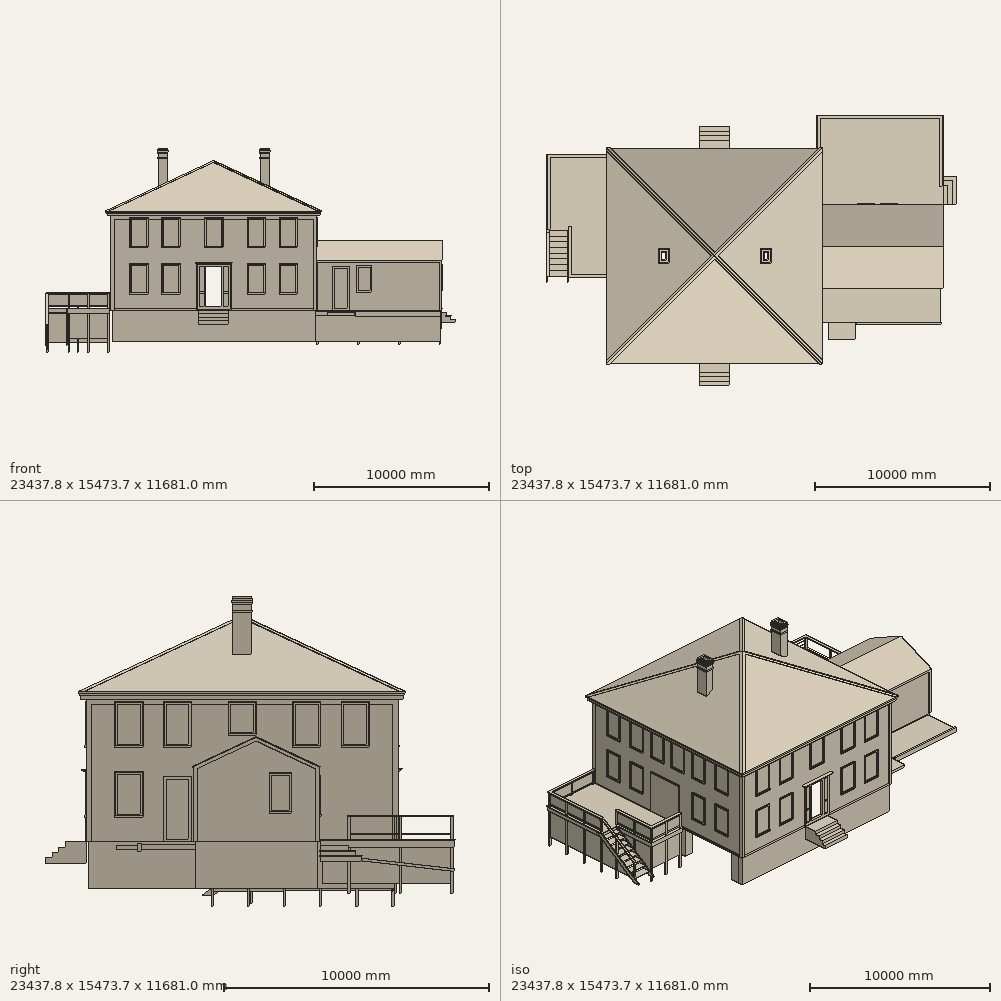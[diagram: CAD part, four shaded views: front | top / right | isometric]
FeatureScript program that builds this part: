
annotation { "Feature Type Name" : "Feature", "Feature Type Description" : "" }
export const myFeature = defineFeature(function(context is Context, id is Id, definition is map)
    precondition{}
    {
        {
            var Q0;
            Q0=qCreatedBy(makeId("Top.planeOp"),FACE);
            var sketch = newSketch(context, id + "F0", { "sketchPlane" : qUnion([Q0])});
            skLineSegment(sketch, "E0.bottom", {"start": v(0, 0) * mm, "end": v(11785.6, 0) * mm});
            skLineSegment(sketch, "E0.top", {"start": v(0, 11785.6) * mm, "end": v(11785.6, 11785.6) * mm});
            skLineSegment(sketch, "E0.left", {"start": v(0, 0) * mm, "end": v(0, 11785.6) * mm});
            skLineSegment(sketch, "E0.right", {"start": v(11785.6, 0) * mm, "end": v(11785.6, 11785.6) * mm});
            skSolve(sketch);
        }
        {
            var Q0;
            Q0=makeQuery(id+"F0.imprint","IMPRINT",FACE,{"disambiguationData":[TD([[makeQuery(id+"F0.imprint","IMPRINT",EDGE,{"derivedFrom":sQuery(id+"F0.wireOp",EDGE,"E0.bottom")}),1.0]])]});
            extrude(context, id + "F1", {"entities" : qUnion([Q0]), "depth" : 5384.8 * mm});
        }
        {
            var Q0;
            Q0=makeQuery(id+"F1.opExtrude","CAP_FACE",FACE,{"disambiguationData":[OSD([sQuery(id+"F0.wireOp",EDGE,"E0.bottom"),sQuery(id+"F0.wireOp",EDGE,"E0.top"),sQuery(id+"F0.wireOp",EDGE,"E0.left"),sQuery(id+"F0.wireOp",EDGE,"E0.right")])],"isStart":false});
            var sketch = newSketch(context, id + "F2", { "sketchPlane" : qUnion([Q0])});
            skLineSegment(sketch, "E1.0", {"start": v(11988.8, 11988.8) * mm, "end": v(-203.2, 11988.8) * mm});
            skLineSegment(sketch, "E1.1", {"start": v(11988.8, -203.2) * mm, "end": v(11988.8, 11988.8) * mm});
            skLineSegment(sketch, "E1.2", {"start": v(-203.2, -203.2) * mm, "end": v(11988.8, -203.2) * mm});
            skLineSegment(sketch, "E1.3", {"start": v(-203.2, 11988.8) * mm, "end": v(-203.2, -203.2) * mm});
            skSolve(sketch);
        }
        {
            var Q0;
            Q0 = qSketchRegion(id + "F2", true);
            extrude(context, id + "F3", {"entities" : qUnion([Q0]), "operationType" : NewBodyOperationType.ADD, "depth" : 152.4 * mm});
        }
        {
            var Q0;
            Q0=makeQuery(id+"F3.opExtrude","CAP_FACE",FACE,{"disambiguationData":[OSD([sQuery(id+"F2.wireOp",EDGE,"E1.0"),sQuery(id+"F2.wireOp",EDGE,"E1.1"),sQuery(id+"F2.wireOp",EDGE,"E1.2"),sQuery(id+"F2.wireOp",EDGE,"E1.3")])],"isStart":false});
            var sketch = newSketch(context, id + "F4", { "sketchPlane" : qUnion([Q0])});
            skLineSegment(sketch, "E2.0", {"start": v(12014.2, 12014.2) * mm, "end": v(-228.6, 12014.2) * mm});
            skLineSegment(sketch, "E2.1", {"start": v(12014.2, -228.6) * mm, "end": v(12014.2, 12014.2) * mm});
            skLineSegment(sketch, "E2.2", {"start": v(-228.6, -228.6) * mm, "end": v(12014.2, -228.6) * mm});
            skLineSegment(sketch, "E2.3", {"start": v(-228.6, 12014.2) * mm, "end": v(-228.6, -228.6) * mm});
            skSolve(sketch);
        }
        {
            var Q0;
            Q0 = qSketchRegion(id + "F4", true);
            extrude(context, id + "F5", {"entities" : qUnion([Q0]), "operationType" : NewBodyOperationType.ADD, "depth" : 38.1 * mm});
        }
        {
            var Q0;
            Q0=makeQuery(id+"F5.opExtrude","CAP_FACE",FACE,{"disambiguationData":[OSD([sQuery(id+"F4.wireOp",EDGE,"E2.0"),sQuery(id+"F4.wireOp",EDGE,"E2.1"),sQuery(id+"F4.wireOp",EDGE,"E2.2"),sQuery(id+"F4.wireOp",EDGE,"E2.3")])],"isStart":false});
            var sketch = newSketch(context, id + "F6", { "sketchPlane" : qUnion([Q0])});
            skLineSegment(sketch, "E3.0", {"start": v(12065, 12065) * mm, "end": v(-279.4, 12065) * mm});
            skLineSegment(sketch, "E3.1", {"start": v(12065, -279.4) * mm, "end": v(12065, 12065) * mm});
            skLineSegment(sketch, "E3.2", {"start": v(-279.4, -279.4) * mm, "end": v(12065, -279.4) * mm});
            skLineSegment(sketch, "E3.3", {"start": v(-279.4, 12065) * mm, "end": v(-279.4, -279.4) * mm});
            skSolve(sketch);
        }
        {
            var Q0;
            Q0 = qSketchRegion(id + "F6", true);
            extrude(context, id + "F7", {"entities" : qUnion([Q0]), "operationType" : NewBodyOperationType.ADD, "depth" : 76.2 * mm});
        }
        {
            var Q0;
            Q0=makeQuery(id+"F7.opExtrude","CAP_FACE",FACE,{"disambiguationData":[OSD([sQuery(id+"F6.wireOp",EDGE,"E3.0"),sQuery(id+"F6.wireOp",EDGE,"E3.1"),sQuery(id+"F6.wireOp",EDGE,"E3.2"),sQuery(id+"F6.wireOp",EDGE,"E3.3")])],"isStart":false});
            extrude(context, id + "F8", {"entities" : qUnion([Q0]), "operationType" : NewBodyOperationType.ADD, "depth" : 2921 * mm, "hasDraft" : true, "draftAngle" : 65 * degree, "draftPullDirection" : true});
        }
        {
            var Q0;
            Q0=makeQuery(id+"F1.opExtrude","SWEPT_FACE",FACE,{"disambiguationData":[OSD([sQuery(id+"F0.wireOp",EDGE,"E0.right")])]});
            var sketch = newSketch(context, id + "F9", { "sketchPlane" : qUnion([Q0])});
            skLineSegment(sketch, "E4", {"start": v(203.2, 0) * mm, "end": v(203.2, 5181.6) * mm});
            skLineSegment(sketch, "E5", {"start": v(203.2, 5181.6) * mm, "end": v(11582.4, 5181.6) * mm});
            skLineSegment(sketch, "E6", {"start": v(11582.4, 5181.6) * mm, "end": v(11582.4, 0) * mm});
            skSolve(sketch);
        }
        {
            var Q0;
            {var subQ0=sQuery(id+"F9.wireOp",EDGE,"E4");Q0=makeQuery(id+"F9.imprint","IMPRINT",FACE,{"disambiguationData":[TD([[makeQuery(id+"F9.imprint","IMPRINT",EDGE,{"derivedFrom":subQ0}),-1.0]])]});}
            extrude(context, id + "F10", {"entities" : qUnion([Q0]), "operationType" : NewBodyOperationType.REMOVE, "oppositeDirection" : true, "depth" : 25.4 * mm});
        }
        {
            var Q0;
            Q0=makeQuery(id+"F1.opExtrude","SWEPT_FACE",FACE,{"disambiguationData":[OSD([sQuery(id+"F0.wireOp",EDGE,"E0.left")])]});
            var sketch = newSketch(context, id + "F11", { "sketchPlane" : qUnion([Q0])});
            skLineSegment(sketch, "E7.0.0", {"start": v(-11582.4, 0) * mm, "end": v(-11582.4, 5181.6) * mm});
            skLineSegment(sketch, "E7.0.1", {"start": v(-11582.4, 5181.6) * mm, "end": v(-203.2, 5181.6) * mm});
            skLineSegment(sketch, "E7.0.2", {"start": v(-203.2, 5181.6) * mm, "end": v(-203.2, 0) * mm});
            skLineSegment(sketch, "E7.0.3", {"start": v(-203.2, 0) * mm, "end": v(-11582.4, 0) * mm});
            skSolve(sketch);
        }
        {
            var Q0;
            Q0 = qSketchRegion(id + "F11", true);
            extrude(context, id + "F12", {"entities" : qUnion([Q0]), "operationType" : NewBodyOperationType.REMOVE, "oppositeDirection" : true, "depth" : 25.4 * mm});
        }
        {
            var Q0;
            Q0=makeQuery(id+"F1.opExtrude","SWEPT_FACE",FACE,{"disambiguationData":[OSD([sQuery(id+"F0.wireOp",EDGE,"E0.top")])]});
            var sketch = newSketch(context, id + "F13", { "sketchPlane" : qUnion([Q0])});
            skLineSegment(sketch, "E8", {"start": v(-11582.4, 0) * mm, "end": v(-11582.4, 5181.6) * mm});
            skLineSegment(sketch, "E9", {"start": v(-11582.4, 5181.6) * mm, "end": v(-203.2, 5181.6) * mm});
            skLineSegment(sketch, "E10", {"start": v(-203.2, 5181.6) * mm, "end": v(-203.2, 0) * mm});
            skSolve(sketch);
        }
        {
            var Q0;
            {var subQ0=sQuery(id+"F13.wireOp",EDGE,"E8");Q0=makeQuery(id+"F13.imprint","IMPRINT",FACE,{"disambiguationData":[TD([[makeQuery(id+"F13.imprint","IMPRINT",EDGE,{"derivedFrom":subQ0}),-1.0]])]});}
            extrude(context, id + "F14", {"entities" : qUnion([Q0]), "operationType" : NewBodyOperationType.REMOVE, "oppositeDirection" : true, "depth" : 25.4 * mm});
        }
        {
            var Q0;
            Q0=makeQuery(id+"F1.opExtrude","SWEPT_FACE",FACE,{"disambiguationData":[OSD([sQuery(id+"F0.wireOp",EDGE,"E0.bottom")])]});
            var sketch = newSketch(context, id + "F15", { "sketchPlane" : qUnion([Q0])});
            skLineSegment(sketch, "E11.0.0", {"start": v(203.2, 0) * mm, "end": v(203.2, 5181.6) * mm});
            skLineSegment(sketch, "E11.0.1", {"start": v(203.2, 5181.6) * mm, "end": v(11582.4, 5181.6) * mm});
            skLineSegment(sketch, "E11.0.2", {"start": v(11582.4, 5181.6) * mm, "end": v(11582.4, 0) * mm});
            skLineSegment(sketch, "E11.0.3", {"start": v(11582.4, 0) * mm, "end": v(203.2, 0) * mm});
            skSolve(sketch);
        }
        {
            var Q0;
            Q0=makeQuery(id+"F15.imprint","IMPRINT",FACE,{"disambiguationData":[TD([[makeQuery(id+"F15.imprint","IMPRINT",EDGE,{"derivedFrom":sQuery(id+"F15.wireOp",EDGE,"E11.0.0")}),-1.0]])]});
            extrude(context, id + "F16", {"entities" : qUnion([Q0]), "operationType" : NewBodyOperationType.REMOVE, "oppositeDirection" : true, "depth" : 25.4 * mm});
        }
        {
            var Q0;
            Q0=makeQuery(id+"F16.boolean.opBoolean","COPY",FACE,{"derivedFrom":makeQuery(id+"F16.opExtrude","CAP_FACE",FACE,{"disambiguationData":[OSD([sQuery(id+"F15.wireOp",EDGE,"E11.0.0"),sQuery(id+"F15.wireOp",EDGE,"E11.0.1"),sQuery(id+"F15.wireOp",EDGE,"E11.0.2"),sQuery(id+"F15.wireOp",EDGE,"E11.0.3")])],"isStart":false})});
            var sketch = newSketch(context, id + "F17", { "sketchPlane" : qUnion([Q0])});
            skLineSegment(sketch, "E12", {"start": v(5892.8, 5181.6) * mm, "end": v(5892.8, 3556) * mm, "construction": true});
            skPoint(sketch, "E12.endSnap0", {"position": v(5892.8, 5181.6) * mm});
            skLineSegment(sketch, "E13.bottom", {"start": v(9626.6, 5283.2) * mm, "end": v(10693.4, 5283.2) * mm});
            skLineSegment(sketch, "E13.top", {"start": v(9626.6, 3556) * mm, "end": v(10693.4, 3556) * mm});
            skLineSegment(sketch, "E13.left", {"start": v(9626.6, 5283.2) * mm, "end": v(9626.6, 3556) * mm});
            skLineSegment(sketch, "E13.right", {"start": v(10693.4, 5283.2) * mm, "end": v(10693.4, 3556) * mm});
            skLineSegment(sketch, "E14.bottom", {"start": v(7797.8, 5283.2) * mm, "end": v(8864.6, 5283.2) * mm});
            skLineSegment(sketch, "E14.top", {"start": v(7797.8, 3556) * mm, "end": v(8864.6, 3556) * mm});
            skLineSegment(sketch, "E14.left", {"start": v(7797.8, 5283.2) * mm, "end": v(7797.8, 3556) * mm});
            skLineSegment(sketch, "E14.right", {"start": v(8864.6, 5283.2) * mm, "end": v(8864.6, 3556) * mm});
            skLineSegment(sketch, "E15.bottom", {"start": v(5359.4, 5283.2) * mm, "end": v(6426.2, 5283.2) * mm});
            skLineSegment(sketch, "E15.top", {"start": v(5359.4, 3556) * mm, "end": v(6426.2, 3556) * mm});
            skLineSegment(sketch, "E15.left", {"start": v(5359.4, 5283.2) * mm, "end": v(5359.4, 3556) * mm});
            skLineSegment(sketch, "E15.right", {"start": v(6426.2, 5283.2) * mm, "end": v(6426.2, 3556) * mm});
            skLineSegment(sketch, "E16.bottom", {"start": v(2921, 5283.2) * mm, "end": v(3987.8, 5283.2) * mm});
            skLineSegment(sketch, "E16.top", {"start": v(2921, 3556) * mm, "end": v(3987.8, 3556) * mm});
            skLineSegment(sketch, "E16.left", {"start": v(2921, 5283.2) * mm, "end": v(2921, 3556) * mm});
            skLineSegment(sketch, "E16.right", {"start": v(3987.8, 5283.2) * mm, "end": v(3987.8, 3556) * mm});
            skLineSegment(sketch, "E17.bottom", {"start": v(1092.2, 5283.2) * mm, "end": v(2159, 5283.2) * mm});
            skLineSegment(sketch, "E17.top", {"start": v(1092.2, 3556) * mm, "end": v(2159, 3556) * mm});
            skLineSegment(sketch, "E17.left", {"start": v(1092.2, 5283.2) * mm, "end": v(1092.2, 3556) * mm});
            skLineSegment(sketch, "E17.right", {"start": v(2159, 5283.2) * mm, "end": v(2159, 3556) * mm});
            skLineSegment(sketch, "E18.bottom", {"start": v(1092.2, 2641.6) * mm, "end": v(2159, 2641.6) * mm});
            skLineSegment(sketch, "E18.top", {"start": v(1092.2, 914.4) * mm, "end": v(2159, 914.4) * mm});
            skLineSegment(sketch, "E18.left", {"start": v(1092.2, 2641.6) * mm, "end": v(1092.2, 914.4) * mm});
            skLineSegment(sketch, "E18.right", {"start": v(2159, 2641.6) * mm, "end": v(2159, 914.4) * mm});
            skLineSegment(sketch, "E19.bottom", {"start": v(2921, 2641.6) * mm, "end": v(3987.8, 2641.6) * mm});
            skLineSegment(sketch, "E19.top", {"start": v(2921, 914.4) * mm, "end": v(3987.8, 914.4) * mm});
            skLineSegment(sketch, "E19.left", {"start": v(2921, 2641.6) * mm, "end": v(2921, 914.4) * mm});
            skLineSegment(sketch, "E19.right", {"start": v(3987.8, 2641.6) * mm, "end": v(3987.8, 914.4) * mm});
            skLineSegment(sketch, "E20.bottom", {"start": v(7797.8, 2641.6) * mm, "end": v(8864.6, 2641.6) * mm});
            skLineSegment(sketch, "E20.top", {"start": v(7797.8, 914.4) * mm, "end": v(8864.6, 914.4) * mm});
            skLineSegment(sketch, "E20.left", {"start": v(7797.8, 2641.6) * mm, "end": v(7797.8, 914.4) * mm});
            skLineSegment(sketch, "E20.right", {"start": v(8864.6, 2641.6) * mm, "end": v(8864.6, 914.4) * mm});
            skLineSegment(sketch, "E21.bottom", {"start": v(9626.6, 2641.6) * mm, "end": v(10693.4, 2641.6) * mm});
            skLineSegment(sketch, "E21.top", {"start": v(9626.6, 914.4) * mm, "end": v(10693.4, 914.4) * mm});
            skLineSegment(sketch, "E21.left", {"start": v(9626.6, 2641.6) * mm, "end": v(9626.6, 914.4) * mm});
            skLineSegment(sketch, "E21.right", {"start": v(10693.4, 2641.6) * mm, "end": v(10693.4, 914.4) * mm});
            skLineSegment(sketch, "E22.bottom", {"start": v(4902.2, 2641.6) * mm, "end": v(6883.4, 2641.6) * mm});
            skLineSegment(sketch, "E22.top", {"start": v(4902.2, 0) * mm, "end": v(6883.4, 0) * mm});
            skLineSegment(sketch, "E22.left", {"start": v(4902.2, 2641.6) * mm, "end": v(4902.2, 0) * mm});
            skLineSegment(sketch, "E22.right", {"start": v(6883.4, 2641.6) * mm, "end": v(6883.4, 0) * mm});
            skSolve(sketch);
        }
        {
            var Q0;
            Q0 = qSketchRegion(id + "F17", true);
            extrude(context, id + "F18", {"entities" : qUnion([Q0]), "operationType" : NewBodyOperationType.ADD, "depth" : 30.48 * mm});
        }
        {
            var Q0;
            Q0=makeQuery(id+"F10.boolean.opBoolean","COPY",FACE,{"derivedFrom":makeQuery(id+"F10.opExtrude","CAP_FACE",FACE,{"disambiguationData":[OSD([sQuery(id+"F0.wireOp",EDGE,"E0.right"),sQuery(id+"F9.wireOp",EDGE,"E4"),sQuery(id+"F9.wireOp",EDGE,"E5"),sQuery(id+"F9.wireOp",EDGE,"E6")])],"isStart":false})});
            var sketch = newSketch(context, id + "F19", { "sketchPlane" : qUnion([Q0])});
            skLineSegment(sketch, "E23.bottom", {"start": v(1092.2, 5283.2) * mm, "end": v(2159, 5283.2) * mm});
            skLineSegment(sketch, "E23.top", {"start": v(1092.2, 3556) * mm, "end": v(2159, 3556) * mm});
            skLineSegment(sketch, "E23.left", {"start": v(1092.2, 5283.2) * mm, "end": v(1092.2, 3556) * mm});
            skLineSegment(sketch, "E23.right", {"start": v(2159, 5283.2) * mm, "end": v(2159, 3556) * mm});
            skLineSegment(sketch, "E24.bottom", {"start": v(2921, 5283.2) * mm, "end": v(3987.8, 5283.2) * mm});
            skLineSegment(sketch, "E24.top", {"start": v(2921, 3556) * mm, "end": v(3987.8, 3556) * mm});
            skLineSegment(sketch, "E24.left", {"start": v(2921, 5283.2) * mm, "end": v(2921, 3556) * mm});
            skLineSegment(sketch, "E24.right", {"start": v(3987.8, 5283.2) * mm, "end": v(3987.8, 3556) * mm});
            skLineSegment(sketch, "E25.bottom", {"start": v(5359.4, 5283.2) * mm, "end": v(6426.2, 5283.2) * mm});
            skLineSegment(sketch, "E25.left", {"start": v(5359.4, 5283.2) * mm, "end": v(5359.4, 4013.2) * mm});
            skLineSegment(sketch, "E25.right", {"start": v(6426.2, 5283.2) * mm, "end": v(6426.2, 4013.2) * mm});
            skLineSegment(sketch, "E26.bottom", {"start": v(7797.8, 5283.2) * mm, "end": v(8864.6, 5283.2) * mm});
            skLineSegment(sketch, "E26.top", {"start": v(7797.8, 3556) * mm, "end": v(8864.6, 3556) * mm});
            skLineSegment(sketch, "E26.left", {"start": v(7797.8, 5283.2) * mm, "end": v(7797.8, 3556) * mm});
            skLineSegment(sketch, "E26.right", {"start": v(8864.6, 5283.2) * mm, "end": v(8864.6, 3556) * mm});
            skLineSegment(sketch, "E27.bottom", {"start": v(9626.6, 5283.2) * mm, "end": v(10693.4, 5283.2) * mm});
            skLineSegment(sketch, "E27.top", {"start": v(9626.6, 3556) * mm, "end": v(10693.4, 3556) * mm});
            skLineSegment(sketch, "E27.left", {"start": v(9626.6, 5283.2) * mm, "end": v(9626.6, 3556) * mm});
            skLineSegment(sketch, "E27.right", {"start": v(10693.4, 5283.2) * mm, "end": v(10693.4, 3556) * mm});
            skLineSegment(sketch, "E28", {"start": v(5892.8, 5181.6) * mm, "end": v(5892.8, 4013.2) * mm, "construction": true});
            skPoint(sketch, "E28.endSnap0", {"position": v(5892.8, 5181.6) * mm});
            skLineSegment(sketch, "E29.bottom", {"start": v(1092.2, 2641.6) * mm, "end": v(2159, 2641.6) * mm});
            skLineSegment(sketch, "E29.top", {"start": v(1092.2, 914.4) * mm, "end": v(2159, 914.4) * mm});
            skLineSegment(sketch, "E29.left", {"start": v(1092.2, 2641.6) * mm, "end": v(1092.2, 914.4) * mm});
            skLineSegment(sketch, "E29.right", {"start": v(2159, 2641.6) * mm, "end": v(2159, 914.4) * mm});
            skLineSegment(sketch, "E30.bottom", {"start": v(2921, 2463.8) * mm, "end": v(3987.8, 2463.8) * mm});
            skLineSegment(sketch, "E30.top", {"start": v(2921, 0) * mm, "end": v(3987.8, 0) * mm});
            skLineSegment(sketch, "E30.left", {"start": v(2921, 2463.8) * mm, "end": v(2921, 0) * mm});
            skLineSegment(sketch, "E30.right", {"start": v(3987.8, 2463.8) * mm, "end": v(3987.8, 0) * mm});
            skLineSegment(sketch, "E31", {"start": v(5359.4, 4013.2) * mm, "end": v(6426.2, 4013.2) * mm});
            skPoint(sketch, "E32.orphan", {"position": v(6426.2, 3556) * mm});
            skSolve(sketch);
        }
        {
            var Q0;
            Q0 = qSketchRegion(id + "F19", true);
            extrude(context, id + "F20", {"entities" : qUnion([Q0]), "operationType" : NewBodyOperationType.ADD, "depth" : 30.48 * mm});
        }
        {
            var Q0;
            Q0=makeQuery(id+"F10.boolean.opBoolean","COPY",FACE,{"derivedFrom":makeQuery(id+"F10.opExtrude","CAP_FACE",FACE,{"disambiguationData":[OSD([sQuery(id+"F0.wireOp",EDGE,"E0.right"),sQuery(id+"F9.wireOp",EDGE,"E4"),sQuery(id+"F9.wireOp",EDGE,"E5"),sQuery(id+"F9.wireOp",EDGE,"E6")])],"isStart":false})});
            var sketch = newSketch(context, id + "F21", { "sketchPlane" : qUnion([Q0])});
            skLineSegment(sketch, "E33", {"start": v(6426.2, 3962.4) * mm, "end": v(8813.8, 2844.8) * mm});
            skLineSegment(sketch, "E34", {"start": v(6426.2, 3962.4) * mm, "end": v(4038.6, 2844.8) * mm});
            skLineSegment(sketch, "E35", {"start": v(4038.6, 2844.8) * mm, "end": v(4038.6, 0) * mm});
            skLineSegment(sketch, "E36", {"start": v(8813.8, 2844.8) * mm, "end": v(8813.8, 0) * mm});
            skLineSegment(sketch, "E37", {"start": v(4038.6, 0) * mm, "end": v(8813.8, 0) * mm});
            skLineSegment(sketch, "E38", {"start": v(6426.2, 3962.4) * mm, "end": v(6426.2, 2033.92) * mm, "construction": true});
            skSolve(sketch);
        }
        {
            var Q0;
            Q0=makeQuery(id+"F21.imprint","IMPRINT",FACE,{"disambiguationData":[TD([[makeQuery(id+"F21.imprint","IMPRINT",EDGE,{"derivedFrom":sQuery(id+"F21.wireOp",EDGE,"E33")}),-1.0]])]});
            extrude(context, id + "F22", {"entities" : qUnion([Q0]), "operationType" : NewBodyOperationType.ADD, "depth" : 7162.8 * mm});
        }
        {
            var Q0;
            Q0=makeQuery(id+"F14.boolean.opBoolean","COPY",FACE,{"derivedFrom":makeQuery(id+"F14.opExtrude","CAP_FACE",FACE,{"disambiguationData":[OSD([sQuery(id+"F0.wireOp",EDGE,"E0.top"),sQuery(id+"F13.wireOp",EDGE,"E8"),sQuery(id+"F13.wireOp",EDGE,"E9"),sQuery(id+"F13.wireOp",EDGE,"E10")])],"isStart":false})});
            var sketch = newSketch(context, id + "F23", { "sketchPlane" : qUnion([Q0])});
            skLineSegment(sketch, "E39.0.0", {"start": v(-2159, 3556) * mm, "end": v(-2159, 5283.2) * mm});
            skLineSegment(sketch, "E39.0.1", {"start": v(-2159, 5283.2) * mm, "end": v(-1092.2, 5283.2) * mm});
            skLineSegment(sketch, "E39.0.2", {"start": v(-1092.2, 5283.2) * mm, "end": v(-1092.2, 3556) * mm});
            skLineSegment(sketch, "E39.0.3", {"start": v(-1092.2, 3556) * mm, "end": v(-2159, 3556) * mm});
            skLineSegment(sketch, "E39.1.0", {"start": v(-3987.8, 3556) * mm, "end": v(-3987.8, 5283.2) * mm});
            skLineSegment(sketch, "E39.1.1", {"start": v(-3987.8, 5283.2) * mm, "end": v(-2921, 5283.2) * mm});
            skLineSegment(sketch, "E39.1.2", {"start": v(-2921, 5283.2) * mm, "end": v(-2921, 3556) * mm});
            skLineSegment(sketch, "E39.1.3", {"start": v(-2921, 3556) * mm, "end": v(-3987.8, 3556) * mm});
            skLineSegment(sketch, "E39.2.0", {"start": v(-6426.2, 3556) * mm, "end": v(-6426.2, 5283.2) * mm});
            skLineSegment(sketch, "E39.2.1", {"start": v(-6426.2, 5283.2) * mm, "end": v(-5359.4, 5283.2) * mm});
            skLineSegment(sketch, "E39.2.2", {"start": v(-5359.4, 5283.2) * mm, "end": v(-5359.4, 3556) * mm});
            skLineSegment(sketch, "E39.2.3", {"start": v(-5359.4, 3556) * mm, "end": v(-6426.2, 3556) * mm});
            skLineSegment(sketch, "E39.3.0", {"start": v(-8864.6, 3556) * mm, "end": v(-8864.6, 5283.2) * mm});
            skLineSegment(sketch, "E39.3.1", {"start": v(-8864.6, 5283.2) * mm, "end": v(-7797.8, 5283.2) * mm});
            skLineSegment(sketch, "E39.3.2", {"start": v(-7797.8, 5283.2) * mm, "end": v(-7797.8, 3556) * mm});
            skLineSegment(sketch, "E39.3.3", {"start": v(-7797.8, 3556) * mm, "end": v(-8864.6, 3556) * mm});
            skLineSegment(sketch, "E39.4.0", {"start": v(-10693.4, 3556) * mm, "end": v(-10693.4, 5283.2) * mm});
            skLineSegment(sketch, "E39.4.1", {"start": v(-10693.4, 5283.2) * mm, "end": v(-9626.6, 5283.2) * mm});
            skLineSegment(sketch, "E39.4.2", {"start": v(-9626.6, 5283.2) * mm, "end": v(-9626.6, 3556) * mm});
            skLineSegment(sketch, "E39.4.3", {"start": v(-9626.6, 3556) * mm, "end": v(-10693.4, 3556) * mm});
            skLineSegment(sketch, "E39.5.0", {"start": v(-9626.6, 2641.6) * mm, "end": v(-9626.6, 914.4) * mm});
            skLineSegment(sketch, "E39.5.1", {"start": v(-9626.6, 914.4) * mm, "end": v(-10693.4, 914.4) * mm});
            skLineSegment(sketch, "E39.5.2", {"start": v(-10693.4, 914.4) * mm, "end": v(-10693.4, 2641.6) * mm});
            skLineSegment(sketch, "E39.5.3", {"start": v(-10693.4, 2641.6) * mm, "end": v(-9626.6, 2641.6) * mm});
            skLineSegment(sketch, "E39.6.0", {"start": v(-7797.8, 2641.6) * mm, "end": v(-7797.8, 914.4) * mm});
            skLineSegment(sketch, "E39.6.1", {"start": v(-7797.8, 914.4) * mm, "end": v(-8864.6, 914.4) * mm});
            skLineSegment(sketch, "E39.6.2", {"start": v(-8864.6, 914.4) * mm, "end": v(-8864.6, 2641.6) * mm});
            skLineSegment(sketch, "E39.6.3", {"start": v(-8864.6, 2641.6) * mm, "end": v(-7797.8, 2641.6) * mm});
            skLineSegment(sketch, "E39.7.0", {"start": v(-6883.4, 0) * mm, "end": v(-6883.4, 2641.6) * mm});
            skLineSegment(sketch, "E39.7.1", {"start": v(-6883.4, 2641.6) * mm, "end": v(-4902.2, 2641.6) * mm});
            skLineSegment(sketch, "E39.7.2", {"start": v(-4902.2, 2641.6) * mm, "end": v(-4902.2, 0) * mm});
            skLineSegment(sketch, "E39.7.3", {"start": v(-4902.2, 0) * mm, "end": v(-6883.4, 0) * mm});
            skLineSegment(sketch, "E39.8.0", {"start": v(-2921, 2641.6) * mm, "end": v(-2921, 914.4) * mm});
            skLineSegment(sketch, "E39.8.1", {"start": v(-2921, 914.4) * mm, "end": v(-3987.8, 914.4) * mm});
            skLineSegment(sketch, "E39.8.2", {"start": v(-3987.8, 914.4) * mm, "end": v(-3987.8, 2641.6) * mm});
            skLineSegment(sketch, "E39.8.3", {"start": v(-3987.8, 2641.6) * mm, "end": v(-2921, 2641.6) * mm});
            skLineSegment(sketch, "E39.9.0", {"start": v(-1092.2, 2641.6) * mm, "end": v(-1092.2, 914.4) * mm});
            skLineSegment(sketch, "E39.9.1", {"start": v(-1092.2, 914.4) * mm, "end": v(-2159, 914.4) * mm});
            skLineSegment(sketch, "E39.9.2", {"start": v(-2159, 914.4) * mm, "end": v(-2159, 2641.6) * mm});
            skLineSegment(sketch, "E39.9.3", {"start": v(-2159, 2641.6) * mm, "end": v(-1092.2, 2641.6) * mm});
            skSolve(sketch);
        }
        {
            var Q0;
            Q0 = qSketchRegion(id + "F23", true);
            extrude(context, id + "F24", {"entities" : qUnion([Q0]), "operationType" : NewBodyOperationType.ADD, "depth" : 30.48 * mm});
        }
        {
            var Q0;
            Q0=makeQuery(id+"F12.boolean.opBoolean","COPY",FACE,{"derivedFrom":makeQuery(id+"F12.opExtrude","CAP_FACE",FACE,{"disambiguationData":[OSD([sQuery(id+"F11.wireOp",EDGE,"E7.0.0"),sQuery(id+"F11.wireOp",EDGE,"E7.0.1"),sQuery(id+"F11.wireOp",EDGE,"E7.0.2"),sQuery(id+"F11.wireOp",EDGE,"E7.0.3")])],"isStart":false})});
            var sketch = newSketch(context, id + "F25", { "sketchPlane" : qUnion([Q0])});
            skLineSegment(sketch, "E40.0.0", {"start": v(-2159, 3556) * mm, "end": v(-2159, 5283.2) * mm});
            skLineSegment(sketch, "E40.0.1", {"start": v(-2159, 5283.2) * mm, "end": v(-1092.2, 5283.2) * mm});
            skLineSegment(sketch, "E40.0.2", {"start": v(-1092.2, 5283.2) * mm, "end": v(-1092.2, 3556) * mm});
            skLineSegment(sketch, "E40.0.3", {"start": v(-1092.2, 3556) * mm, "end": v(-2159, 3556) * mm});
            skLineSegment(sketch, "E40.1.0", {"start": v(-3987.8, 3556) * mm, "end": v(-3987.8, 5283.2) * mm});
            skLineSegment(sketch, "E40.1.1", {"start": v(-3987.8, 5283.2) * mm, "end": v(-2921, 5283.2) * mm});
            skLineSegment(sketch, "E40.1.2", {"start": v(-2921, 5283.2) * mm, "end": v(-2921, 3556) * mm});
            skLineSegment(sketch, "E40.1.3", {"start": v(-2921, 3556) * mm, "end": v(-3987.8, 3556) * mm});
            skLineSegment(sketch, "E40.2.0", {"start": v(-8864.6, 3556) * mm, "end": v(-8864.6, 5283.2) * mm});
            skLineSegment(sketch, "E40.2.1", {"start": v(-8864.6, 5283.2) * mm, "end": v(-7797.8, 5283.2) * mm});
            skLineSegment(sketch, "E40.2.2", {"start": v(-7797.8, 5283.2) * mm, "end": v(-7797.8, 3556) * mm});
            skLineSegment(sketch, "E40.2.3", {"start": v(-7797.8, 3556) * mm, "end": v(-8864.6, 3556) * mm});
            skLineSegment(sketch, "E40.3.0", {"start": v(-10693.4, 3556) * mm, "end": v(-10693.4, 5283.2) * mm});
            skLineSegment(sketch, "E40.3.1", {"start": v(-10693.4, 5283.2) * mm, "end": v(-9626.6, 5283.2) * mm});
            skLineSegment(sketch, "E40.3.2", {"start": v(-9626.6, 5283.2) * mm, "end": v(-9626.6, 3556) * mm});
            skLineSegment(sketch, "E40.3.3", {"start": v(-9626.6, 3556) * mm, "end": v(-10693.4, 3556) * mm});
            skLineSegment(sketch, "E40.4.0", {"start": v(-1092.2, 2641.6) * mm, "end": v(-1092.2, 914.4) * mm});
            skLineSegment(sketch, "E40.4.1", {"start": v(-1092.2, 914.4) * mm, "end": v(-2159, 914.4) * mm});
            skLineSegment(sketch, "E40.4.2", {"start": v(-2159, 914.4) * mm, "end": v(-2159, 2641.6) * mm});
            skLineSegment(sketch, "E40.4.3", {"start": v(-2159, 2641.6) * mm, "end": v(-1092.2, 2641.6) * mm});
            skLineSegment(sketch, "E41.bottom", {"start": v(-10693.4, 2641.6) * mm, "end": v(-9626.6, 2641.6) * mm});
            skLineSegment(sketch, "E41.top", {"start": v(-10693.4, 914.4) * mm, "end": v(-9626.6, 914.4) * mm});
            skLineSegment(sketch, "E41.left", {"start": v(-10693.4, 2641.6) * mm, "end": v(-10693.4, 914.4) * mm});
            skLineSegment(sketch, "E41.right", {"start": v(-9626.6, 2641.6) * mm, "end": v(-9626.6, 914.4) * mm});
            skLineSegment(sketch, "E42.bottom", {"start": v(-8864.6, 2641.6) * mm, "end": v(-7797.8, 2641.6) * mm});
            skLineSegment(sketch, "E42.top", {"start": v(-8864.6, 914.4) * mm, "end": v(-7797.8, 914.4) * mm});
            skLineSegment(sketch, "E42.left", {"start": v(-8864.6, 2641.6) * mm, "end": v(-8864.6, 914.4) * mm});
            skLineSegment(sketch, "E42.right", {"start": v(-7797.8, 2641.6) * mm, "end": v(-7797.8, 914.4) * mm});
            skLineSegment(sketch, "E43.bottom", {"start": v(-3987.8, 2641.6) * mm, "end": v(-2921, 2641.6) * mm});
            skLineSegment(sketch, "E43.top", {"start": v(-3987.8, 914.4) * mm, "end": v(-2921, 914.4) * mm});
            skLineSegment(sketch, "E43.left", {"start": v(-3987.8, 2641.6) * mm, "end": v(-3987.8, 914.4) * mm});
            skLineSegment(sketch, "E43.right", {"start": v(-2921, 2641.6) * mm, "end": v(-2921, 914.4) * mm});
            skLineSegment(sketch, "E44.bottom", {"start": v(-7239, 5283.2) * mm, "end": v(-6172.2, 5283.2) * mm});
            skLineSegment(sketch, "E44.top", {"start": v(-7239, 3556) * mm, "end": v(-6172.2, 3556) * mm});
            skLineSegment(sketch, "E44.left", {"start": v(-7239, 5283.2) * mm, "end": v(-7239, 3556) * mm});
            skLineSegment(sketch, "E44.right", {"start": v(-6172.2, 5283.2) * mm, "end": v(-6172.2, 3556) * mm});
            skLineSegment(sketch, "E45.bottom", {"start": v(-5613.4, 5283.2) * mm, "end": v(-4546.6, 5283.2) * mm});
            skLineSegment(sketch, "E45.top", {"start": v(-5613.4, 3556) * mm, "end": v(-4546.6, 3556) * mm});
            skLineSegment(sketch, "E45.left", {"start": v(-5613.4, 5283.2) * mm, "end": v(-5613.4, 3556) * mm});
            skLineSegment(sketch, "E45.right", {"start": v(-4546.6, 5283.2) * mm, "end": v(-4546.6, 3556) * mm});
            skLineSegment(sketch, "E46.bottom", {"start": v(-7239, 2641.6) * mm, "end": v(-5003.8, 2641.6) * mm});
            skLineSegment(sketch, "E46.top", {"start": v(-7239, 0) * mm, "end": v(-5003.8, 0) * mm});
            skLineSegment(sketch, "E46.left", {"start": v(-7239, 2641.6) * mm, "end": v(-7239, 0) * mm});
            skLineSegment(sketch, "E46.right", {"start": v(-5003.8, 2641.6) * mm, "end": v(-5003.8, 0) * mm});
            skSolve(sketch);
        }
        {
            var Q0;
            Q0 = qSketchRegion(id + "F25", true);
            extrude(context, id + "F26", {"entities" : qUnion([Q0]), "operationType" : NewBodyOperationType.ADD, "depth" : 30.48 * mm});
        }
        {
            var Q0;
            Q0=makeQuery(id+"F22.opExtrude","SWEPT_FACE",FACE,{"disambiguationData":[OSD([sQuery(id+"F21.wireOp",EDGE,"E35")])]});
            var sketch = newSketch(context, id + "F27", { "sketchPlane" : qUnion([Q0])});
            skLineSegment(sketch, "E47", {"start": v(11811, 0) * mm, "end": v(11811, 2692.4) * mm});
            skLineSegment(sketch, "E48", {"start": v(11811, 2692.4) * mm, "end": v(18770.6, 2692.4) * mm});
            skLineSegment(sketch, "E49", {"start": v(18770.6, 2692.4) * mm, "end": v(18770.6, 0) * mm});
            skSolve(sketch);
        }
        {
            var Q0;
            {var subQ0=sQuery(id+"F27.wireOp",EDGE,"E47");Q0=makeQuery(id+"F27.imprint","IMPRINT",FACE,{"disambiguationData":[TD([[makeQuery(id+"F27.imprint","IMPRINT",EDGE,{"derivedFrom":subQ0}),-1.0]])]});}
            extrude(context, id + "F28", {"entities" : qUnion([Q0]), "operationType" : NewBodyOperationType.REMOVE, "oppositeDirection" : true, "depth" : 25.4 * mm});
        }
        {
            var Q0;
            Q0=makeQuery(id+"F28.boolean.opBoolean","COPY",FACE,{"derivedFrom":makeQuery(id+"F28.opExtrude","CAP_FACE",FACE,{"disambiguationData":[OSD([sQuery(id+"F0.wireOp",EDGE,"E0.right"),sQuery(id+"F21.wireOp",EDGE,"E35"),sQuery(id+"F21.wireOp",EDGE,"E37"),sQuery(id+"F27.wireOp",EDGE,"E47"),sQuery(id+"F27.wireOp",EDGE,"E48"),sQuery(id+"F27.wireOp",EDGE,"E49")])],"isStart":false})});
            var sketch = newSketch(context, id + "F29", { "sketchPlane" : qUnion([Q0])});
            skLineSegment(sketch, "E50.bottom", {"start": v(12700, 2489.2) * mm, "end": v(13665.2, 2489.2) * mm});
            skLineSegment(sketch, "E50.top", {"start": v(12700, 0) * mm, "end": v(13665.2, 0) * mm});
            skLineSegment(sketch, "E50.left", {"start": v(12700, 2489.2) * mm, "end": v(12700, 0) * mm});
            skLineSegment(sketch, "E50.right", {"start": v(13665.2, 2489.2) * mm, "end": v(13665.2, 0) * mm});
            skLineSegment(sketch, "E51.bottom", {"start": v(14046.2, 2540) * mm, "end": v(14935.2, 2540) * mm});
            skLineSegment(sketch, "E51.top", {"start": v(14046.2, 1016) * mm, "end": v(14935.2, 1016) * mm});
            skLineSegment(sketch, "E51.left", {"start": v(14046.2, 2540) * mm, "end": v(14046.2, 1016) * mm});
            skLineSegment(sketch, "E51.right", {"start": v(14935.2, 2540) * mm, "end": v(14935.2, 1016) * mm});
            skSolve(sketch);
        }
        {
            var Q0;
            Q0 = qSketchRegion(id + "F29", true);
            extrude(context, id + "F30", {"entities" : qUnion([Q0]), "operationType" : NewBodyOperationType.ADD, "depth" : 25.4 * mm});
        }
        {
            var Q0;
            Q0=makeQuery(id+"F22.opExtrude","CAP_FACE",FACE,{"disambiguationData":[OSD([sQuery(id+"F21.wireOp",EDGE,"E33"),sQuery(id+"F21.wireOp",EDGE,"E34"),sQuery(id+"F21.wireOp",EDGE,"E35"),sQuery(id+"F21.wireOp",EDGE,"E36"),sQuery(id+"F21.wireOp",EDGE,"E37")])],"isStart":false});
            var sketch = newSketch(context, id + "F31", { "sketchPlane" : qUnion([Q0])});
            skLineSegment(sketch, "E52.0", {"start": v(4191, 2747.87) * mm, "end": v(4191, 0) * mm});
            skLineSegment(sketch, "E52.1", {"start": v(6426.2, 3794.13) * mm, "end": v(4191, 2747.87) * mm});
            skLineSegment(sketch, "E52.2", {"start": v(6426.2, 3794.13) * mm, "end": v(8661.4, 2747.87) * mm});
            skLineSegment(sketch, "E52.3", {"start": v(8661.4, 2747.87) * mm, "end": v(8661.4, 0) * mm});
            skSolve(sketch);
        }
        {
            var Q0;
            {var subQ1=sQuery(id+"F31.wireOp",EDGE,"E52.0");Q0=makeQuery(id+"F31.imprint","IMPRINT",FACE,{"disambiguationData":[TD([[makeQuery(id+"F31.imprint","IMPRINT",EDGE,{"derivedFrom":subQ1}),1.0]])]});}
            extrude(context, id + "F32", {"entities" : qUnion([Q0]), "operationType" : NewBodyOperationType.REMOVE, "oppositeDirection" : true, "depth" : 25.4 * mm});
        }
        {
            var Q0;
            Q0=makeQuery(id+"F32.boolean.opBoolean","COPY",FACE,{"derivedFrom":makeQuery(id+"F32.opExtrude","CAP_FACE",FACE,{"disambiguationData":[OSD([sQuery(id+"F21.wireOp",EDGE,"E37"),sQuery(id+"F31.wireOp",EDGE,"E52.0"),sQuery(id+"F31.wireOp",EDGE,"E52.1"),sQuery(id+"F31.wireOp",EDGE,"E52.2"),sQuery(id+"F31.wireOp",EDGE,"E52.3")])],"isStart":false})});
            var sketch = newSketch(context, id + "F33", { "sketchPlane" : qUnion([Q0])});
            skLineSegment(sketch, "E53.bottom", {"start": v(6908.8, 2595.47) * mm, "end": v(7772.4, 2595.47) * mm});
            skLineSegment(sketch, "E53.top", {"start": v(6908.8, 1071.47) * mm, "end": v(7772.4, 1071.47) * mm});
            skLineSegment(sketch, "E53.left", {"start": v(6908.8, 2595.47) * mm, "end": v(6908.8, 1071.47) * mm});
            skLineSegment(sketch, "E53.right", {"start": v(7772.4, 2595.47) * mm, "end": v(7772.4, 1071.47) * mm});
            skSolve(sketch);
        }
        {
            var Q0;
            Q0 = qSketchRegion(id + "F33", true);
            extrude(context, id + "F34", {"entities" : qUnion([Q0]), "operationType" : NewBodyOperationType.ADD, "depth" : 25.4 * mm});
        }
        {
            var Q0;
            Q0=makeQuery(id+"F22.opExtrude","SWEPT_FACE",FACE,{"disambiguationData":[OSD([sQuery(id+"F21.wireOp",EDGE,"E36")])]});
            var sketch = newSketch(context, id + "F35", { "sketchPlane" : qUnion([Q0])});
            skLineSegment(sketch, "E54.0.0", {"start": v(-12700, 2489.2) * mm, "end": v(-13665.2, 2489.2) * mm});
            skLineSegment(sketch, "E54.0.1", {"start": v(-13665.2, 2489.2) * mm, "end": v(-13665.2, 0) * mm});
            skLineSegment(sketch, "E54.0.2", {"start": v(-13665.2, 0) * mm, "end": v(-18770.6, 0) * mm});
            skLineSegment(sketch, "E54.0.3", {"start": v(-18770.6, 0) * mm, "end": v(-18770.6, 2692.4) * mm});
            skLineSegment(sketch, "E54.0.4", {"start": v(-18770.6, 2692.4) * mm, "end": v(-11811, 2692.4) * mm});
            skLineSegment(sketch, "E54.0.5", {"start": v(-11811, 2692.4) * mm, "end": v(-11811, 0) * mm});
            skLineSegment(sketch, "E54.0.6", {"start": v(-11811, 0) * mm, "end": v(-12700, 0) * mm});
            skLineSegment(sketch, "E54.0.7", {"start": v(-12700, 0) * mm, "end": v(-12700, 2489.2) * mm});
            skLineSegment(sketch, "E55.bottom", {"start": v(-15011.4, 2489.2) * mm, "end": v(-14046.2, 2489.2) * mm});
            skLineSegment(sketch, "E55.top", {"start": v(-15011.4, 965.2) * mm, "end": v(-14046.2, 965.2) * mm});
            skLineSegment(sketch, "E55.left", {"start": v(-15011.4, 2489.2) * mm, "end": v(-15011.4, 965.2) * mm});
            skLineSegment(sketch, "E55.right", {"start": v(-14046.2, 2489.2) * mm, "end": v(-14046.2, 965.2) * mm});
            skLineSegment(sketch, "E56.bottom", {"start": v(-16357.6, 2489.2) * mm, "end": v(-15392.4, 2489.2) * mm});
            skLineSegment(sketch, "E56.top", {"start": v(-16357.6, 965.2) * mm, "end": v(-15392.4, 965.2) * mm});
            skLineSegment(sketch, "E56.left", {"start": v(-16357.6, 2489.2) * mm, "end": v(-16357.6, 965.2) * mm});
            skLineSegment(sketch, "E56.right", {"start": v(-15392.4, 2489.2) * mm, "end": v(-15392.4, 965.2) * mm});
            skSolve(sketch);
        }
        {
            var Q0;
            Q0=makeQuery(id+"F30.boolean.opBoolean","MERGE",FACE,{"derivedFrom":[makeQuery(id+"F26.boolean.opBoolean","MERGE",FACE,{"derivedFrom":[makeQuery(id+"F24.boolean.opBoolean","MERGE",FACE,{"derivedFrom":[makeQuery(id+"F22.boolean.opBoolean","MERGE",FACE,{"derivedFrom":[makeQuery(id+"F20.boolean.opBoolean","MERGE",FACE,{"derivedFrom":[makeQuery(id+"F18.boolean.opBoolean","MERGE",FACE,{"derivedFrom":[makeQuery(id+"F1.opExtrude","CAP_FACE",FACE,{"disambiguationData":[OSD([sQuery(id+"F0.wireOp",EDGE,"E0.bottom"),sQuery(id+"F0.wireOp",EDGE,"E0.top"),sQuery(id+"F0.wireOp",EDGE,"E0.left"),sQuery(id+"F0.wireOp",EDGE,"E0.right")])],"isStart":true}),makeQuery(id+"F18.opExtrude","SWEPT_FACE",FACE,{"disambiguationData":[OSD([sQuery(id+"F17.wireOp",EDGE,"E22.top")])]})]}),makeQuery(id+"F20.opExtrude","SWEPT_FACE",FACE,{"disambiguationData":[OSD([sQuery(id+"F19.wireOp",EDGE,"E30.top")])]})]}),makeQuery(id+"F22.opExtrude","SWEPT_FACE",FACE,{"disambiguationData":[OSD([sQuery(id+"F21.wireOp",EDGE,"E37")])]})]}),makeQuery(id+"F24.opExtrude","SWEPT_FACE",FACE,{"disambiguationData":[OSD([sQuery(id+"F23.wireOp",EDGE,"E39.7.3")])]})]}),makeQuery(id+"F26.opExtrude","SWEPT_FACE",FACE,{"disambiguationData":[OSD([sQuery(id+"F25.wireOp",EDGE,"E46.top")])]})]}),makeQuery(id+"F30.opExtrude","SWEPT_FACE",FACE,{"disambiguationData":[OSD([sQuery(id+"F29.wireOp",EDGE,"E50.top")])]})]});
            var sketch = newSketch(context, id + "F36", { "sketchPlane" : qUnion([Q0])});
            skLineSegment(sketch, "E57", {"start": v(5892.8, -5892.8) * mm, "end": v(9067.8, -5892.8) * mm, "construction": true});
            skLineSegment(sketch, "E58.bottom", {"start": v(8559.8, -6248.4) * mm, "end": v(9067.8, -6248.4) * mm});
            skLineSegment(sketch, "E58.top", {"start": v(8559.8, -5537.2) * mm, "end": v(9067.8, -5537.2) * mm});
            skLineSegment(sketch, "E58.left", {"start": v(8559.8, -6248.4) * mm, "end": v(8559.8, -5537.2) * mm});
            skLineSegment(sketch, "E58.right", {"start": v(9067.8, -6248.4) * mm, "end": v(9067.8, -5537.2) * mm});
            skLineSegment(sketch, "E59", {"start": v(5892.8, -5892.8) * mm, "end": v(5892.8, -8379.62) * mm, "construction": true});
            skLineSegment(sketch, "E60.MirrorCS", {"start": v(3225.8, -6248.4) * mm, "end": v(3225.8, -5537.2) * mm});
            skLineSegment(sketch, "E61.MirrorCS", {"start": v(2717.8, -6248.4) * mm, "end": v(2717.8, -5537.2) * mm});
            skLineSegment(sketch, "E62.MirrorCS", {"start": v(3225.8, -6248.4) * mm, "end": v(2717.8, -6248.4) * mm});
            skLineSegment(sketch, "E63.MirrorCS", {"start": v(3225.8, -5537.2) * mm, "end": v(2717.8, -5537.2) * mm});
            skSolve(sketch);
        }
        {
            var Q0;
            Q0 = qSketchRegion(id + "F36", true);
            extrude(context, id + "F37", {"entities" : qUnion([Q0]), "operationType" : NewBodyOperationType.ADD, "oppositeDirection" : true, "depth" : 8636 * mm});
        }
        {
            var Q0;
            Q0=makeQuery(id+"F35.imprint","IMPRINT",FACE,{"disambiguationData":[TD([[makeQuery(id+"F35.imprint","IMPRINT",EDGE,{"derivedFrom":sQuery(id+"F35.wireOp",EDGE,"E54.0.0")}),-1.0]])]});
            extrude(context, id + "F38", {"entities" : qUnion([Q0]), "operationType" : NewBodyOperationType.REMOVE, "oppositeDirection" : true, "depth" : 25.4 * mm});
        }
        {
            var Q0;
            Q0=makeQuery(id+"F30.boolean.opBoolean","MERGE",FACE,{"derivedFrom":[makeQuery(id+"F26.boolean.opBoolean","MERGE",FACE,{"derivedFrom":[makeQuery(id+"F24.boolean.opBoolean","MERGE",FACE,{"derivedFrom":[makeQuery(id+"F22.boolean.opBoolean","MERGE",FACE,{"derivedFrom":[makeQuery(id+"F20.boolean.opBoolean","MERGE",FACE,{"derivedFrom":[makeQuery(id+"F18.boolean.opBoolean","MERGE",FACE,{"derivedFrom":[makeQuery(id+"F1.opExtrude","CAP_FACE",FACE,{"disambiguationData":[OSD([sQuery(id+"F0.wireOp",EDGE,"E0.bottom"),sQuery(id+"F0.wireOp",EDGE,"E0.top"),sQuery(id+"F0.wireOp",EDGE,"E0.left"),sQuery(id+"F0.wireOp",EDGE,"E0.right")])],"isStart":true}),makeQuery(id+"F18.opExtrude","SWEPT_FACE",FACE,{"disambiguationData":[OSD([sQuery(id+"F17.wireOp",EDGE,"E22.top")])]})]}),makeQuery(id+"F20.opExtrude","SWEPT_FACE",FACE,{"disambiguationData":[OSD([sQuery(id+"F19.wireOp",EDGE,"E30.top")])]})]}),makeQuery(id+"F22.opExtrude","SWEPT_FACE",FACE,{"disambiguationData":[OSD([sQuery(id+"F21.wireOp",EDGE,"E37")])]})]}),makeQuery(id+"F24.opExtrude","SWEPT_FACE",FACE,{"disambiguationData":[OSD([sQuery(id+"F23.wireOp",EDGE,"E39.7.3")])]})]}),makeQuery(id+"F26.opExtrude","SWEPT_FACE",FACE,{"disambiguationData":[OSD([sQuery(id+"F25.wireOp",EDGE,"E46.top")])]})]}),makeQuery(id+"F30.opExtrude","SWEPT_FACE",FACE,{"disambiguationData":[OSD([sQuery(id+"F29.wireOp",EDGE,"E50.top")])]})]});
            shell(context, id + "F39", {"entities" : qUnion([Q0]), "thickness" : 152.4 * mm});
        }
        {
            var Q0;
            Q0=makeQuery(id+"F37.opExtrude","CAP_FACE",FACE,{"disambiguationData":[OSD([sQuery(id+"F36.wireOp",EDGE,"E58.bottom"),sQuery(id+"F36.wireOp",EDGE,"E58.top"),sQuery(id+"F36.wireOp",EDGE,"E58.left"),sQuery(id+"F36.wireOp",EDGE,"E58.right")])],"isStart":false});
            var sketch = newSketch(context, id + "F40", { "sketchPlane" : qUnion([Q0])});
            skLineSegment(sketch, "E64.0", {"start": v(8534.4, 5511.8) * mm, "end": v(9093.2, 5511.8) * mm});
            skLineSegment(sketch, "E64.1", {"start": v(8534.4, 6273.8) * mm, "end": v(8534.4, 5511.8) * mm});
            skLineSegment(sketch, "E64.2", {"start": v(9093.2, 6273.8) * mm, "end": v(8534.4, 6273.8) * mm});
            skLineSegment(sketch, "E64.3", {"start": v(9093.2, 5511.8) * mm, "end": v(9093.2, 6273.8) * mm});
            skLineSegment(sketch, "E65.0", {"start": v(2692.4, 6273.8) * mm, "end": v(2692.4, 5511.8) * mm});
            skLineSegment(sketch, "E65.1", {"start": v(3251.2, 6273.8) * mm, "end": v(2692.4, 6273.8) * mm});
            skLineSegment(sketch, "E65.2", {"start": v(3251.2, 5511.8) * mm, "end": v(3251.2, 6273.8) * mm});
            skLineSegment(sketch, "E65.3", {"start": v(2692.4, 5511.8) * mm, "end": v(3251.2, 5511.8) * mm});
            skSolve(sketch);
        }
        {
            var Q0;
            Q0 = qSketchRegion(id + "F40", true);
            extrude(context, id + "F41", {"entities" : qUnion([Q0]), "operationType" : NewBodyOperationType.ADD, "depth" : 76.2 * mm});
        }
        {
            var Q0;
            Q0=makeQuery(id+"F41.opExtrude","CAP_FACE",FACE,{"disambiguationData":[OSD([sQuery(id+"F40.wireOp",EDGE,"E65.0"),sQuery(id+"F40.wireOp",EDGE,"E65.1"),sQuery(id+"F40.wireOp",EDGE,"E65.2"),sQuery(id+"F40.wireOp",EDGE,"E65.3")])],"isStart":false});
            var sketch = newSketch(context, id + "F42", { "sketchPlane" : qUnion([Q0])});
            skLineSegment(sketch, "E66.0", {"start": v(2717.8, 6248.4) * mm, "end": v(2717.8, 5537.2) * mm});
            skLineSegment(sketch, "E66.1", {"start": v(3225.8, 6248.4) * mm, "end": v(2717.8, 6248.4) * mm});
            skLineSegment(sketch, "E66.2", {"start": v(3225.8, 5537.2) * mm, "end": v(3225.8, 6248.4) * mm});
            skLineSegment(sketch, "E66.3", {"start": v(2717.8, 5537.2) * mm, "end": v(3225.8, 5537.2) * mm});
            skLineSegment(sketch, "E67.0", {"start": v(8559.8, 5537.2) * mm, "end": v(9067.8, 5537.2) * mm});
            skLineSegment(sketch, "E67.1", {"start": v(8559.8, 6248.4) * mm, "end": v(8559.8, 5537.2) * mm});
            skLineSegment(sketch, "E67.2", {"start": v(9067.8, 6248.4) * mm, "end": v(8559.8, 6248.4) * mm});
            skLineSegment(sketch, "E67.3", {"start": v(9067.8, 5537.2) * mm, "end": v(9067.8, 6248.4) * mm});
            skSolve(sketch);
        }
        {
            var Q0;
            Q0 = qSketchRegion(id + "F42", true);
            extrude(context, id + "F43", {"entities" : qUnion([Q0]), "operationType" : NewBodyOperationType.ADD, "depth" : 228.6 * mm});
        }
        {
            var Q0;
            Q0=makeQuery(id+"F43.opExtrude","CAP_FACE",FACE,{"disambiguationData":[OSD([sQuery(id+"F42.wireOp",EDGE,"E66.0"),sQuery(id+"F42.wireOp",EDGE,"E66.1"),sQuery(id+"F42.wireOp",EDGE,"E66.2"),sQuery(id+"F42.wireOp",EDGE,"E66.3")])],"isStart":false});
            var sketch = newSketch(context, id + "F44", { "sketchPlane" : qUnion([Q0])});
            skLineSegment(sketch, "E68.0", {"start": v(2692.4, 6273.8) * mm, "end": v(2692.4, 5511.8) * mm});
            skLineSegment(sketch, "E68.1", {"start": v(3251.2, 6273.8) * mm, "end": v(2692.4, 6273.8) * mm});
            skLineSegment(sketch, "E68.2", {"start": v(3251.2, 5511.8) * mm, "end": v(3251.2, 6273.8) * mm});
            skLineSegment(sketch, "E68.3", {"start": v(2692.4, 5511.8) * mm, "end": v(3251.2, 5511.8) * mm});
            skLineSegment(sketch, "E69.0", {"start": v(8534.4, 5511.8) * mm, "end": v(9093.2, 5511.8) * mm});
            skLineSegment(sketch, "E69.1", {"start": v(8534.4, 6273.8) * mm, "end": v(8534.4, 5511.8) * mm});
            skLineSegment(sketch, "E69.2", {"start": v(9093.2, 6273.8) * mm, "end": v(8534.4, 6273.8) * mm});
            skLineSegment(sketch, "E69.3", {"start": v(9093.2, 5511.8) * mm, "end": v(9093.2, 6273.8) * mm});
            skSolve(sketch);
        }
        {
            var Q0;
            Q0 = qSketchRegion(id + "F44", true);
            extrude(context, id + "F45", {"entities" : qUnion([Q0]), "operationType" : NewBodyOperationType.ADD, "depth" : 76.2 * mm});
        }
        {
            var Q0;
            Q0=makeQuery(id+"F45.opExtrude","CAP_FACE",FACE,{"disambiguationData":[OSD([sQuery(id+"F44.wireOp",EDGE,"E68.0"),sQuery(id+"F44.wireOp",EDGE,"E68.1"),sQuery(id+"F44.wireOp",EDGE,"E68.2"),sQuery(id+"F44.wireOp",EDGE,"E68.3")])],"isStart":false});
            var sketch = newSketch(context, id + "F46", { "sketchPlane" : qUnion([Q0])});
            skLineSegment(sketch, "E70.0", {"start": v(2667, 6299.2) * mm, "end": v(2667, 5486.4) * mm});
            skLineSegment(sketch, "E70.1", {"start": v(3276.6, 6299.2) * mm, "end": v(2667, 6299.2) * mm});
            skLineSegment(sketch, "E70.2", {"start": v(3276.6, 5486.4) * mm, "end": v(3276.6, 6299.2) * mm});
            skLineSegment(sketch, "E70.3", {"start": v(2667, 5486.4) * mm, "end": v(3276.6, 5486.4) * mm});
            skLineSegment(sketch, "E71.0", {"start": v(8509, 5486.4) * mm, "end": v(9118.6, 5486.4) * mm});
            skLineSegment(sketch, "E71.1", {"start": v(8509, 6299.2) * mm, "end": v(8509, 5486.4) * mm});
            skLineSegment(sketch, "E71.2", {"start": v(9118.6, 6299.2) * mm, "end": v(8509, 6299.2) * mm});
            skLineSegment(sketch, "E71.3", {"start": v(9118.6, 5486.4) * mm, "end": v(9118.6, 6299.2) * mm});
            skSolve(sketch);
        }
        {
            var Q0;
            Q0 = qSketchRegion(id + "F46", true);
            extrude(context, id + "F47", {"entities" : qUnion([Q0]), "operationType" : NewBodyOperationType.ADD, "depth" : 76.2 * mm});
        }
        {
            var Q0;
            Q0=makeQuery(id+"F47.opExtrude","CAP_FACE",FACE,{"disambiguationData":[OSD([sQuery(id+"F46.wireOp",EDGE,"E70.0"),sQuery(id+"F46.wireOp",EDGE,"E70.1"),sQuery(id+"F46.wireOp",EDGE,"E70.2"),sQuery(id+"F46.wireOp",EDGE,"E70.3")])],"isStart":false});
            var sketch = newSketch(context, id + "F48", { "sketchPlane" : qUnion([Q0])});
            skLineSegment(sketch, "E72.0", {"start": v(2692.4, 6273.8) * mm, "end": v(2692.4, 5511.8) * mm});
            skLineSegment(sketch, "E72.1", {"start": v(3251.2, 6273.8) * mm, "end": v(2692.4, 6273.8) * mm});
            skLineSegment(sketch, "E72.2", {"start": v(3251.2, 5511.8) * mm, "end": v(3251.2, 6273.8) * mm});
            skLineSegment(sketch, "E72.3", {"start": v(2692.4, 5511.8) * mm, "end": v(3251.2, 5511.8) * mm});
            skLineSegment(sketch, "E73.0", {"start": v(8534.4, 5511.8) * mm, "end": v(9093.2, 5511.8) * mm});
            skLineSegment(sketch, "E73.1", {"start": v(8534.4, 6273.8) * mm, "end": v(8534.4, 5511.8) * mm});
            skLineSegment(sketch, "E73.2", {"start": v(9093.2, 6273.8) * mm, "end": v(8534.4, 6273.8) * mm});
            skLineSegment(sketch, "E73.3", {"start": v(9093.2, 5511.8) * mm, "end": v(9093.2, 6273.8) * mm});
            skSolve(sketch);
        }
        {
            var Q0;
            Q0 = qSketchRegion(id + "F48", true);
            extrude(context, id + "F49", {"entities" : qUnion([Q0]), "operationType" : NewBodyOperationType.ADD, "depth" : 76.2 * mm});
        }
        {
            var Q0;
            Q0=makeQuery(id+"F49.opExtrude","CAP_FACE",FACE,{"disambiguationData":[OSD([sQuery(id+"F48.wireOp",EDGE,"E72.0"),sQuery(id+"F48.wireOp",EDGE,"E72.1"),sQuery(id+"F48.wireOp",EDGE,"E72.2"),sQuery(id+"F48.wireOp",EDGE,"E72.3")])],"isStart":false});
            var sketch = newSketch(context, id + "F50", { "sketchPlane" : qUnion([Q0])});
            skLineSegment(sketch, "E74.0", {"start": v(2717.8, 6248.4) * mm, "end": v(2717.8, 5537.2) * mm});
            skLineSegment(sketch, "E74.1", {"start": v(3225.8, 6248.4) * mm, "end": v(2717.8, 6248.4) * mm});
            skLineSegment(sketch, "E74.2", {"start": v(3225.8, 5537.2) * mm, "end": v(3225.8, 6248.4) * mm});
            skLineSegment(sketch, "E74.3", {"start": v(2717.8, 5537.2) * mm, "end": v(3225.8, 5537.2) * mm});
            skLineSegment(sketch, "E75.0", {"start": v(8559.8, 5537.2) * mm, "end": v(9067.8, 5537.2) * mm});
            skLineSegment(sketch, "E75.1", {"start": v(8559.8, 6248.4) * mm, "end": v(8559.8, 5537.2) * mm});
            skLineSegment(sketch, "E75.2", {"start": v(9067.8, 6248.4) * mm, "end": v(8559.8, 6248.4) * mm});
            skLineSegment(sketch, "E75.3", {"start": v(9067.8, 5537.2) * mm, "end": v(9067.8, 6248.4) * mm});
            skSolve(sketch);
        }
        {
            var Q0;
            Q0 = qSketchRegion(id + "F50", true);
            extrude(context, id + "F51", {"entities" : qUnion([Q0]), "operationType" : NewBodyOperationType.ADD, "depth" : 76.2 * mm});
        }
        {
            var Q0;
            Q0=makeQuery(id+"F51.opExtrude","CAP_FACE",FACE,{"disambiguationData":[OSD([sQuery(id+"F50.wireOp",EDGE,"E74.0"),sQuery(id+"F50.wireOp",EDGE,"E74.1"),sQuery(id+"F50.wireOp",EDGE,"E74.2"),sQuery(id+"F50.wireOp",EDGE,"E74.3")])],"isStart":false});
            var sketch = newSketch(context, id + "F52", { "sketchPlane" : qUnion([Q0])});
            skLineSegment(sketch, "E76.0", {"start": v(2819.4, 6146.8) * mm, "end": v(2819.4, 5638.8) * mm});
            skLineSegment(sketch, "E76.1", {"start": v(3124.2, 6146.8) * mm, "end": v(2819.4, 6146.8) * mm});
            skLineSegment(sketch, "E76.2", {"start": v(3124.2, 5638.8) * mm, "end": v(3124.2, 6146.8) * mm});
            skLineSegment(sketch, "E76.3", {"start": v(2819.4, 5638.8) * mm, "end": v(3124.2, 5638.8) * mm});
            skLineSegment(sketch, "E77.0", {"start": v(8661.4, 5638.8) * mm, "end": v(8966.2, 5638.8) * mm});
            skLineSegment(sketch, "E77.1", {"start": v(8661.4, 6146.8) * mm, "end": v(8661.4, 5638.8) * mm});
            skLineSegment(sketch, "E77.2", {"start": v(8966.2, 6146.8) * mm, "end": v(8661.4, 6146.8) * mm});
            skLineSegment(sketch, "E77.3", {"start": v(8966.2, 5638.8) * mm, "end": v(8966.2, 6146.8) * mm});
            skSolve(sketch);
        }
        {
            var Q0;
            Q0 = qSketchRegion(id + "F52", true);
            extrude(context, id + "F53", {"entities" : qUnion([Q0]), "operationType" : NewBodyOperationType.REMOVE, "oppositeDirection" : true, "depth" : 1016 * mm});
        }
        {
            var Q0;
            Q0=makeQuery(id+"F22.opExtrude","CAP_FACE",FACE,{"disambiguationData":[OSD([sQuery(id+"F21.wireOp",EDGE,"E33"),sQuery(id+"F21.wireOp",EDGE,"E34"),sQuery(id+"F21.wireOp",EDGE,"E35"),sQuery(id+"F21.wireOp",EDGE,"E36"),sQuery(id+"F21.wireOp",EDGE,"E37")])],"isStart":false});
            var sketch = newSketch(context, id + "F54", { "sketchPlane" : qUnion([Q0])});
            skLineSegment(sketch, "E78", {"start": v(6426.2, 3962.4) * mm, "end": v(4013.2, 2832.91) * mm});
            skLineSegment(sketch, "E79", {"start": v(4013.2, 2832.91) * mm, "end": v(4023.97, 2809.9) * mm});
            skLineSegment(sketch, "E80", {"start": v(4023.97, 2809.9) * mm, "end": v(6426.2, 3934.36) * mm});
            skLineSegment(sketch, "E81", {"start": v(6426.2, 3962.4) * mm, "end": v(6426.2, 2844.8) * mm, "construction": true});
            skLineSegment(sketch, "E82.MirrorCS", {"start": v(8828.43, 2809.9) * mm, "end": v(6426.2, 3934.36) * mm});
            skLineSegment(sketch, "E83.MirrorCS", {"start": v(6426.2, 3962.4) * mm, "end": v(8839.2, 2832.91) * mm});
            skLineSegment(sketch, "E84.MirrorCS", {"start": v(8839.2, 2832.91) * mm, "end": v(8828.43, 2809.9) * mm});
            skSolve(sketch);
        }
        {
            var Q0;
            Q0 = qSketchRegion(id + "F54", true);
            var Q1;
            Q1=makeQuery(id+"F10.boolean.opBoolean","COPY",FACE,{"derivedFrom":makeQuery(id+"F10.opExtrude","CAP_FACE",FACE,{"disambiguationData":[OSD([sQuery(id+"F0.wireOp",EDGE,"E0.right"),sQuery(id+"F9.wireOp",EDGE,"E4"),sQuery(id+"F9.wireOp",EDGE,"E5"),sQuery(id+"F9.wireOp",EDGE,"E6")])],"isStart":false})});
            extrude(context, id + "F55", {"entities" : qUnion([Q0]), "operationType" : NewBodyOperationType.ADD, "depth" : 25.4 * mm, "hasSecondDirection" : true, "secondDirectionBound" : SecondDirectionBoundingType.UP_TO_SURFACE, "secondDirectionOppositeDirection" : true, "secondDirectionBoundEntityFace" : qUnion([Q1]), "secondDirectionDepth" : 25.4 * mm});
        }
        {
            var Q0;
            Q0=makeQuery(id+"F34.opExtrude","CAP_FACE",FACE,{"disambiguationData":[OSD([sQuery(id+"F33.wireOp",EDGE,"E53.bottom"),sQuery(id+"F33.wireOp",EDGE,"E53.top"),sQuery(id+"F33.wireOp",EDGE,"E53.left"),sQuery(id+"F33.wireOp",EDGE,"E53.right")])],"isStart":false});
            var sketch = newSketch(context, id + "F56", { "sketchPlane" : qUnion([Q0])});
            skLineSegment(sketch, "E85.0", {"start": v(7010.4, 2493.87) * mm, "end": v(7010.4, 1173.07) * mm});
            skLineSegment(sketch, "E85.1", {"start": v(7670.8, 2493.87) * mm, "end": v(7010.4, 2493.87) * mm});
            skLineSegment(sketch, "E85.2", {"start": v(7670.8, 1173.07) * mm, "end": v(7670.8, 2493.87) * mm});
            skLineSegment(sketch, "E85.3", {"start": v(7010.4, 1173.07) * mm, "end": v(7670.8, 1173.07) * mm});
            skSolve(sketch);
        }
        {
            var Q0;
            Q0 = qSketchRegion(id + "F56", true);
            extrude(context, id + "F57", {"entities" : qUnion([Q0]), "operationType" : NewBodyOperationType.REMOVE, "oppositeDirection" : true, "depth" : 25.4 * mm});
        }
        {
            var Q0;
            Q0=makeQuery(id+"F24.opExtrude","CAP_FACE",FACE,{"disambiguationData":[OSD([sQuery(id+"F23.wireOp",EDGE,"E39.4.0"),sQuery(id+"F23.wireOp",EDGE,"E39.4.1"),sQuery(id+"F23.wireOp",EDGE,"E39.4.2"),sQuery(id+"F23.wireOp",EDGE,"E39.4.3")])],"isStart":false});
            var sketch = newSketch(context, id + "F58", { "sketchPlane" : qUnion([Q0])});
            skLineSegment(sketch, "E86.0", {"start": v(-9728.2, 3657.6) * mm, "end": v(-9728.2, 5181.6) * mm});
            skLineSegment(sketch, "E86.1", {"start": v(-10591.8, 3657.6) * mm, "end": v(-9728.2, 3657.6) * mm});
            skLineSegment(sketch, "E86.2", {"start": v(-10591.8, 5181.6) * mm, "end": v(-10591.8, 3657.6) * mm});
            skLineSegment(sketch, "E86.3", {"start": v(-9728.2, 5181.6) * mm, "end": v(-10591.8, 5181.6) * mm});
            skLineSegment(sketch, "E87.0", {"start": v(-7899.4, 3657.6) * mm, "end": v(-7899.4, 5181.6) * mm});
            skLineSegment(sketch, "E87.1", {"start": v(-8763, 3657.6) * mm, "end": v(-7899.4, 3657.6) * mm});
            skLineSegment(sketch, "E87.2", {"start": v(-8763, 5181.6) * mm, "end": v(-8763, 3657.6) * mm});
            skLineSegment(sketch, "E87.3", {"start": v(-7899.4, 5181.6) * mm, "end": v(-8763, 5181.6) * mm});
            skLineSegment(sketch, "E88.0", {"start": v(-5461, 3657.6) * mm, "end": v(-5461, 5181.6) * mm});
            skLineSegment(sketch, "E88.1", {"start": v(-6324.6, 3657.6) * mm, "end": v(-5461, 3657.6) * mm});
            skLineSegment(sketch, "E88.2", {"start": v(-6324.6, 5181.6) * mm, "end": v(-6324.6, 3657.6) * mm});
            skLineSegment(sketch, "E88.3", {"start": v(-5461, 5181.6) * mm, "end": v(-6324.6, 5181.6) * mm});
            skLineSegment(sketch, "E89.0", {"start": v(-3022.6, 3657.6) * mm, "end": v(-3022.6, 5181.6) * mm});
            skLineSegment(sketch, "E89.1", {"start": v(-3886.2, 3657.6) * mm, "end": v(-3022.6, 3657.6) * mm});
            skLineSegment(sketch, "E89.2", {"start": v(-3886.2, 5181.6) * mm, "end": v(-3886.2, 3657.6) * mm});
            skLineSegment(sketch, "E89.3", {"start": v(-3022.6, 5181.6) * mm, "end": v(-3886.2, 5181.6) * mm});
            skLineSegment(sketch, "E90.0", {"start": v(-1193.8, 3657.6) * mm, "end": v(-1193.8, 5181.6) * mm});
            skLineSegment(sketch, "E90.1", {"start": v(-2057.4, 3657.6) * mm, "end": v(-1193.8, 3657.6) * mm});
            skLineSegment(sketch, "E90.2", {"start": v(-2057.4, 5181.6) * mm, "end": v(-2057.4, 3657.6) * mm});
            skLineSegment(sketch, "E90.3", {"start": v(-1193.8, 5181.6) * mm, "end": v(-2057.4, 5181.6) * mm});
            skLineSegment(sketch, "E91.0", {"start": v(-9728.2, 2540) * mm, "end": v(-10591.8, 2540) * mm});
            skLineSegment(sketch, "E91.1", {"start": v(-9728.2, 1016) * mm, "end": v(-9728.2, 2540) * mm});
            skLineSegment(sketch, "E91.2", {"start": v(-10591.8, 1016) * mm, "end": v(-9728.2, 1016) * mm});
            skLineSegment(sketch, "E91.3", {"start": v(-10591.8, 2540) * mm, "end": v(-10591.8, 1016) * mm});
            skLineSegment(sketch, "E92.0", {"start": v(-7899.4, 2540) * mm, "end": v(-8763, 2540) * mm});
            skLineSegment(sketch, "E92.1", {"start": v(-7899.4, 1016) * mm, "end": v(-7899.4, 2540) * mm});
            skLineSegment(sketch, "E92.2", {"start": v(-8763, 1016) * mm, "end": v(-7899.4, 1016) * mm});
            skLineSegment(sketch, "E92.3", {"start": v(-8763, 2540) * mm, "end": v(-8763, 1016) * mm});
            skLineSegment(sketch, "E93.0", {"start": v(-3022.6, 2540) * mm, "end": v(-3886.2, 2540) * mm});
            skLineSegment(sketch, "E93.1", {"start": v(-3022.6, 1016) * mm, "end": v(-3022.6, 2540) * mm});
            skLineSegment(sketch, "E93.2", {"start": v(-3886.2, 1016) * mm, "end": v(-3022.6, 1016) * mm});
            skLineSegment(sketch, "E93.3", {"start": v(-3886.2, 2540) * mm, "end": v(-3886.2, 1016) * mm});
            skLineSegment(sketch, "E94.0", {"start": v(-1193.8, 2540) * mm, "end": v(-2057.4, 2540) * mm});
            skLineSegment(sketch, "E94.1", {"start": v(-1193.8, 1016) * mm, "end": v(-1193.8, 2540) * mm});
            skLineSegment(sketch, "E94.2", {"start": v(-2057.4, 1016) * mm, "end": v(-1193.8, 1016) * mm});
            skLineSegment(sketch, "E94.3", {"start": v(-2057.4, 2540) * mm, "end": v(-2057.4, 1016) * mm});
            skSolve(sketch);
        }
        {
            var Q0;
            Q0 = qSketchRegion(id + "F58", true);
            extrude(context, id + "F59", {"entities" : qUnion([Q0]), "operationType" : NewBodyOperationType.REMOVE, "oppositeDirection" : true, "depth" : 25.4 * mm});
        }
        {
            var Q0;
            Q0=makeQuery(id+"F26.opExtrude","CAP_FACE",FACE,{"disambiguationData":[OSD([sQuery(id+"F25.wireOp",EDGE,"E40.3.0"),sQuery(id+"F25.wireOp",EDGE,"E40.3.1"),sQuery(id+"F25.wireOp",EDGE,"E40.3.2"),sQuery(id+"F25.wireOp",EDGE,"E40.3.3")])],"isStart":false});
            var sketch = newSketch(context, id + "F60", { "sketchPlane" : qUnion([Q0])});
            skLineSegment(sketch, "E95.0", {"start": v(-9728.2, 3657.6) * mm, "end": v(-9728.2, 5181.6) * mm});
            skLineSegment(sketch, "E95.1", {"start": v(-10591.8, 3657.6) * mm, "end": v(-9728.2, 3657.6) * mm});
            skLineSegment(sketch, "E95.2", {"start": v(-10591.8, 5181.6) * mm, "end": v(-10591.8, 3657.6) * mm});
            skLineSegment(sketch, "E95.3", {"start": v(-9728.2, 5181.6) * mm, "end": v(-10591.8, 5181.6) * mm});
            skLineSegment(sketch, "E96.0", {"start": v(-7899.4, 3657.6) * mm, "end": v(-7899.4, 5181.6) * mm});
            skLineSegment(sketch, "E96.1", {"start": v(-8763, 3657.6) * mm, "end": v(-7899.4, 3657.6) * mm});
            skLineSegment(sketch, "E96.2", {"start": v(-8763, 5181.6) * mm, "end": v(-8763, 3657.6) * mm});
            skLineSegment(sketch, "E96.3", {"start": v(-7899.4, 5181.6) * mm, "end": v(-8763, 5181.6) * mm});
            skLineSegment(sketch, "E97.0", {"start": v(-6273.8, 3657.6) * mm, "end": v(-6273.8, 5181.6) * mm});
            skLineSegment(sketch, "E97.1", {"start": v(-7137.4, 3657.6) * mm, "end": v(-6273.8, 3657.6) * mm});
            skLineSegment(sketch, "E97.2", {"start": v(-7137.4, 5181.6) * mm, "end": v(-7137.4, 3657.6) * mm});
            skLineSegment(sketch, "E97.3", {"start": v(-6273.8, 5181.6) * mm, "end": v(-7137.4, 5181.6) * mm});
            skLineSegment(sketch, "E98.0", {"start": v(-4648.2, 3657.6) * mm, "end": v(-4648.2, 5181.6) * mm});
            skLineSegment(sketch, "E98.1", {"start": v(-5511.8, 3657.6) * mm, "end": v(-4648.2, 3657.6) * mm});
            skLineSegment(sketch, "E98.2", {"start": v(-5511.8, 5181.6) * mm, "end": v(-5511.8, 3657.6) * mm});
            skLineSegment(sketch, "E98.3", {"start": v(-4648.2, 5181.6) * mm, "end": v(-5511.8, 5181.6) * mm});
            skLineSegment(sketch, "E99.0", {"start": v(-3022.6, 3657.6) * mm, "end": v(-3022.6, 5181.6) * mm});
            skLineSegment(sketch, "E99.1", {"start": v(-3886.2, 3657.6) * mm, "end": v(-3022.6, 3657.6) * mm});
            skLineSegment(sketch, "E99.2", {"start": v(-3886.2, 5181.6) * mm, "end": v(-3886.2, 3657.6) * mm});
            skLineSegment(sketch, "E99.3", {"start": v(-3022.6, 5181.6) * mm, "end": v(-3886.2, 5181.6) * mm});
            skLineSegment(sketch, "E100.0", {"start": v(-1193.8, 3657.6) * mm, "end": v(-1193.8, 5181.6) * mm});
            skLineSegment(sketch, "E100.1", {"start": v(-2057.4, 3657.6) * mm, "end": v(-1193.8, 3657.6) * mm});
            skLineSegment(sketch, "E100.2", {"start": v(-2057.4, 5181.6) * mm, "end": v(-2057.4, 3657.6) * mm});
            skLineSegment(sketch, "E100.3", {"start": v(-1193.8, 5181.6) * mm, "end": v(-2057.4, 5181.6) * mm});
            skLineSegment(sketch, "E101.0", {"start": v(-1193.8, 2540) * mm, "end": v(-2057.4, 2540) * mm});
            skLineSegment(sketch, "E101.1", {"start": v(-1193.8, 1016) * mm, "end": v(-1193.8, 2540) * mm});
            skLineSegment(sketch, "E101.2", {"start": v(-2057.4, 1016) * mm, "end": v(-1193.8, 1016) * mm});
            skLineSegment(sketch, "E101.3", {"start": v(-2057.4, 2540) * mm, "end": v(-2057.4, 1016) * mm});
            skLineSegment(sketch, "E102.0", {"start": v(-3886.2, 2540) * mm, "end": v(-3886.2, 1016) * mm});
            skLineSegment(sketch, "E102.1", {"start": v(-3022.6, 2540) * mm, "end": v(-3886.2, 2540) * mm});
            skLineSegment(sketch, "E102.2", {"start": v(-3022.6, 1016) * mm, "end": v(-3022.6, 2540) * mm});
            skLineSegment(sketch, "E102.3", {"start": v(-3886.2, 1016) * mm, "end": v(-3022.6, 1016) * mm});
            skLineSegment(sketch, "E103.0", {"start": v(-8763, 2540) * mm, "end": v(-8763, 1016) * mm});
            skLineSegment(sketch, "E103.1", {"start": v(-7899.4, 2540) * mm, "end": v(-8763, 2540) * mm});
            skLineSegment(sketch, "E103.2", {"start": v(-7899.4, 1016) * mm, "end": v(-7899.4, 2540) * mm});
            skLineSegment(sketch, "E103.3", {"start": v(-8763, 1016) * mm, "end": v(-7899.4, 1016) * mm});
            skLineSegment(sketch, "E104.0", {"start": v(-10591.8, 2540) * mm, "end": v(-10591.8, 1016) * mm});
            skLineSegment(sketch, "E104.1", {"start": v(-9728.2, 2540) * mm, "end": v(-10591.8, 2540) * mm});
            skLineSegment(sketch, "E104.2", {"start": v(-9728.2, 1016) * mm, "end": v(-9728.2, 2540) * mm});
            skLineSegment(sketch, "E104.3", {"start": v(-10591.8, 1016) * mm, "end": v(-9728.2, 1016) * mm});
            skSolve(sketch);
        }
        {
            var Q0;
            Q0 = qSketchRegion(id + "F60", true);
            extrude(context, id + "F61", {"entities" : qUnion([Q0]), "operationType" : NewBodyOperationType.REMOVE, "oppositeDirection" : true, "depth" : 25.4 * mm});
        }
        {
            var Q0;
            Q0=makeQuery(id+"F18.opExtrude","CAP_FACE",FACE,{"disambiguationData":[OSD([sQuery(id+"F17.wireOp",EDGE,"E17.bottom"),sQuery(id+"F17.wireOp",EDGE,"E17.top"),sQuery(id+"F17.wireOp",EDGE,"E17.left"),sQuery(id+"F17.wireOp",EDGE,"E17.right")])],"isStart":false});
            var sketch = newSketch(context, id + "F62", { "sketchPlane" : qUnion([Q0])});
            skLineSegment(sketch, "E105.0", {"start": v(2057.4, 3657.6) * mm, "end": v(2057.4, 5181.6) * mm});
            skLineSegment(sketch, "E105.1", {"start": v(1193.8, 3657.6) * mm, "end": v(2057.4, 3657.6) * mm});
            skLineSegment(sketch, "E105.2", {"start": v(1193.8, 5181.6) * mm, "end": v(1193.8, 3657.6) * mm});
            skLineSegment(sketch, "E105.3", {"start": v(2057.4, 5181.6) * mm, "end": v(1193.8, 5181.6) * mm});
            skLineSegment(sketch, "E106.0", {"start": v(3886.2, 3657.6) * mm, "end": v(3886.2, 5181.6) * mm});
            skLineSegment(sketch, "E106.1", {"start": v(3022.6, 3657.6) * mm, "end": v(3886.2, 3657.6) * mm});
            skLineSegment(sketch, "E106.2", {"start": v(3022.6, 5181.6) * mm, "end": v(3022.6, 3657.6) * mm});
            skLineSegment(sketch, "E106.3", {"start": v(3886.2, 5181.6) * mm, "end": v(3022.6, 5181.6) * mm});
            skLineSegment(sketch, "E107.0", {"start": v(6324.6, 3657.6) * mm, "end": v(6324.6, 5181.6) * mm});
            skLineSegment(sketch, "E107.1", {"start": v(5461, 3657.6) * mm, "end": v(6324.6, 3657.6) * mm});
            skLineSegment(sketch, "E107.2", {"start": v(5461, 5181.6) * mm, "end": v(5461, 3657.6) * mm});
            skLineSegment(sketch, "E107.3", {"start": v(6324.6, 5181.6) * mm, "end": v(5461, 5181.6) * mm});
            skLineSegment(sketch, "E108.0", {"start": v(8763, 3657.6) * mm, "end": v(8763, 5181.6) * mm});
            skLineSegment(sketch, "E108.1", {"start": v(7899.4, 3657.6) * mm, "end": v(8763, 3657.6) * mm});
            skLineSegment(sketch, "E108.2", {"start": v(7899.4, 5181.6) * mm, "end": v(7899.4, 3657.6) * mm});
            skLineSegment(sketch, "E108.3", {"start": v(8763, 5181.6) * mm, "end": v(7899.4, 5181.6) * mm});
            skLineSegment(sketch, "E109.0", {"start": v(10591.8, 3657.6) * mm, "end": v(10591.8, 5181.6) * mm});
            skLineSegment(sketch, "E109.1", {"start": v(9728.2, 3657.6) * mm, "end": v(10591.8, 3657.6) * mm});
            skLineSegment(sketch, "E109.2", {"start": v(9728.2, 5181.6) * mm, "end": v(9728.2, 3657.6) * mm});
            skLineSegment(sketch, "E109.3", {"start": v(10591.8, 5181.6) * mm, "end": v(9728.2, 5181.6) * mm});
            skLineSegment(sketch, "E110.0", {"start": v(9728.2, 2540) * mm, "end": v(9728.2, 1016) * mm});
            skLineSegment(sketch, "E110.1", {"start": v(10591.8, 2540) * mm, "end": v(9728.2, 2540) * mm});
            skLineSegment(sketch, "E110.2", {"start": v(10591.8, 1016) * mm, "end": v(10591.8, 2540) * mm});
            skLineSegment(sketch, "E110.3", {"start": v(9728.2, 1016) * mm, "end": v(10591.8, 1016) * mm});
            skLineSegment(sketch, "E111.0", {"start": v(7899.4, 2540) * mm, "end": v(7899.4, 1016) * mm});
            skLineSegment(sketch, "E111.1", {"start": v(8763, 2540) * mm, "end": v(7899.4, 2540) * mm});
            skLineSegment(sketch, "E111.2", {"start": v(8763, 1016) * mm, "end": v(8763, 2540) * mm});
            skLineSegment(sketch, "E111.3", {"start": v(7899.4, 1016) * mm, "end": v(8763, 1016) * mm});
            skLineSegment(sketch, "E112.0", {"start": v(3022.6, 2540) * mm, "end": v(3022.6, 1016) * mm});
            skLineSegment(sketch, "E112.1", {"start": v(3886.2, 2540) * mm, "end": v(3022.6, 2540) * mm});
            skLineSegment(sketch, "E112.2", {"start": v(3886.2, 1016) * mm, "end": v(3886.2, 2540) * mm});
            skLineSegment(sketch, "E112.3", {"start": v(3022.6, 1016) * mm, "end": v(3886.2, 1016) * mm});
            skLineSegment(sketch, "E113.0", {"start": v(1193.8, 2540) * mm, "end": v(1193.8, 1016) * mm});
            skLineSegment(sketch, "E113.1", {"start": v(2057.4, 2540) * mm, "end": v(1193.8, 2540) * mm});
            skLineSegment(sketch, "E113.2", {"start": v(2057.4, 1016) * mm, "end": v(2057.4, 2540) * mm});
            skLineSegment(sketch, "E113.3", {"start": v(1193.8, 1016) * mm, "end": v(2057.4, 1016) * mm});
            skSolve(sketch);
        }
        {
            var Q0;
            Q0 = qSketchRegion(id + "F62", true);
            extrude(context, id + "F63", {"entities" : qUnion([Q0]), "operationType" : NewBodyOperationType.REMOVE, "oppositeDirection" : true, "depth" : 25.4 * mm});
        }
        {
            var Q0;
            Q0=makeQuery(id+"F18.opExtrude","CAP_FACE",FACE,{"disambiguationData":[OSD([sQuery(id+"F17.wireOp",EDGE,"E22.bottom"),sQuery(id+"F17.wireOp",EDGE,"E22.top"),sQuery(id+"F17.wireOp",EDGE,"E22.left"),sQuery(id+"F17.wireOp",EDGE,"E22.right")])],"isStart":false});
            var sketch = newSketch(context, id + "F64", { "sketchPlane" : qUnion([Q0])});
            skLineSegment(sketch, "E114.bottom", {"start": v(5054.6, 2489.2) * mm, "end": v(5334, 2489.2) * mm});
            skLineSegment(sketch, "E114.top", {"start": v(5054.6, 203.2) * mm, "end": v(5334, 203.2) * mm});
            skLineSegment(sketch, "E114.left", {"start": v(5054.6, 2489.2) * mm, "end": v(5054.6, 203.2) * mm});
            skLineSegment(sketch, "E114.right", {"start": v(5334, 2489.2) * mm, "end": v(5334, 203.2) * mm});
            skLineSegment(sketch, "E115.bottom", {"start": v(5435.6, 2489.2) * mm, "end": v(6350, 2489.2) * mm});
            skLineSegment(sketch, "E115.top", {"start": v(5435.6, 203.2) * mm, "end": v(6350, 203.2) * mm});
            skLineSegment(sketch, "E115.left", {"start": v(5435.6, 2489.2) * mm, "end": v(5435.6, 203.2) * mm});
            skLineSegment(sketch, "E115.right", {"start": v(6350, 2489.2) * mm, "end": v(6350, 203.2) * mm});
            skLineSegment(sketch, "E116.bottom", {"start": v(6451.6, 2489.2) * mm, "end": v(6731, 2489.2) * mm});
            skLineSegment(sketch, "E116.top", {"start": v(6451.6, 203.2) * mm, "end": v(6731, 203.2) * mm});
            skLineSegment(sketch, "E116.left", {"start": v(6451.6, 2489.2) * mm, "end": v(6451.6, 203.2) * mm});
            skLineSegment(sketch, "E116.right", {"start": v(6731, 2489.2) * mm, "end": v(6731, 203.2) * mm});
            skSolve(sketch);
        }
        {
            var Q0;
            Q0 = qSketchRegion(id + "F64", true);
            extrude(context, id + "F65", {"entities" : qUnion([Q0]), "operationType" : NewBodyOperationType.REMOVE, "oppositeDirection" : true, "depth" : 50.8 * mm});
        }
        {
            var Q0;
            Q0=makeQuery(id+"F24.opExtrude","CAP_FACE",FACE,{"disambiguationData":[OSD([sQuery(id+"F23.wireOp",EDGE,"E39.7.0"),sQuery(id+"F23.wireOp",EDGE,"E39.7.1"),sQuery(id+"F23.wireOp",EDGE,"E39.7.2"),sQuery(id+"F23.wireOp",EDGE,"E39.7.3")])],"isStart":false});
            var sketch = newSketch(context, id + "F66", { "sketchPlane" : qUnion([Q0])});
            skLineSegment(sketch, "E117.0.0", {"start": v(-5054.6, 2489.2) * mm, "end": v(-5054.6, 203.2) * mm});
            skLineSegment(sketch, "E117.0.1", {"start": v(-5054.6, 203.2) * mm, "end": v(-5334, 203.2) * mm});
            skLineSegment(sketch, "E117.0.2", {"start": v(-5334, 203.2) * mm, "end": v(-5334, 2489.2) * mm});
            skLineSegment(sketch, "E117.0.3", {"start": v(-5334, 2489.2) * mm, "end": v(-5054.6, 2489.2) * mm});
            skLineSegment(sketch, "E117.1.0", {"start": v(-5435.6, 2489.2) * mm, "end": v(-5435.6, 203.2) * mm});
            skLineSegment(sketch, "E117.1.1", {"start": v(-5435.6, 203.2) * mm, "end": v(-6350, 203.2) * mm});
            skLineSegment(sketch, "E117.1.2", {"start": v(-6350, 203.2) * mm, "end": v(-6350, 2489.2) * mm});
            skLineSegment(sketch, "E117.1.3", {"start": v(-6350, 2489.2) * mm, "end": v(-5435.6, 2489.2) * mm});
            skLineSegment(sketch, "E117.2.0", {"start": v(-6451.6, 2489.2) * mm, "end": v(-6451.6, 203.2) * mm});
            skLineSegment(sketch, "E117.2.1", {"start": v(-6451.6, 203.2) * mm, "end": v(-6731, 203.2) * mm});
            skLineSegment(sketch, "E117.2.2", {"start": v(-6731, 203.2) * mm, "end": v(-6731, 2489.2) * mm});
            skLineSegment(sketch, "E117.2.3", {"start": v(-6731, 2489.2) * mm, "end": v(-6451.6, 2489.2) * mm});
            skSolve(sketch);
        }
        {
            var Q0;
            Q0 = qSketchRegion(id + "F66", true);
            extrude(context, id + "F67", {"entities" : qUnion([Q0]), "operationType" : NewBodyOperationType.REMOVE, "oppositeDirection" : true, "depth" : 50.8 * mm});
        }
        {
            var Q0;
            Q0=makeQuery(id+"F20.opExtrude","CAP_FACE",FACE,{"disambiguationData":[OSD([sQuery(id+"F19.wireOp",EDGE,"E30.bottom"),sQuery(id+"F19.wireOp",EDGE,"E30.top"),sQuery(id+"F19.wireOp",EDGE,"E30.left"),sQuery(id+"F19.wireOp",EDGE,"E30.right")])],"isStart":false});
            var sketch = newSketch(context, id + "F68", { "sketchPlane" : qUnion([Q0])});
            skLineSegment(sketch, "E118.0", {"start": v(3886.2, 101.6) * mm, "end": v(3886.2, 2362.2) * mm});
            skLineSegment(sketch, "E118.1", {"start": v(3022.6, 101.6) * mm, "end": v(3886.2, 101.6) * mm});
            skLineSegment(sketch, "E118.2", {"start": v(3022.6, 2362.2) * mm, "end": v(3022.6, 101.6) * mm});
            skLineSegment(sketch, "E118.3", {"start": v(3886.2, 2362.2) * mm, "end": v(3022.6, 2362.2) * mm});
            skSolve(sketch);
        }
        {
            var Q0;
            Q0 = qSketchRegion(id + "F68", true);
            extrude(context, id + "F69", {"entities" : qUnion([Q0]), "operationType" : NewBodyOperationType.REMOVE, "oppositeDirection" : true, "depth" : 25.4 * mm});
        }
        {
            var Q0;
            Q0=makeQuery(id+"F30.opExtrude","CAP_FACE",FACE,{"disambiguationData":[OSD([sQuery(id+"F29.wireOp",EDGE,"E50.bottom"),sQuery(id+"F29.wireOp",EDGE,"E50.top"),sQuery(id+"F29.wireOp",EDGE,"E50.left"),sQuery(id+"F29.wireOp",EDGE,"E50.right")])],"isStart":false});
            var sketch = newSketch(context, id + "F70", { "sketchPlane" : qUnion([Q0])});
            skLineSegment(sketch, "E119.0", {"start": v(13563.6, 101.6) * mm, "end": v(13563.6, 2387.6) * mm});
            skLineSegment(sketch, "E119.1", {"start": v(12801.6, 101.6) * mm, "end": v(13563.6, 101.6) * mm});
            skLineSegment(sketch, "E119.2", {"start": v(12801.6, 2387.6) * mm, "end": v(12801.6, 101.6) * mm});
            skLineSegment(sketch, "E119.3", {"start": v(13563.6, 2387.6) * mm, "end": v(12801.6, 2387.6) * mm});
            skLineSegment(sketch, "E120.0", {"start": v(14147.8, 2438.4) * mm, "end": v(14147.8, 1117.6) * mm});
            skLineSegment(sketch, "E120.1", {"start": v(14833.6, 2438.4) * mm, "end": v(14147.8, 2438.4) * mm});
            skLineSegment(sketch, "E120.2", {"start": v(14833.6, 1117.6) * mm, "end": v(14833.6, 2438.4) * mm});
            skLineSegment(sketch, "E120.3", {"start": v(14147.8, 1117.6) * mm, "end": v(14833.6, 1117.6) * mm});
            skSolve(sketch);
        }
        {
            var Q0;
            Q0 = qSketchRegion(id + "F70", true);
            extrude(context, id + "F71", {"entities" : qUnion([Q0]), "operationType" : NewBodyOperationType.REMOVE, "oppositeDirection" : true, "depth" : 25.4 * mm});
        }
        {
            var Q0;
            Q0=makeQuery(id+"F20.opExtrude","CAP_FACE",FACE,{"disambiguationData":[OSD([sQuery(id+"F19.wireOp",EDGE,"E29.bottom"),sQuery(id+"F19.wireOp",EDGE,"E29.top"),sQuery(id+"F19.wireOp",EDGE,"E29.left"),sQuery(id+"F19.wireOp",EDGE,"E29.right")])],"isStart":false});
            var sketch = newSketch(context, id + "F72", { "sketchPlane" : qUnion([Q0])});
            skLineSegment(sketch, "E121.0", {"start": v(1193.8, 2540) * mm, "end": v(1193.8, 1016) * mm});
            skLineSegment(sketch, "E121.1", {"start": v(2057.4, 2540) * mm, "end": v(1193.8, 2540) * mm});
            skLineSegment(sketch, "E121.2", {"start": v(2057.4, 1016) * mm, "end": v(2057.4, 2540) * mm});
            skLineSegment(sketch, "E121.3", {"start": v(1193.8, 1016) * mm, "end": v(2057.4, 1016) * mm});
            skLineSegment(sketch, "E122.0", {"start": v(2057.4, 3657.6) * mm, "end": v(2057.4, 5181.6) * mm});
            skLineSegment(sketch, "E122.1", {"start": v(1193.8, 3657.6) * mm, "end": v(2057.4, 3657.6) * mm});
            skLineSegment(sketch, "E122.2", {"start": v(1193.8, 5181.6) * mm, "end": v(1193.8, 3657.6) * mm});
            skLineSegment(sketch, "E122.3", {"start": v(2057.4, 5181.6) * mm, "end": v(1193.8, 5181.6) * mm});
            skLineSegment(sketch, "E123.0", {"start": v(3886.2, 3657.6) * mm, "end": v(3886.2, 5181.6) * mm});
            skLineSegment(sketch, "E123.1", {"start": v(3022.6, 3657.6) * mm, "end": v(3886.2, 3657.6) * mm});
            skLineSegment(sketch, "E123.2", {"start": v(3022.6, 5181.6) * mm, "end": v(3022.6, 3657.6) * mm});
            skLineSegment(sketch, "E123.3", {"start": v(3886.2, 5181.6) * mm, "end": v(3022.6, 5181.6) * mm});
            skLineSegment(sketch, "E124.0", {"start": v(6324.6, 4114.8) * mm, "end": v(6324.6, 5181.6) * mm});
            skLineSegment(sketch, "E124.1", {"start": v(5461, 4114.8) * mm, "end": v(6324.6, 4114.8) * mm});
            skLineSegment(sketch, "E124.2", {"start": v(5461, 5181.6) * mm, "end": v(5461, 4114.8) * mm});
            skLineSegment(sketch, "E124.3", {"start": v(6324.6, 5181.6) * mm, "end": v(5461, 5181.6) * mm});
            skLineSegment(sketch, "E125.0", {"start": v(8763, 3657.6) * mm, "end": v(8763, 5181.6) * mm});
            skLineSegment(sketch, "E125.1", {"start": v(7899.4, 3657.6) * mm, "end": v(8763, 3657.6) * mm});
            skLineSegment(sketch, "E125.2", {"start": v(7899.4, 5181.6) * mm, "end": v(7899.4, 3657.6) * mm});
            skLineSegment(sketch, "E125.3", {"start": v(8763, 5181.6) * mm, "end": v(7899.4, 5181.6) * mm});
            skLineSegment(sketch, "E126.0", {"start": v(10591.8, 3657.6) * mm, "end": v(10591.8, 5181.6) * mm});
            skLineSegment(sketch, "E126.1", {"start": v(9728.2, 3657.6) * mm, "end": v(10591.8, 3657.6) * mm});
            skLineSegment(sketch, "E126.2", {"start": v(9728.2, 5181.6) * mm, "end": v(9728.2, 3657.6) * mm});
            skLineSegment(sketch, "E126.3", {"start": v(10591.8, 5181.6) * mm, "end": v(9728.2, 5181.6) * mm});
            skSolve(sketch);
        }
        {
            var Q0;
            Q0 = qSketchRegion(id + "F72", true);
            extrude(context, id + "F73", {"entities" : qUnion([Q0]), "operationType" : NewBodyOperationType.REMOVE, "oppositeDirection" : true, "depth" : 25.4 * mm});
        }
        {
            var Q0;
            Q0=makeQuery(id+"F65.boolean.opBoolean","COPY",FACE,{"derivedFrom":makeQuery(id+"F65.opExtrude","CAP_FACE",FACE,{"disambiguationData":[OSD([sQuery(id+"F64.wireOp",EDGE,"E115.bottom"),sQuery(id+"F64.wireOp",EDGE,"E115.top"),sQuery(id+"F64.wireOp",EDGE,"E115.left"),sQuery(id+"F64.wireOp",EDGE,"E115.right")])],"isStart":false})});
            extrude(context, id + "F74", {"entities" : qUnion([Q0]), "operationType" : NewBodyOperationType.REMOVE, "oppositeDirection" : true, "depth" : 254 * mm});
        }
        {
            var Q0;
            Q0=makeQuery(id+"F67.boolean.opBoolean","COPY",FACE,{"derivedFrom":makeQuery(id+"F67.opExtrude","CAP_FACE",FACE,{"disambiguationData":[OSD([sQuery(id+"F66.wireOp",EDGE,"E117.1.0"),sQuery(id+"F66.wireOp",EDGE,"E117.1.1"),sQuery(id+"F66.wireOp",EDGE,"E117.1.2"),sQuery(id+"F66.wireOp",EDGE,"E117.1.3")])],"isStart":false})});
            extrude(context, id + "F75", {"entities" : qUnion([Q0]), "operationType" : NewBodyOperationType.REMOVE, "oppositeDirection" : true, "depth" : 254 * mm});
        }
        {
            var Q0;
            Q0=makeQuery(id+"F30.boolean.opBoolean","MERGE",FACE,{"derivedFrom":[makeQuery(id+"F26.boolean.opBoolean","MERGE",FACE,{"derivedFrom":[makeQuery(id+"F24.boolean.opBoolean","MERGE",FACE,{"derivedFrom":[makeQuery(id+"F22.boolean.opBoolean","MERGE",FACE,{"derivedFrom":[makeQuery(id+"F20.boolean.opBoolean","MERGE",FACE,{"derivedFrom":[makeQuery(id+"F18.boolean.opBoolean","MERGE",FACE,{"derivedFrom":[makeQuery(id+"F1.opExtrude","CAP_FACE",FACE,{"disambiguationData":[OSD([sQuery(id+"F0.wireOp",EDGE,"E0.bottom"),sQuery(id+"F0.wireOp",EDGE,"E0.top"),sQuery(id+"F0.wireOp",EDGE,"E0.left"),sQuery(id+"F0.wireOp",EDGE,"E0.right")])],"isStart":true}),makeQuery(id+"F18.opExtrude","SWEPT_FACE",FACE,{"disambiguationData":[OSD([sQuery(id+"F17.wireOp",EDGE,"E22.top")])]})]}),makeQuery(id+"F20.opExtrude","SWEPT_FACE",FACE,{"disambiguationData":[OSD([sQuery(id+"F19.wireOp",EDGE,"E30.top")])]})]}),makeQuery(id+"F22.opExtrude","SWEPT_FACE",FACE,{"disambiguationData":[OSD([sQuery(id+"F21.wireOp",EDGE,"E37")])]})]}),makeQuery(id+"F24.opExtrude","SWEPT_FACE",FACE,{"disambiguationData":[OSD([sQuery(id+"F23.wireOp",EDGE,"E39.7.3")])]})]}),makeQuery(id+"F26.opExtrude","SWEPT_FACE",FACE,{"disambiguationData":[OSD([sQuery(id+"F25.wireOp",EDGE,"E46.top")])]})]}),makeQuery(id+"F30.opExtrude","SWEPT_FACE",FACE,{"disambiguationData":[OSD([sQuery(id+"F29.wireOp",EDGE,"E50.top")])]})]});
            var sketch = newSketch(context, id + "F76", { "sketchPlane" : qUnion([Q0])});
            skLineSegment(sketch, "E127.bottom", {"start": v(11709.4, -11709.4) * mm, "end": v(76.2, -11709.4) * mm});
            skLineSegment(sketch, "E127.top", {"start": v(11709.4, -76.2) * mm, "end": v(76.2, -76.2) * mm});
            skLineSegment(sketch, "E127.left", {"start": v(11709.4, -11709.4) * mm, "end": v(11709.4, -76.2) * mm});
            skLineSegment(sketch, "E127.right", {"start": v(76.2, -11709.4) * mm, "end": v(76.2, -76.2) * mm});
            skSolve(sketch);
        }
        {
            var Q0;
            Q0 = qSketchRegion(id + "F76", true);
            extrude(context, id + "F77", {"entities" : qUnion([Q0]), "operationType" : NewBodyOperationType.ADD, "oppositeDirection" : true, "depth" : 101.6 * mm, "hasSecondDirection" : true, "secondDirectionOppositeDirection" : false, "secondDirectionDepth" : 1778 * mm});
        }
        {
            var Q0;
            Q0=makeQuery(id+"F30.boolean.opBoolean","MERGE",FACE,{"derivedFrom":[makeQuery(id+"F26.boolean.opBoolean","MERGE",FACE,{"derivedFrom":[makeQuery(id+"F24.boolean.opBoolean","MERGE",FACE,{"derivedFrom":[makeQuery(id+"F22.boolean.opBoolean","MERGE",FACE,{"derivedFrom":[makeQuery(id+"F20.boolean.opBoolean","MERGE",FACE,{"derivedFrom":[makeQuery(id+"F18.boolean.opBoolean","MERGE",FACE,{"derivedFrom":[makeQuery(id+"F1.opExtrude","CAP_FACE",FACE,{"disambiguationData":[OSD([sQuery(id+"F0.wireOp",EDGE,"E0.bottom"),sQuery(id+"F0.wireOp",EDGE,"E0.top"),sQuery(id+"F0.wireOp",EDGE,"E0.left"),sQuery(id+"F0.wireOp",EDGE,"E0.right")])],"isStart":true}),makeQuery(id+"F18.opExtrude","SWEPT_FACE",FACE,{"disambiguationData":[OSD([sQuery(id+"F17.wireOp",EDGE,"E22.top")])]})]}),makeQuery(id+"F20.opExtrude","SWEPT_FACE",FACE,{"disambiguationData":[OSD([sQuery(id+"F19.wireOp",EDGE,"E30.top")])]})]}),makeQuery(id+"F22.opExtrude","SWEPT_FACE",FACE,{"disambiguationData":[OSD([sQuery(id+"F21.wireOp",EDGE,"E37")])]})]}),makeQuery(id+"F24.opExtrude","SWEPT_FACE",FACE,{"disambiguationData":[OSD([sQuery(id+"F23.wireOp",EDGE,"E39.7.3")])]})]}),makeQuery(id+"F26.opExtrude","SWEPT_FACE",FACE,{"disambiguationData":[OSD([sQuery(id+"F25.wireOp",EDGE,"E46.top")])]})]}),makeQuery(id+"F30.opExtrude","SWEPT_FACE",FACE,{"disambiguationData":[OSD([sQuery(id+"F29.wireOp",EDGE,"E50.top")])]})]});
            var sketch = newSketch(context, id + "F78", { "sketchPlane" : qUnion([Q0])});
            skLineSegment(sketch, "E128.bottom", {"start": v(18846.8, -8737.6) * mm, "end": v(11709.4, -8737.6) * mm});
            skLineSegment(sketch, "E128.top", {"start": v(18846.8, -4114.8) * mm, "end": v(11709.4, -4114.8) * mm});
            skLineSegment(sketch, "E128.left", {"start": v(18846.8, -8737.6) * mm, "end": v(18846.8, -4114.8) * mm});
            skLineSegment(sketch, "E128.right", {"start": v(11709.4, -8737.6) * mm, "end": v(11709.4, -4114.8) * mm});
            skSolve(sketch);
        }
        {
            var Q0;
            Q0 = qSketchRegion(id + "F78", true);
            var Q1;
            Q1=makeQuery(id+"F77.opExtrude","CAP_FACE",FACE,{"disambiguationData":[OSD([sQuery(id+"F76.wireOp",EDGE,"E127.bottom"),sQuery(id+"F76.wireOp",EDGE,"E127.top"),sQuery(id+"F76.wireOp",EDGE,"E127.left"),sQuery(id+"F76.wireOp",EDGE,"E127.right")])],"isStart":true});
            extrude(context, id + "F79", {"entities" : qUnion([Q0]), "operationType" : NewBodyOperationType.ADD, "endBound" : BoundingType.UP_TO_SURFACE, "endBoundEntityFace" : qUnion([Q1]), "depth" : 25.4 * mm, "hasSecondDirection" : true, "secondDirectionOppositeDirection" : true, "secondDirectionDepth" : 101.6 * mm});
        }
        {
            var Q0;
            {var subQ2=sQuery(id+"F21.wireOp",EDGE,"E37");var subQ3=sQuery(id+"F0.wireOp",EDGE,"E0.top");var subQ6=sQuery(id+"F29.wireOp",EDGE,"E50.top");var subQ17=sQuery(id+"F25.wireOp",EDGE,"E46.top");var subQ18=sQuery(id+"F19.wireOp",EDGE,"E30.top");var subQ19=sQuery(id+"F23.wireOp",EDGE,"E39.7.3");var subQ27=sQuery(id+"F0.wireOp",EDGE,"E0.right");var subQ31=sQuery(id+"F0.wireOp",EDGE,"E0.bottom");var subQ32=sQuery(id+"F0.wireOp",EDGE,"E0.left");var subQ36=sQuery(id+"F17.wireOp",EDGE,"E22.top");Q0=makeQuery(id+"F79.boolean.opBoolean","SPLIT",FACE,{"disambiguationData":[TD([makeQuery(id+"F1.opExtrude","SWEPT_FACE",FACE,{"disambiguationData":[OSD([subQ31])]})])],"derivedFrom":makeQuery(id+"F30.boolean.opBoolean","MERGE",FACE,{"derivedFrom":[makeQuery(id+"F26.boolean.opBoolean","MERGE",FACE,{"derivedFrom":[makeQuery(id+"F24.boolean.opBoolean","MERGE",FACE,{"derivedFrom":[makeQuery(id+"F22.boolean.opBoolean","MERGE",FACE,{"derivedFrom":[makeQuery(id+"F20.boolean.opBoolean","MERGE",FACE,{"derivedFrom":[makeQuery(id+"F18.boolean.opBoolean","MERGE",FACE,{"derivedFrom":[makeQuery(id+"F1.opExtrude","CAP_FACE",FACE,{"disambiguationData":[OSD([subQ31,subQ3,subQ32,subQ27])],"isStart":true}),makeQuery(id+"F18.opExtrude","SWEPT_FACE",FACE,{"disambiguationData":[OSD([subQ36])]})]}),makeQuery(id+"F20.opExtrude","SWEPT_FACE",FACE,{"disambiguationData":[OSD([subQ18])]})]}),makeQuery(id+"F22.opExtrude","SWEPT_FACE",FACE,{"disambiguationData":[OSD([subQ2])]})]}),makeQuery(id+"F24.opExtrude","SWEPT_FACE",FACE,{"disambiguationData":[OSD([subQ19])]})]}),makeQuery(id+"F26.opExtrude","SWEPT_FACE",FACE,{"disambiguationData":[OSD([subQ17])]})]}),makeQuery(id+"F30.opExtrude","SWEPT_FACE",FACE,{"disambiguationData":[OSD([subQ6])]})]})});}
            var sketch = newSketch(context, id + "F80", { "sketchPlane" : qUnion([Q0])});
            skLineSegment(sketch, "E129.bottom", {"start": v(5029.2, -11760.2) * mm, "end": v(6731, -11760.2) * mm});
            skLineSegment(sketch, "E129.top", {"start": v(5029.2, -12522.2) * mm, "end": v(6731, -12522.2) * mm});
            skLineSegment(sketch, "E129.left", {"start": v(5029.2, -11760.2) * mm, "end": v(5029.2, -12522.2) * mm});
            skLineSegment(sketch, "E129.right", {"start": v(6731, -11760.2) * mm, "end": v(6731, -12522.2) * mm});
            skSolve(sketch);
        }
        {
            var Q0;
            Q0 = qSketchRegion(id + "F80", true);
            extrude(context, id + "F81", {"entities" : qUnion([Q0]), "operationType" : NewBodyOperationType.ADD, "depth" : 203.2 * mm});
        }
        {
            var Q0;
            Q0=makeQuery(id+"F81.opExtrude","CAP_FACE",FACE,{"disambiguationData":[OSD([sQuery(id+"F80.wireOp",EDGE,"E129.bottom"),sQuery(id+"F80.wireOp",EDGE,"E129.top"),sQuery(id+"F80.wireOp",EDGE,"E129.left"),sQuery(id+"F80.wireOp",EDGE,"E129.right")])],"isStart":false});
            var sketch = newSketch(context, id + "F82", { "sketchPlane" : qUnion([Q0])});
            skLineSegment(sketch, "E130.bottom", {"start": v(5029.2, -11760.2) * mm, "end": v(6731, -11760.2) * mm});
            skLineSegment(sketch, "E130.top", {"start": v(5029.2, -12776.2) * mm, "end": v(6731, -12776.2) * mm});
            skLineSegment(sketch, "E130.left", {"start": v(5029.2, -11760.2) * mm, "end": v(5029.2, -12776.2) * mm});
            skLineSegment(sketch, "E130.right", {"start": v(6731, -11760.2) * mm, "end": v(6731, -12776.2) * mm});
            skSolve(sketch);
        }
        {
            var Q0;
            Q0 = qSketchRegion(id + "F82", true);
            extrude(context, id + "F83", {"entities" : qUnion([Q0]), "operationType" : NewBodyOperationType.ADD, "depth" : 203.2 * mm});
        }
        {
            var Q0;
            Q0=makeQuery(id+"F83.opExtrude","CAP_FACE",FACE,{"disambiguationData":[OSD([sQuery(id+"F82.wireOp",EDGE,"E130.bottom"),sQuery(id+"F82.wireOp",EDGE,"E130.top"),sQuery(id+"F82.wireOp",EDGE,"E130.left"),sQuery(id+"F82.wireOp",EDGE,"E130.right")])],"isStart":false});
            var sketch = newSketch(context, id + "F84", { "sketchPlane" : qUnion([Q0])});
            skLineSegment(sketch, "E131.bottom", {"start": v(5029.2, -11760.2) * mm, "end": v(6731, -11760.2) * mm});
            skLineSegment(sketch, "E131.top", {"start": v(5029.2, -13030.2) * mm, "end": v(6731, -13030.2) * mm});
            skLineSegment(sketch, "E131.left", {"start": v(5029.2, -11760.2) * mm, "end": v(5029.2, -13030.2) * mm});
            skLineSegment(sketch, "E131.right", {"start": v(6731, -11760.2) * mm, "end": v(6731, -13030.2) * mm});
            skSolve(sketch);
        }
        {
            var Q0;
            Q0 = qSketchRegion(id + "F84", true);
            extrude(context, id + "F85", {"entities" : qUnion([Q0]), "operationType" : NewBodyOperationType.ADD, "depth" : 203.2 * mm});
        }
        {
            var Q0;
            Q0=makeQuery(id+"F85.opExtrude","CAP_FACE",FACE,{"disambiguationData":[OSD([sQuery(id+"F84.wireOp",EDGE,"E131.bottom"),sQuery(id+"F84.wireOp",EDGE,"E131.top"),sQuery(id+"F84.wireOp",EDGE,"E131.left"),sQuery(id+"F84.wireOp",EDGE,"E131.right")])],"isStart":false});
            var sketch = newSketch(context, id + "F86", { "sketchPlane" : qUnion([Q0])});
            skLineSegment(sketch, "E132.bottom", {"start": v(5029.2, -11760.2) * mm, "end": v(6731, -11760.2) * mm});
            skLineSegment(sketch, "E132.top", {"start": v(5029.2, -13309.6) * mm, "end": v(6731, -13309.6) * mm});
            skLineSegment(sketch, "E132.left", {"start": v(5029.2, -11760.2) * mm, "end": v(5029.2, -13309.6) * mm});
            skLineSegment(sketch, "E132.right", {"start": v(6731, -11760.2) * mm, "end": v(6731, -13309.6) * mm});
            skSolve(sketch);
        }
        {
            var Q0;
            Q0 = qSketchRegion(id + "F86", true);
            extrude(context, id + "F87", {"entities" : qUnion([Q0]), "operationType" : NewBodyOperationType.ADD, "depth" : 203.2 * mm});
        }
        {
            var Q0;
            {var subQ2=sQuery(id+"F21.wireOp",EDGE,"E37");var subQ3=sQuery(id+"F0.wireOp",EDGE,"E0.top");var subQ6=sQuery(id+"F29.wireOp",EDGE,"E50.top");var subQ17=sQuery(id+"F25.wireOp",EDGE,"E46.top");var subQ18=sQuery(id+"F19.wireOp",EDGE,"E30.top");var subQ19=sQuery(id+"F23.wireOp",EDGE,"E39.7.3");var subQ27=sQuery(id+"F0.wireOp",EDGE,"E0.right");var subQ31=sQuery(id+"F0.wireOp",EDGE,"E0.bottom");var subQ32=sQuery(id+"F0.wireOp",EDGE,"E0.left");var subQ36=sQuery(id+"F17.wireOp",EDGE,"E22.top");Q0=makeQuery(id+"F79.boolean.opBoolean","SPLIT",FACE,{"disambiguationData":[TD([makeQuery(id+"F1.opExtrude","SWEPT_FACE",FACE,{"disambiguationData":[OSD([subQ31])]})])],"derivedFrom":makeQuery(id+"F30.boolean.opBoolean","MERGE",FACE,{"derivedFrom":[makeQuery(id+"F26.boolean.opBoolean","MERGE",FACE,{"derivedFrom":[makeQuery(id+"F24.boolean.opBoolean","MERGE",FACE,{"derivedFrom":[makeQuery(id+"F22.boolean.opBoolean","MERGE",FACE,{"derivedFrom":[makeQuery(id+"F20.boolean.opBoolean","MERGE",FACE,{"derivedFrom":[makeQuery(id+"F18.boolean.opBoolean","MERGE",FACE,{"derivedFrom":[makeQuery(id+"F1.opExtrude","CAP_FACE",FACE,{"disambiguationData":[OSD([subQ31,subQ3,subQ32,subQ27])],"isStart":true}),makeQuery(id+"F18.opExtrude","SWEPT_FACE",FACE,{"disambiguationData":[OSD([subQ36])]})]}),makeQuery(id+"F20.opExtrude","SWEPT_FACE",FACE,{"disambiguationData":[OSD([subQ18])]})]}),makeQuery(id+"F22.opExtrude","SWEPT_FACE",FACE,{"disambiguationData":[OSD([subQ2])]})]}),makeQuery(id+"F24.opExtrude","SWEPT_FACE",FACE,{"disambiguationData":[OSD([subQ19])]})]}),makeQuery(id+"F26.opExtrude","SWEPT_FACE",FACE,{"disambiguationData":[OSD([subQ17])]})]}),makeQuery(id+"F30.opExtrude","SWEPT_FACE",FACE,{"disambiguationData":[OSD([subQ6])]})]})});}
            var sketch = newSketch(context, id + "F88", { "sketchPlane" : qUnion([Q0])});
            skLineSegment(sketch, "E133.top", {"start": v(6756.4, 767.08) * mm, "end": v(5029.2, 767.08) * mm});
            skLineSegment(sketch, "E133.left", {"start": v(6756.4, -25.4) * mm, "end": v(6756.4, 767.08) * mm});
            skLineSegment(sketch, "E133.right", {"start": v(5029.2, -25.4) * mm, "end": v(5029.2, 767.08) * mm});
            skLineSegment(sketch, "E134", {"start": v(5029.2, -25.4) * mm, "end": v(6756.4, -25.4) * mm});
            skSolve(sketch);
        }
        {
            var Q0;
            Q0 = qSketchRegion(id + "F88", true);
            extrude(context, id + "F89", {"entities" : qUnion([Q0]), "operationType" : NewBodyOperationType.ADD, "depth" : 203.2 * mm});
        }
        {
            var Q0;
            Q0=makeQuery(id+"F89.opExtrude","SWEPT_FACE",FACE,{"disambiguationData":[OSD([sQuery(id+"F88.wireOp",EDGE,"E133.left")])]});
            var sketch = newSketch(context, id + "F90", { "sketchPlane" : qUnion([Q0])});
            skLineSegment(sketch, "E135", {"start": v(-767.08, -203.2) * mm, "end": v(-1021.08, -203.2) * mm});
            skLineSegment(sketch, "E136", {"start": v(-1021.08, -203.2) * mm, "end": v(-1021.08, -406.4) * mm});
            skLineSegment(sketch, "E137", {"start": v(-1021.08, -406.4) * mm, "end": v(-1275.08, -406.4) * mm});
            skLineSegment(sketch, "E138", {"start": v(-1275.08, -406.4) * mm, "end": v(-1275.08, -609.6) * mm});
            skLineSegment(sketch, "E139", {"start": v(-1275.08, -609.6) * mm, "end": v(-1529.08, -609.6) * mm});
            skLineSegment(sketch, "E140", {"start": v(-1529.08, -609.6) * mm, "end": v(-1529.08, -812.8) * mm});
            skLineSegment(sketch, "E141", {"start": v(-1529.08, -812.8) * mm, "end": v(25.4, -812.8) * mm});
            skLineSegment(sketch, "E142", {"start": v(25.4, -812.8) * mm, "end": v(25.4, -203.2) * mm});
            skPoint(sketch, "E143.orphan", {"position": v(-1021.08, -406.4) * mm});
            skSolve(sketch);
        }
        {
            var Q0;
            Q0=makeQuery(id+"F90.imprint","IMPRINT",FACE,{"disambiguationData":[TD([[makeQuery(id+"F90.imprint","IMPRINT",EDGE,{"derivedFrom":sQuery(id+"F90.wireOp",EDGE,"E135")}),1.0]])]});
            var Q1;
            Q1=makeQuery(id+"F89.opExtrude","SWEPT_FACE",FACE,{"disambiguationData":[OSD([sQuery(id+"F88.wireOp",EDGE,"E133.right")])]});
            extrude(context, id + "F91", {"entities" : qUnion([Q0]), "operationType" : NewBodyOperationType.ADD, "endBound" : BoundingType.UP_TO_SURFACE, "oppositeDirection" : true, "endBoundEntityFace" : qUnion([Q1]), "depth" : 25.4 * mm});
        }
        {
            var Q0;
            Q0=makeQuery(id+"F38.boolean.opBoolean","SPLIT",FACE,{"disambiguationData":[TD([makeQuery(id+"F38.opExtrude","SWEPT_FACE",FACE,{"disambiguationData":[OSD([sQuery(id+"F35.wireOp",EDGE,"E56.bottom")])]})])],"derivedFrom":makeQuery(id+"F22.opExtrude","SWEPT_FACE",FACE,{"disambiguationData":[OSD([sQuery(id+"F21.wireOp",EDGE,"E36")])]})});
            var sketch = newSketch(context, id + "F92", { "sketchPlane" : qUnion([Q0])});
            skLineSegment(sketch, "E144.0", {"start": v(-16256, 2387.6) * mm, "end": v(-16256, 1066.8) * mm});
            skLineSegment(sketch, "E144.1", {"start": v(-15494, 2387.6) * mm, "end": v(-16256, 2387.6) * mm});
            skLineSegment(sketch, "E144.2", {"start": v(-15494, 1066.8) * mm, "end": v(-15494, 2387.6) * mm});
            skLineSegment(sketch, "E144.3", {"start": v(-16256, 1066.8) * mm, "end": v(-15494, 1066.8) * mm});
            skLineSegment(sketch, "E145.0", {"start": v(-14909.8, 2387.6) * mm, "end": v(-14909.8, 1066.8) * mm});
            skLineSegment(sketch, "E145.1", {"start": v(-14147.8, 2387.6) * mm, "end": v(-14909.8, 2387.6) * mm});
            skLineSegment(sketch, "E145.2", {"start": v(-14147.8, 1066.8) * mm, "end": v(-14147.8, 2387.6) * mm});
            skLineSegment(sketch, "E145.3", {"start": v(-14909.8, 1066.8) * mm, "end": v(-14147.8, 1066.8) * mm});
            skLineSegment(sketch, "E146.0", {"start": v(-12801.6, 2387.6) * mm, "end": v(-13563.6, 2387.6) * mm});
            skLineSegment(sketch, "E146.1", {"start": v(-12801.6, 101.6) * mm, "end": v(-12801.6, 2387.6) * mm});
            skLineSegment(sketch, "E146.2", {"start": v(-13563.6, 101.6) * mm, "end": v(-12801.6, 101.6) * mm});
            skLineSegment(sketch, "E146.3", {"start": v(-13563.6, 2387.6) * mm, "end": v(-13563.6, 101.6) * mm});
            skSolve(sketch);
        }
        {
            var Q0;
            Q0 = qSketchRegion(id + "F92", true);
            extrude(context, id + "F93", {"entities" : qUnion([Q0]), "operationType" : NewBodyOperationType.REMOVE, "oppositeDirection" : true, "depth" : 25.4 * mm});
        }
        {
            var Q0;
            Q0=makeQuery(id+"F24.opExtrude","CAP_FACE",FACE,{"disambiguationData":[OSD([sQuery(id+"F23.wireOp",EDGE,"E39.5.0"),sQuery(id+"F23.wireOp",EDGE,"E39.5.1"),sQuery(id+"F23.wireOp",EDGE,"E39.5.2"),sQuery(id+"F23.wireOp",EDGE,"E39.5.3")])],"isStart":false});
            var sketch = newSketch(context, id + "F94", { "sketchPlane" : qUnion([Q0])});
            skLineSegment(sketch, "E147.0", {"start": v(-9652, 3581.4) * mm, "end": v(-9652, 5257.8) * mm});
            skLineSegment(sketch, "E147.1", {"start": v(-10668, 3581.4) * mm, "end": v(-9652, 3581.4) * mm});
            skLineSegment(sketch, "E147.2", {"start": v(-10668, 5257.8) * mm, "end": v(-10668, 3581.4) * mm});
            skLineSegment(sketch, "E147.3", {"start": v(-9652, 5257.8) * mm, "end": v(-10668, 5257.8) * mm});
            skLineSegment(sketch, "E148.0", {"start": v(-7823.2, 3581.4) * mm, "end": v(-7823.2, 5257.8) * mm});
            skLineSegment(sketch, "E148.1", {"start": v(-8839.2, 3581.4) * mm, "end": v(-7823.2, 3581.4) * mm});
            skLineSegment(sketch, "E148.2", {"start": v(-8839.2, 5257.8) * mm, "end": v(-8839.2, 3581.4) * mm});
            skLineSegment(sketch, "E148.3", {"start": v(-7823.2, 5257.8) * mm, "end": v(-8839.2, 5257.8) * mm});
            skLineSegment(sketch, "E149.0", {"start": v(-7823.2, 2616.2) * mm, "end": v(-8839.2, 2616.2) * mm});
            skLineSegment(sketch, "E149.1", {"start": v(-7823.2, 939.8) * mm, "end": v(-7823.2, 2616.2) * mm});
            skLineSegment(sketch, "E149.2", {"start": v(-8839.2, 939.8) * mm, "end": v(-7823.2, 939.8) * mm});
            skLineSegment(sketch, "E149.3", {"start": v(-8839.2, 2616.2) * mm, "end": v(-8839.2, 939.8) * mm});
            skLineSegment(sketch, "E150.0", {"start": v(-5384.8, 3581.4) * mm, "end": v(-5384.8, 5257.8) * mm});
            skLineSegment(sketch, "E150.1", {"start": v(-6400.8, 3581.4) * mm, "end": v(-5384.8, 3581.4) * mm});
            skLineSegment(sketch, "E150.2", {"start": v(-6400.8, 5257.8) * mm, "end": v(-6400.8, 3581.4) * mm});
            skLineSegment(sketch, "E150.3", {"start": v(-5384.8, 5257.8) * mm, "end": v(-6400.8, 5257.8) * mm});
            skLineSegment(sketch, "E151.0", {"start": v(-2946.4, 3581.4) * mm, "end": v(-2946.4, 5257.8) * mm});
            skLineSegment(sketch, "E151.1", {"start": v(-3962.4, 3581.4) * mm, "end": v(-2946.4, 3581.4) * mm});
            skLineSegment(sketch, "E151.2", {"start": v(-3962.4, 5257.8) * mm, "end": v(-3962.4, 3581.4) * mm});
            skLineSegment(sketch, "E151.3", {"start": v(-2946.4, 5257.8) * mm, "end": v(-3962.4, 5257.8) * mm});
            skLineSegment(sketch, "E152.0", {"start": v(-1117.6, 3581.4) * mm, "end": v(-1117.6, 5257.8) * mm});
            skLineSegment(sketch, "E152.1", {"start": v(-2133.6, 3581.4) * mm, "end": v(-1117.6, 3581.4) * mm});
            skLineSegment(sketch, "E152.2", {"start": v(-2133.6, 5257.8) * mm, "end": v(-2133.6, 3581.4) * mm});
            skLineSegment(sketch, "E152.3", {"start": v(-1117.6, 5257.8) * mm, "end": v(-2133.6, 5257.8) * mm});
            skLineSegment(sketch, "E153.0", {"start": v(-2946.4, 2616.2) * mm, "end": v(-3962.4, 2616.2) * mm});
            skLineSegment(sketch, "E153.1", {"start": v(-2946.4, 939.8) * mm, "end": v(-2946.4, 2616.2) * mm});
            skLineSegment(sketch, "E153.2", {"start": v(-3962.4, 939.8) * mm, "end": v(-2946.4, 939.8) * mm});
            skLineSegment(sketch, "E153.3", {"start": v(-3962.4, 2616.2) * mm, "end": v(-3962.4, 939.8) * mm});
            skLineSegment(sketch, "E154.0", {"start": v(-1117.6, 2616.2) * mm, "end": v(-2133.6, 2616.2) * mm});
            skLineSegment(sketch, "E154.1", {"start": v(-1117.6, 939.8) * mm, "end": v(-1117.6, 2616.2) * mm});
            skLineSegment(sketch, "E154.2", {"start": v(-2133.6, 939.8) * mm, "end": v(-1117.6, 939.8) * mm});
            skLineSegment(sketch, "E154.3", {"start": v(-2133.6, 2616.2) * mm, "end": v(-2133.6, 939.8) * mm});
            skLineSegment(sketch, "E155.0", {"start": v(-5029.2, 38.1) * mm, "end": v(-4940.3, 38.1) * mm});
            skLineSegment(sketch, "E155.1", {"start": v(-4940.3, 2603.5) * mm, "end": v(-6845.3, 2603.5) * mm});
            skLineSegment(sketch, "E155.2", {"start": v(-6845.3, 2603.5) * mm, "end": v(-6845.3, 38.1) * mm});
            skLineSegment(sketch, "E155.3", {"start": v(-4940.3, 38.1) * mm, "end": v(-4940.3, 2603.5) * mm});
            skLineSegment(sketch, "E155.4", {"start": v(-6845.3, 38.1) * mm, "end": v(-6731, 38.1) * mm});
            skLineSegment(sketch, "E155.5", {"start": v(-6731, 38.1) * mm, "end": v(-5029.2, 38.1) * mm});
            skLineSegment(sketch, "E156.0.0", {"start": v(-9626.6, 3556) * mm, "end": v(-9626.6, 5283.2) * mm});
            skLineSegment(sketch, "E156.0.1", {"start": v(-9626.6, 5283.2) * mm, "end": v(-10693.4, 5283.2) * mm});
            skLineSegment(sketch, "E156.0.2", {"start": v(-10693.4, 5283.2) * mm, "end": v(-10693.4, 3556) * mm});
            skLineSegment(sketch, "E156.0.3", {"start": v(-10693.4, 3556) * mm, "end": v(-9626.6, 3556) * mm});
            skLineSegment(sketch, "E157.0.0", {"start": v(-7797.8, 2641.6) * mm, "end": v(-8864.6, 2641.6) * mm});
            skLineSegment(sketch, "E157.0.1", {"start": v(-8864.6, 2641.6) * mm, "end": v(-8864.6, 914.4) * mm});
            skLineSegment(sketch, "E157.0.2", {"start": v(-8864.6, 914.4) * mm, "end": v(-7797.8, 914.4) * mm});
            skLineSegment(sketch, "E157.0.3", {"start": v(-7797.8, 914.4) * mm, "end": v(-7797.8, 2641.6) * mm});
            skLineSegment(sketch, "E158.0.0", {"start": v(-7797.8, 3556) * mm, "end": v(-7797.8, 5283.2) * mm});
            skLineSegment(sketch, "E158.0.1", {"start": v(-7797.8, 5283.2) * mm, "end": v(-8864.6, 5283.2) * mm});
            skLineSegment(sketch, "E158.0.2", {"start": v(-8864.6, 5283.2) * mm, "end": v(-8864.6, 3556) * mm});
            skLineSegment(sketch, "E158.0.3", {"start": v(-8864.6, 3556) * mm, "end": v(-7797.8, 3556) * mm});
            skLineSegment(sketch, "E159.1.0", {"start": v(-5359.4, 3556) * mm, "end": v(-5359.4, 5283.2) * mm});
            skLineSegment(sketch, "E159.1.1", {"start": v(-5359.4, 5283.2) * mm, "end": v(-6426.2, 5283.2) * mm});
            skLineSegment(sketch, "E159.1.2", {"start": v(-6426.2, 5283.2) * mm, "end": v(-6426.2, 3556) * mm});
            skLineSegment(sketch, "E159.1.3", {"start": v(-6426.2, 3556) * mm, "end": v(-5359.4, 3556) * mm});
            skLineSegment(sketch, "E160.0.0", {"start": v(-4902.2, 0) * mm, "end": v(-4902.2, 2641.6) * mm});
            skLineSegment(sketch, "E160.0.1", {"start": v(-4902.2, 2641.6) * mm, "end": v(-6883.4, 2641.6) * mm});
            skLineSegment(sketch, "E160.0.2", {"start": v(-6883.4, 2641.6) * mm, "end": v(-6883.4, 0) * mm});
            skLineSegment(sketch, "E160.0.3", {"start": v(-6883.4, 0) * mm, "end": v(-6731, 0) * mm});
            skLineSegment(sketch, "E160.0.4", {"start": v(-6731, 0) * mm, "end": v(-5029.2, 0) * mm});
            skLineSegment(sketch, "E160.0.5", {"start": v(-5029.2, 0) * mm, "end": v(-4902.2, 0) * mm});
            skLineSegment(sketch, "E161.0.0", {"start": v(-2921, 2641.6) * mm, "end": v(-3987.8, 2641.6) * mm});
            skLineSegment(sketch, "E161.0.1", {"start": v(-3987.8, 2641.6) * mm, "end": v(-3987.8, 914.4) * mm});
            skLineSegment(sketch, "E161.0.2", {"start": v(-3987.8, 914.4) * mm, "end": v(-2921, 914.4) * mm});
            skLineSegment(sketch, "E161.0.3", {"start": v(-2921, 914.4) * mm, "end": v(-2921, 2641.6) * mm});
            skLineSegment(sketch, "E162.0.0", {"start": v(-2921, 3556) * mm, "end": v(-2921, 5283.2) * mm});
            skLineSegment(sketch, "E162.0.1", {"start": v(-2921, 5283.2) * mm, "end": v(-3987.8, 5283.2) * mm});
            skLineSegment(sketch, "E162.0.2", {"start": v(-3987.8, 5283.2) * mm, "end": v(-3987.8, 3556) * mm});
            skLineSegment(sketch, "E162.0.3", {"start": v(-3987.8, 3556) * mm, "end": v(-2921, 3556) * mm});
            skLineSegment(sketch, "E163.0.0", {"start": v(-1092.2, 3556) * mm, "end": v(-1092.2, 5283.2) * mm});
            skLineSegment(sketch, "E163.0.1", {"start": v(-1092.2, 5283.2) * mm, "end": v(-2159, 5283.2) * mm});
            skLineSegment(sketch, "E163.0.2", {"start": v(-2159, 5283.2) * mm, "end": v(-2159, 3556) * mm});
            skLineSegment(sketch, "E163.0.3", {"start": v(-2159, 3556) * mm, "end": v(-1092.2, 3556) * mm});
            skLineSegment(sketch, "E164.0.0", {"start": v(-1092.2, 2641.6) * mm, "end": v(-2159, 2641.6) * mm});
            skLineSegment(sketch, "E164.0.1", {"start": v(-2159, 2641.6) * mm, "end": v(-2159, 914.4) * mm});
            skLineSegment(sketch, "E164.0.2", {"start": v(-2159, 914.4) * mm, "end": v(-1092.2, 914.4) * mm});
            skLineSegment(sketch, "E164.0.3", {"start": v(-1092.2, 914.4) * mm, "end": v(-1092.2, 2641.6) * mm});
            skLineSegment(sketch, "E165.0", {"start": v(-9652, 2616.2) * mm, "end": v(-10668, 2616.2) * mm});
            skLineSegment(sketch, "E165.1", {"start": v(-9652, 939.8) * mm, "end": v(-9652, 2616.2) * mm});
            skLineSegment(sketch, "E165.2", {"start": v(-10668, 939.8) * mm, "end": v(-9652, 939.8) * mm});
            skLineSegment(sketch, "E165.3", {"start": v(-10668, 2616.2) * mm, "end": v(-10668, 939.8) * mm});
            skLineSegment(sketch, "E166.0", {"start": v(-9626.6, 2641.6) * mm, "end": v(-9626.6, 914.4) * mm});
            skLineSegment(sketch, "E166.1", {"start": v(-10693.4, 2641.6) * mm, "end": v(-9626.6, 2641.6) * mm});
            skLineSegment(sketch, "E166.2", {"start": v(-10693.4, 914.4) * mm, "end": v(-10693.4, 2641.6) * mm});
            skLineSegment(sketch, "E166.3", {"start": v(-9626.6, 914.4) * mm, "end": v(-10693.4, 914.4) * mm});
            skSolve(sketch);
        }
        {
            var Q0;
            Q0 = qSketchRegion(id + "F94", true);
            extrude(context, id + "F95", {"entities" : qUnion([Q0]), "operationType" : NewBodyOperationType.ADD, "depth" : 19.05 * mm});
        }
        {
            var Q0;
            Q0=makeQuery(id+"F18.opExtrude","CAP_FACE",FACE,{"disambiguationData":[OSD([sQuery(id+"F17.wireOp",EDGE,"E21.bottom"),sQuery(id+"F17.wireOp",EDGE,"E21.top"),sQuery(id+"F17.wireOp",EDGE,"E21.left"),sQuery(id+"F17.wireOp",EDGE,"E21.right")])],"isStart":false});
            var sketch = newSketch(context, id + "F96", { "sketchPlane" : qUnion([Q0])});
            skLineSegment(sketch, "E167.0", {"start": v(9652, 3581.4) * mm, "end": v(9652, 5257.8) * mm});
            skLineSegment(sketch, "E167.1", {"start": v(10668, 3581.4) * mm, "end": v(9652, 3581.4) * mm});
            skLineSegment(sketch, "E167.2", {"start": v(10668, 5257.8) * mm, "end": v(10668, 3581.4) * mm});
            skLineSegment(sketch, "E167.3", {"start": v(9652, 5257.8) * mm, "end": v(10668, 5257.8) * mm});
            skLineSegment(sketch, "E167.4", {"start": v(7823.2, 3581.4) * mm, "end": v(7823.2, 5257.8) * mm});
            skLineSegment(sketch, "E167.5", {"start": v(8839.2, 3581.4) * mm, "end": v(7823.2, 3581.4) * mm});
            skLineSegment(sketch, "E167.6", {"start": v(8839.2, 5257.8) * mm, "end": v(8839.2, 3581.4) * mm});
            skLineSegment(sketch, "E167.7", {"start": v(7823.2, 5257.8) * mm, "end": v(8839.2, 5257.8) * mm});
            skLineSegment(sketch, "E167.8", {"start": v(7823.2, 2616.2) * mm, "end": v(8839.2, 2616.2) * mm});
            skLineSegment(sketch, "E167.9", {"start": v(7823.2, 939.8) * mm, "end": v(7823.2, 2616.2) * mm});
            skLineSegment(sketch, "E167.10", {"start": v(8839.2, 939.8) * mm, "end": v(7823.2, 939.8) * mm});
            skLineSegment(sketch, "E167.11", {"start": v(8839.2, 2616.2) * mm, "end": v(8839.2, 939.8) * mm});
            skLineSegment(sketch, "E167.12", {"start": v(5384.8, 3581.4) * mm, "end": v(5384.8, 5257.8) * mm});
            skLineSegment(sketch, "E167.13", {"start": v(6400.8, 3581.4) * mm, "end": v(5384.8, 3581.4) * mm});
            skLineSegment(sketch, "E167.14", {"start": v(6400.8, 5257.8) * mm, "end": v(6400.8, 3581.4) * mm});
            skLineSegment(sketch, "E167.15", {"start": v(5384.8, 5257.8) * mm, "end": v(6400.8, 5257.8) * mm});
            skLineSegment(sketch, "E167.16", {"start": v(2946.4, 3581.4) * mm, "end": v(2946.4, 5257.8) * mm});
            skLineSegment(sketch, "E167.17", {"start": v(3962.4, 3581.4) * mm, "end": v(2946.4, 3581.4) * mm});
            skLineSegment(sketch, "E167.18", {"start": v(3962.4, 5257.8) * mm, "end": v(3962.4, 3581.4) * mm});
            skLineSegment(sketch, "E167.19", {"start": v(2946.4, 5257.8) * mm, "end": v(3962.4, 5257.8) * mm});
            skLineSegment(sketch, "E167.20", {"start": v(1117.6, 3581.4) * mm, "end": v(1117.6, 5257.8) * mm});
            skLineSegment(sketch, "E167.21", {"start": v(2133.6, 3581.4) * mm, "end": v(1117.6, 3581.4) * mm});
            skLineSegment(sketch, "E167.22", {"start": v(2133.6, 5257.8) * mm, "end": v(2133.6, 3581.4) * mm});
            skLineSegment(sketch, "E167.23", {"start": v(1117.6, 5257.8) * mm, "end": v(2133.6, 5257.8) * mm});
            skLineSegment(sketch, "E167.24", {"start": v(2946.4, 2616.2) * mm, "end": v(3962.4, 2616.2) * mm});
            skLineSegment(sketch, "E167.25", {"start": v(2946.4, 939.8) * mm, "end": v(2946.4, 2616.2) * mm});
            skLineSegment(sketch, "E167.26", {"start": v(3962.4, 939.8) * mm, "end": v(2946.4, 939.8) * mm});
            skLineSegment(sketch, "E167.27", {"start": v(3962.4, 2616.2) * mm, "end": v(3962.4, 939.8) * mm});
            skLineSegment(sketch, "E167.28", {"start": v(1117.6, 2616.2) * mm, "end": v(2133.6, 2616.2) * mm});
            skLineSegment(sketch, "E167.29", {"start": v(1117.6, 939.8) * mm, "end": v(1117.6, 2616.2) * mm});
            skLineSegment(sketch, "E167.30", {"start": v(2133.6, 939.8) * mm, "end": v(1117.6, 939.8) * mm});
            skLineSegment(sketch, "E167.31", {"start": v(2133.6, 2616.2) * mm, "end": v(2133.6, 939.8) * mm});
            skLineSegment(sketch, "E167.32", {"start": v(5029.2, 38.1) * mm, "end": v(4940.3, 38.1) * mm});
            skLineSegment(sketch, "E167.33", {"start": v(4940.3, 2603.5) * mm, "end": v(6845.3, 2603.5) * mm});
            skLineSegment(sketch, "E167.34", {"start": v(6845.3, 2603.5) * mm, "end": v(6845.3, 38.1) * mm});
            skLineSegment(sketch, "E167.35", {"start": v(4940.3, 38.1) * mm, "end": v(4940.3, 2603.5) * mm});
            skLineSegment(sketch, "E167.36", {"start": v(6845.3, 38.1) * mm, "end": v(6731, 38.1) * mm});
            skLineSegment(sketch, "E167.37", {"start": v(6731, 38.1) * mm, "end": v(5029.2, 38.1) * mm});
            skLineSegment(sketch, "E167.38", {"start": v(9626.6, 3556) * mm, "end": v(9626.6, 5283.2) * mm});
            skLineSegment(sketch, "E167.39", {"start": v(9626.6, 5283.2) * mm, "end": v(10693.4, 5283.2) * mm});
            skLineSegment(sketch, "E167.40", {"start": v(10693.4, 5283.2) * mm, "end": v(10693.4, 3556) * mm});
            skLineSegment(sketch, "E167.41", {"start": v(10693.4, 3556) * mm, "end": v(9626.6, 3556) * mm});
            skLineSegment(sketch, "E167.42", {"start": v(7797.8, 2641.6) * mm, "end": v(8864.6, 2641.6) * mm});
            skLineSegment(sketch, "E167.43", {"start": v(8864.6, 2641.6) * mm, "end": v(8864.6, 914.4) * mm});
            skLineSegment(sketch, "E167.44", {"start": v(8864.6, 914.4) * mm, "end": v(7797.8, 914.4) * mm});
            skLineSegment(sketch, "E167.45", {"start": v(7797.8, 914.4) * mm, "end": v(7797.8, 2641.6) * mm});
            skLineSegment(sketch, "E167.46", {"start": v(7797.8, 3556) * mm, "end": v(7797.8, 5283.2) * mm});
            skLineSegment(sketch, "E167.47", {"start": v(7797.8, 5283.2) * mm, "end": v(8864.6, 5283.2) * mm});
            skLineSegment(sketch, "E167.48", {"start": v(8864.6, 5283.2) * mm, "end": v(8864.6, 3556) * mm});
            skLineSegment(sketch, "E167.49", {"start": v(8864.6, 3556) * mm, "end": v(7797.8, 3556) * mm});
            skLineSegment(sketch, "E167.50", {"start": v(5359.4, 3556) * mm, "end": v(5359.4, 5283.2) * mm});
            skLineSegment(sketch, "E167.51", {"start": v(5359.4, 5283.2) * mm, "end": v(6426.2, 5283.2) * mm});
            skLineSegment(sketch, "E167.52", {"start": v(6426.2, 5283.2) * mm, "end": v(6426.2, 3556) * mm});
            skLineSegment(sketch, "E167.53", {"start": v(6426.2, 3556) * mm, "end": v(5359.4, 3556) * mm});
            skLineSegment(sketch, "E167.54", {"start": v(4902.2, 0) * mm, "end": v(4902.2, 2641.6) * mm});
            skLineSegment(sketch, "E167.55", {"start": v(4902.2, 2641.6) * mm, "end": v(6883.4, 2641.6) * mm});
            skLineSegment(sketch, "E167.56", {"start": v(6883.4, 2641.6) * mm, "end": v(6883.4, 0) * mm});
            skLineSegment(sketch, "E167.57", {"start": v(6883.4, 0) * mm, "end": v(6731, 0) * mm});
            skLineSegment(sketch, "E167.58", {"start": v(6731, 0) * mm, "end": v(5029.2, 0) * mm});
            skLineSegment(sketch, "E167.59", {"start": v(5029.2, 0) * mm, "end": v(4902.2, 0) * mm});
            skLineSegment(sketch, "E167.60", {"start": v(2921, 2641.6) * mm, "end": v(3987.8, 2641.6) * mm});
            skLineSegment(sketch, "E167.61", {"start": v(3987.8, 2641.6) * mm, "end": v(3987.8, 914.4) * mm});
            skLineSegment(sketch, "E167.62", {"start": v(3987.8, 914.4) * mm, "end": v(2921, 914.4) * mm});
            skLineSegment(sketch, "E167.63", {"start": v(2921, 914.4) * mm, "end": v(2921, 2641.6) * mm});
            skLineSegment(sketch, "E167.64", {"start": v(2921, 3556) * mm, "end": v(2921, 5283.2) * mm});
            skLineSegment(sketch, "E167.65", {"start": v(2921, 5283.2) * mm, "end": v(3987.8, 5283.2) * mm});
            skLineSegment(sketch, "E167.66", {"start": v(3987.8, 5283.2) * mm, "end": v(3987.8, 3556) * mm});
            skLineSegment(sketch, "E167.67", {"start": v(3987.8, 3556) * mm, "end": v(2921, 3556) * mm});
            skLineSegment(sketch, "E167.68", {"start": v(1092.2, 3556) * mm, "end": v(1092.2, 5283.2) * mm});
            skLineSegment(sketch, "E167.69", {"start": v(1092.2, 5283.2) * mm, "end": v(2159, 5283.2) * mm});
            skLineSegment(sketch, "E167.70", {"start": v(2159, 5283.2) * mm, "end": v(2159, 3556) * mm});
            skLineSegment(sketch, "E167.71", {"start": v(2159, 3556) * mm, "end": v(1092.2, 3556) * mm});
            skLineSegment(sketch, "E167.72", {"start": v(1092.2, 2641.6) * mm, "end": v(2159, 2641.6) * mm});
            skLineSegment(sketch, "E167.73", {"start": v(2159, 2641.6) * mm, "end": v(2159, 914.4) * mm});
            skLineSegment(sketch, "E167.74", {"start": v(2159, 914.4) * mm, "end": v(1092.2, 914.4) * mm});
            skLineSegment(sketch, "E167.75", {"start": v(1092.2, 914.4) * mm, "end": v(1092.2, 2641.6) * mm});
            skLineSegment(sketch, "E167.76", {"start": v(9652, 2616.2) * mm, "end": v(10668, 2616.2) * mm});
            skLineSegment(sketch, "E167.77", {"start": v(9652, 939.8) * mm, "end": v(9652, 2616.2) * mm});
            skLineSegment(sketch, "E167.78", {"start": v(10668, 939.8) * mm, "end": v(9652, 939.8) * mm});
            skLineSegment(sketch, "E167.79", {"start": v(10668, 2616.2) * mm, "end": v(10668, 939.8) * mm});
            skLineSegment(sketch, "E167.80", {"start": v(9626.6, 2641.6) * mm, "end": v(9626.6, 914.4) * mm});
            skLineSegment(sketch, "E167.81", {"start": v(10693.4, 2641.6) * mm, "end": v(9626.6, 2641.6) * mm});
            skLineSegment(sketch, "E167.82", {"start": v(10693.4, 914.4) * mm, "end": v(10693.4, 2641.6) * mm});
            skLineSegment(sketch, "E167.83", {"start": v(9626.6, 914.4) * mm, "end": v(10693.4, 914.4) * mm});
            skSolve(sketch);
        }
        {
            var Q0;
            Q0 = qSketchRegion(id + "F96", true);
            extrude(context, id + "F97", {"entities" : qUnion([Q0]), "operationType" : NewBodyOperationType.ADD, "depth" : 19.05 * mm});
        }
        {
            var Q0;
            Q0=makeQuery(id+"F26.opExtrude","CAP_FACE",FACE,{"disambiguationData":[OSD([sQuery(id+"F25.wireOp",EDGE,"E46.bottom"),sQuery(id+"F25.wireOp",EDGE,"E46.top"),sQuery(id+"F25.wireOp",EDGE,"E46.left"),sQuery(id+"F25.wireOp",EDGE,"E46.right")])],"isStart":false});
            var sketch = newSketch(context, id + "F98", { "sketchPlane" : qUnion([Q0])});
            skLineSegment(sketch, "E168.0", {"start": v(-10668, 2616.2) * mm, "end": v(-10668, 939.8) * mm});
            skLineSegment(sketch, "E168.1", {"start": v(-9652, 2616.2) * mm, "end": v(-10668, 2616.2) * mm});
            skLineSegment(sketch, "E168.2", {"start": v(-9652, 939.8) * mm, "end": v(-9652, 2616.2) * mm});
            skLineSegment(sketch, "E168.3", {"start": v(-10668, 939.8) * mm, "end": v(-9652, 939.8) * mm});
            skLineSegment(sketch, "E169.0", {"start": v(-8839.2, 2616.2) * mm, "end": v(-8839.2, 939.8) * mm});
            skLineSegment(sketch, "E169.1", {"start": v(-7823.2, 2616.2) * mm, "end": v(-8839.2, 2616.2) * mm});
            skLineSegment(sketch, "E169.2", {"start": v(-7823.2, 939.8) * mm, "end": v(-7823.2, 2616.2) * mm});
            skLineSegment(sketch, "E169.3", {"start": v(-8839.2, 939.8) * mm, "end": v(-7823.2, 939.8) * mm});
            skLineSegment(sketch, "E170.0", {"start": v(-2946.4, 3581.4) * mm, "end": v(-2946.4, 5257.8) * mm});
            skLineSegment(sketch, "E170.1", {"start": v(-3962.4, 3581.4) * mm, "end": v(-2946.4, 3581.4) * mm});
            skLineSegment(sketch, "E170.2", {"start": v(-3962.4, 5257.8) * mm, "end": v(-3962.4, 3581.4) * mm});
            skLineSegment(sketch, "E170.3", {"start": v(-2946.4, 5257.8) * mm, "end": v(-3962.4, 5257.8) * mm});
            skLineSegment(sketch, "E171.0", {"start": v(-1117.6, 3581.4) * mm, "end": v(-1117.6, 5257.8) * mm});
            skLineSegment(sketch, "E171.1", {"start": v(-2133.6, 3581.4) * mm, "end": v(-1117.6, 3581.4) * mm});
            skLineSegment(sketch, "E171.2", {"start": v(-2133.6, 5257.8) * mm, "end": v(-2133.6, 3581.4) * mm});
            skLineSegment(sketch, "E171.3", {"start": v(-1117.6, 5257.8) * mm, "end": v(-2133.6, 5257.8) * mm});
            skLineSegment(sketch, "E172.0", {"start": v(-3962.4, 2616.2) * mm, "end": v(-3962.4, 939.8) * mm});
            skLineSegment(sketch, "E172.1", {"start": v(-2946.4, 2616.2) * mm, "end": v(-3962.4, 2616.2) * mm});
            skLineSegment(sketch, "E172.2", {"start": v(-2946.4, 939.8) * mm, "end": v(-2946.4, 2616.2) * mm});
            skLineSegment(sketch, "E172.3", {"start": v(-3962.4, 939.8) * mm, "end": v(-2946.4, 939.8) * mm});
            skLineSegment(sketch, "E173.0", {"start": v(-1117.6, 2616.2) * mm, "end": v(-2133.6, 2616.2) * mm});
            skLineSegment(sketch, "E173.1", {"start": v(-1117.6, 939.8) * mm, "end": v(-1117.6, 2616.2) * mm});
            skLineSegment(sketch, "E173.2", {"start": v(-2133.6, 939.8) * mm, "end": v(-1117.6, 939.8) * mm});
            skLineSegment(sketch, "E173.3", {"start": v(-2133.6, 2616.2) * mm, "end": v(-2133.6, 939.8) * mm});
            skLineSegment(sketch, "E174.0.0", {"start": v(-1092.2, 2641.6) * mm, "end": v(-2159, 2641.6) * mm});
            skLineSegment(sketch, "E174.0.1", {"start": v(-2159, 2641.6) * mm, "end": v(-2159, 914.4) * mm});
            skLineSegment(sketch, "E174.0.2", {"start": v(-2159, 914.4) * mm, "end": v(-1092.2, 914.4) * mm});
            skLineSegment(sketch, "E174.0.3", {"start": v(-1092.2, 914.4) * mm, "end": v(-1092.2, 2641.6) * mm});
            skLineSegment(sketch, "E175.0.0", {"start": v(-1092.2, 3556) * mm, "end": v(-1092.2, 5283.2) * mm});
            skLineSegment(sketch, "E175.0.1", {"start": v(-1092.2, 5283.2) * mm, "end": v(-2159, 5283.2) * mm});
            skLineSegment(sketch, "E175.0.2", {"start": v(-2159, 5283.2) * mm, "end": v(-2159, 3556) * mm});
            skLineSegment(sketch, "E175.0.3", {"start": v(-2159, 3556) * mm, "end": v(-1092.2, 3556) * mm});
            skLineSegment(sketch, "E176.0.0", {"start": v(-2921, 3556) * mm, "end": v(-2921, 5283.2) * mm});
            skLineSegment(sketch, "E176.0.1", {"start": v(-2921, 5283.2) * mm, "end": v(-3987.8, 5283.2) * mm});
            skLineSegment(sketch, "E176.0.2", {"start": v(-3987.8, 5283.2) * mm, "end": v(-3987.8, 3556) * mm});
            skLineSegment(sketch, "E176.0.3", {"start": v(-3987.8, 3556) * mm, "end": v(-2921, 3556) * mm});
            skLineSegment(sketch, "E177.0.0", {"start": v(-3987.8, 2641.6) * mm, "end": v(-3987.8, 914.4) * mm});
            skLineSegment(sketch, "E177.0.1", {"start": v(-3987.8, 914.4) * mm, "end": v(-2921, 914.4) * mm});
            skLineSegment(sketch, "E177.0.2", {"start": v(-2921, 914.4) * mm, "end": v(-2921, 2641.6) * mm});
            skLineSegment(sketch, "E177.0.3", {"start": v(-2921, 2641.6) * mm, "end": v(-3987.8, 2641.6) * mm});
            skLineSegment(sketch, "E178.0.2", {"start": v(-5003.8, 0) * mm, "end": v(-203.2, 0) * mm});
            skLineSegment(sketch, "E178.0.3", {"start": v(-203.2, 0) * mm, "end": v(-203.2, 5181.6) * mm});
            skLineSegment(sketch, "E178.0.4", {"start": v(-203.2, 5181.6) * mm, "end": v(-1092.2, 5181.6) * mm});
            skLineSegment(sketch, "E178.0.5", {"start": v(-1092.2, 5181.6) * mm, "end": v(-1092.2, 3556) * mm});
            skLineSegment(sketch, "E178.0.6", {"start": v(-1092.2, 3556) * mm, "end": v(-2159, 3556) * mm});
            skLineSegment(sketch, "E178.0.7", {"start": v(-2159, 3556) * mm, "end": v(-2159, 5181.6) * mm});
            skLineSegment(sketch, "E178.0.8", {"start": v(-2159, 5181.6) * mm, "end": v(-2921, 5181.6) * mm});
            skLineSegment(sketch, "E178.0.9", {"start": v(-2921, 5181.6) * mm, "end": v(-2921, 3556) * mm});
            skLineSegment(sketch, "E178.0.10", {"start": v(-2921, 3556) * mm, "end": v(-3987.8, 3556) * mm});
            skLineSegment(sketch, "E178.0.11", {"start": v(-3987.8, 3556) * mm, "end": v(-3987.8, 5181.6) * mm});
            skLineSegment(sketch, "E178.0.12", {"start": v(-3987.8, 5181.6) * mm, "end": v(-4546.6, 5181.6) * mm});
            skLineSegment(sketch, "E178.0.29", {"start": v(-11582.4, 5181.6) * mm, "end": v(-11582.4, 0) * mm});
            skLineSegment(sketch, "E179.0", {"start": v(-7797.8, 2641.6) * mm, "end": v(-7797.8, 914.4) * mm});
            skLineSegment(sketch, "E180.0.0", {"start": v(-8864.6, 2641.6) * mm, "end": v(-8864.6, 914.4) * mm});
            skLineSegment(sketch, "E180.0.1", {"start": v(-8864.6, 914.4) * mm, "end": v(-7797.8, 914.4) * mm});
            skLineSegment(sketch, "E180.0.2", {"start": v(-7797.8, 914.4) * mm, "end": v(-7797.8, 2641.6) * mm});
            skLineSegment(sketch, "E180.0.3", {"start": v(-7797.8, 2641.6) * mm, "end": v(-8864.6, 2641.6) * mm});
            skLineSegment(sketch, "E181.0", {"start": v(-9626.6, 2641.6) * mm, "end": v(-9626.6, 914.4) * mm});
            skLineSegment(sketch, "E181.1", {"start": v(-10693.4, 2641.6) * mm, "end": v(-9626.6, 2641.6) * mm});
            skLineSegment(sketch, "E181.2", {"start": v(-10693.4, 2641.6) * mm, "end": v(-10693.4, 914.4) * mm});
            skLineSegment(sketch, "E181.3", {"start": v(-10693.4, 914.4) * mm, "end": v(-9626.6, 914.4) * mm});
            skLineSegment(sketch, "E182.0.0", {"start": v(-9626.6, 3556) * mm, "end": v(-9626.6, 5283.2) * mm});
            skLineSegment(sketch, "E182.0.1", {"start": v(-9626.6, 5283.2) * mm, "end": v(-10693.4, 5283.2) * mm});
            skLineSegment(sketch, "E182.0.2", {"start": v(-10693.4, 5283.2) * mm, "end": v(-10693.4, 3556) * mm});
            skLineSegment(sketch, "E182.0.3", {"start": v(-10693.4, 3556) * mm, "end": v(-9626.6, 3556) * mm});
            skLineSegment(sketch, "E183.0.0", {"start": v(-7797.8, 3556) * mm, "end": v(-7797.8, 5283.2) * mm});
            skLineSegment(sketch, "E183.0.1", {"start": v(-7797.8, 5283.2) * mm, "end": v(-8864.6, 5283.2) * mm});
            skLineSegment(sketch, "E183.0.2", {"start": v(-8864.6, 5283.2) * mm, "end": v(-8864.6, 3556) * mm});
            skLineSegment(sketch, "E183.0.3", {"start": v(-8864.6, 3556) * mm, "end": v(-7797.8, 3556) * mm});
            skLineSegment(sketch, "E184.0.0", {"start": v(-6172.2, 3556) * mm, "end": v(-6172.2, 5283.2) * mm});
            skLineSegment(sketch, "E184.0.1", {"start": v(-6172.2, 5283.2) * mm, "end": v(-7239, 5283.2) * mm});
            skLineSegment(sketch, "E184.0.2", {"start": v(-7239, 5283.2) * mm, "end": v(-7239, 3556) * mm});
            skLineSegment(sketch, "E184.0.3", {"start": v(-7239, 3556) * mm, "end": v(-6172.2, 3556) * mm});
            skLineSegment(sketch, "E185.0.0", {"start": v(-4546.6, 3556) * mm, "end": v(-4546.6, 5283.2) * mm});
            skLineSegment(sketch, "E185.0.1", {"start": v(-4546.6, 5283.2) * mm, "end": v(-5613.4, 5283.2) * mm});
            skLineSegment(sketch, "E185.0.2", {"start": v(-5613.4, 5283.2) * mm, "end": v(-5613.4, 3556) * mm});
            skLineSegment(sketch, "E185.0.3", {"start": v(-5613.4, 3556) * mm, "end": v(-4546.6, 3556) * mm});
            skLineSegment(sketch, "E186.0", {"start": v(-4572, 3581.4) * mm, "end": v(-4572, 5257.8) * mm});
            skLineSegment(sketch, "E186.1", {"start": v(-5588, 3581.4) * mm, "end": v(-4572, 3581.4) * mm});
            skLineSegment(sketch, "E186.2", {"start": v(-5588, 5257.8) * mm, "end": v(-5588, 3581.4) * mm});
            skLineSegment(sketch, "E186.3", {"start": v(-4572, 5257.8) * mm, "end": v(-5588, 5257.8) * mm});
            skLineSegment(sketch, "E187.0", {"start": v(-6197.6, 3581.4) * mm, "end": v(-6197.6, 5257.8) * mm});
            skLineSegment(sketch, "E187.1", {"start": v(-7213.6, 3581.4) * mm, "end": v(-6197.6, 3581.4) * mm});
            skLineSegment(sketch, "E187.2", {"start": v(-7213.6, 5257.8) * mm, "end": v(-7213.6, 3581.4) * mm});
            skLineSegment(sketch, "E187.3", {"start": v(-6197.6, 5257.8) * mm, "end": v(-7213.6, 5257.8) * mm});
            skLineSegment(sketch, "E188.0", {"start": v(-7823.2, 3581.4) * mm, "end": v(-7823.2, 5257.8) * mm});
            skLineSegment(sketch, "E188.1", {"start": v(-8839.2, 3581.4) * mm, "end": v(-7823.2, 3581.4) * mm});
            skLineSegment(sketch, "E188.2", {"start": v(-8839.2, 5257.8) * mm, "end": v(-8839.2, 3581.4) * mm});
            skLineSegment(sketch, "E188.3", {"start": v(-7823.2, 5257.8) * mm, "end": v(-8839.2, 5257.8) * mm});
            skLineSegment(sketch, "E189.0", {"start": v(-9652, 3581.4) * mm, "end": v(-9652, 5257.8) * mm});
            skLineSegment(sketch, "E189.1", {"start": v(-10668, 3581.4) * mm, "end": v(-9652, 3581.4) * mm});
            skLineSegment(sketch, "E189.2", {"start": v(-10668, 5257.8) * mm, "end": v(-10668, 3581.4) * mm});
            skLineSegment(sketch, "E189.3", {"start": v(-9652, 5257.8) * mm, "end": v(-10668, 5257.8) * mm});
            skSolve(sketch);
        }
        {
            var Q0;
            Q0 = qSketchRegion(id + "F98", true);
            extrude(context, id + "F99", {"entities" : qUnion([Q0]), "operationType" : NewBodyOperationType.ADD, "depth" : 19.05 * mm});
        }
        {
            var Q0;
            Q0=makeQuery(id+"F26.opExtrude","CAP_FACE",FACE,{"disambiguationData":[OSD([sQuery(id+"F25.wireOp",EDGE,"E46.bottom"),sQuery(id+"F25.wireOp",EDGE,"E46.top"),sQuery(id+"F25.wireOp",EDGE,"E46.left"),sQuery(id+"F25.wireOp",EDGE,"E46.right")])],"isStart":false});
            var sketch = newSketch(context, id + "F100", { "sketchPlane" : qUnion([Q0])});
            skLineSegment(sketch, "E190.0", {"start": v(-5041.9, 38.1) * mm, "end": v(-5041.9, 2603.5) * mm});
            skLineSegment(sketch, "E190.1", {"start": v(-7200.9, 38.1) * mm, "end": v(-5041.9, 38.1) * mm});
            skLineSegment(sketch, "E190.2", {"start": v(-7200.9, 2603.5) * mm, "end": v(-7200.9, 38.1) * mm});
            skLineSegment(sketch, "E190.3", {"start": v(-5041.9, 2603.5) * mm, "end": v(-7200.9, 2603.5) * mm});
            skSolve(sketch);
        }
        {
            var Q0;
            Q0=makeQuery(id+"F100.imprint","IMPRINT",FACE,{"disambiguationData":[TD([[makeQuery(id+"F100.imprint","IMPRINT",EDGE,{"derivedFrom":sQuery(id+"F100.wireOp",EDGE,"E190.0")}),-1.0]])]});
            extrude(context, id + "F101", {"entities" : qUnion([Q0]), "operationType" : NewBodyOperationType.ADD, "depth" : 19.05 * mm});
        }
        {
            var Q0;
            Q0=makeQuery(id+"F20.opExtrude","CAP_FACE",FACE,{"disambiguationData":[OSD([sQuery(id+"F19.wireOp",EDGE,"E30.bottom"),sQuery(id+"F19.wireOp",EDGE,"E30.top"),sQuery(id+"F19.wireOp",EDGE,"E30.left"),sQuery(id+"F19.wireOp",EDGE,"E30.right")])],"isStart":false});
            var sketch = newSketch(context, id + "F102", { "sketchPlane" : qUnion([Q0])});
            skLineSegment(sketch, "E191.0.0", {"start": v(1092.2, 2641.6) * mm, "end": v(1092.2, 914.4) * mm});
            skLineSegment(sketch, "E191.0.1", {"start": v(1092.2, 914.4) * mm, "end": v(2159, 914.4) * mm});
            skLineSegment(sketch, "E191.0.2", {"start": v(2159, 914.4) * mm, "end": v(2159, 2641.6) * mm});
            skLineSegment(sketch, "E191.0.3", {"start": v(2159, 2641.6) * mm, "end": v(1092.2, 2641.6) * mm});
            skLineSegment(sketch, "E192.0.0", {"start": v(2159, 3556) * mm, "end": v(2159, 5283.2) * mm});
            skLineSegment(sketch, "E192.0.1", {"start": v(2159, 5283.2) * mm, "end": v(1092.2, 5283.2) * mm});
            skLineSegment(sketch, "E192.0.2", {"start": v(1092.2, 5283.2) * mm, "end": v(1092.2, 3556) * mm});
            skLineSegment(sketch, "E192.0.3", {"start": v(1092.2, 3556) * mm, "end": v(2159, 3556) * mm});
            skLineSegment(sketch, "E193.0.0", {"start": v(3987.8, 3556) * mm, "end": v(3987.8, 5283.2) * mm});
            skLineSegment(sketch, "E193.0.1", {"start": v(3987.8, 5283.2) * mm, "end": v(2921, 5283.2) * mm});
            skLineSegment(sketch, "E193.0.2", {"start": v(2921, 5283.2) * mm, "end": v(2921, 3556) * mm});
            skLineSegment(sketch, "E193.0.3", {"start": v(2921, 3556) * mm, "end": v(3987.8, 3556) * mm});
            skLineSegment(sketch, "E194.0.0", {"start": v(6426.2, 4013.2) * mm, "end": v(6426.2, 5283.2) * mm});
            skLineSegment(sketch, "E194.0.1", {"start": v(6426.2, 5283.2) * mm, "end": v(5359.4, 5283.2) * mm});
            skLineSegment(sketch, "E194.0.2", {"start": v(5359.4, 5283.2) * mm, "end": v(5359.4, 4013.2) * mm});
            skLineSegment(sketch, "E194.0.3", {"start": v(5359.4, 4013.2) * mm, "end": v(6426.2, 4013.2) * mm});
            skLineSegment(sketch, "E195.0.0", {"start": v(8864.6, 3556) * mm, "end": v(8864.6, 5283.2) * mm});
            skLineSegment(sketch, "E195.0.1", {"start": v(8864.6, 5283.2) * mm, "end": v(7797.8, 5283.2) * mm});
            skLineSegment(sketch, "E195.0.2", {"start": v(7797.8, 5283.2) * mm, "end": v(7797.8, 3556) * mm});
            skLineSegment(sketch, "E195.0.3", {"start": v(7797.8, 3556) * mm, "end": v(8864.6, 3556) * mm});
            skLineSegment(sketch, "E196.0.0", {"start": v(10693.4, 3556) * mm, "end": v(10693.4, 5283.2) * mm});
            skLineSegment(sketch, "E196.0.1", {"start": v(10693.4, 5283.2) * mm, "end": v(9626.6, 5283.2) * mm});
            skLineSegment(sketch, "E196.0.2", {"start": v(9626.6, 5283.2) * mm, "end": v(9626.6, 3556) * mm});
            skLineSegment(sketch, "E196.0.3", {"start": v(9626.6, 3556) * mm, "end": v(10693.4, 3556) * mm});
            skLineSegment(sketch, "E197.0", {"start": v(10668, 3581.4) * mm, "end": v(10668, 5257.8) * mm});
            skLineSegment(sketch, "E197.1", {"start": v(9652, 3581.4) * mm, "end": v(10668, 3581.4) * mm});
            skLineSegment(sketch, "E197.2", {"start": v(9652, 5257.8) * mm, "end": v(9652, 3581.4) * mm});
            skLineSegment(sketch, "E197.3", {"start": v(10668, 5257.8) * mm, "end": v(9652, 5257.8) * mm});
            skLineSegment(sketch, "E198.0", {"start": v(8839.2, 3581.4) * mm, "end": v(8839.2, 5257.8) * mm});
            skLineSegment(sketch, "E198.1", {"start": v(7823.2, 3581.4) * mm, "end": v(8839.2, 3581.4) * mm});
            skLineSegment(sketch, "E198.2", {"start": v(7823.2, 5257.8) * mm, "end": v(7823.2, 3581.4) * mm});
            skLineSegment(sketch, "E198.3", {"start": v(8839.2, 5257.8) * mm, "end": v(7823.2, 5257.8) * mm});
            skLineSegment(sketch, "E199.0", {"start": v(6400.8, 4038.6) * mm, "end": v(6400.8, 5257.8) * mm});
            skLineSegment(sketch, "E199.1", {"start": v(5384.8, 4038.6) * mm, "end": v(6400.8, 4038.6) * mm});
            skLineSegment(sketch, "E199.2", {"start": v(5384.8, 5257.8) * mm, "end": v(5384.8, 4038.6) * mm});
            skLineSegment(sketch, "E199.3", {"start": v(6400.8, 5257.8) * mm, "end": v(5384.8, 5257.8) * mm});
            skLineSegment(sketch, "E200.0", {"start": v(3962.4, 3581.4) * mm, "end": v(3962.4, 5257.8) * mm});
            skLineSegment(sketch, "E200.1", {"start": v(2946.4, 3581.4) * mm, "end": v(3962.4, 3581.4) * mm});
            skLineSegment(sketch, "E200.2", {"start": v(2946.4, 5257.8) * mm, "end": v(2946.4, 3581.4) * mm});
            skLineSegment(sketch, "E200.3", {"start": v(3962.4, 5257.8) * mm, "end": v(2946.4, 5257.8) * mm});
            skLineSegment(sketch, "E201.0", {"start": v(2133.6, 3581.4) * mm, "end": v(2133.6, 5257.8) * mm});
            skLineSegment(sketch, "E201.1", {"start": v(1117.6, 3581.4) * mm, "end": v(2133.6, 3581.4) * mm});
            skLineSegment(sketch, "E201.2", {"start": v(1117.6, 5257.8) * mm, "end": v(1117.6, 3581.4) * mm});
            skLineSegment(sketch, "E201.3", {"start": v(2133.6, 5257.8) * mm, "end": v(1117.6, 5257.8) * mm});
            skLineSegment(sketch, "E202.0", {"start": v(1117.6, 2616.2) * mm, "end": v(1117.6, 939.8) * mm});
            skLineSegment(sketch, "E202.1", {"start": v(2133.6, 2616.2) * mm, "end": v(1117.6, 2616.2) * mm});
            skLineSegment(sketch, "E202.2", {"start": v(2133.6, 939.8) * mm, "end": v(2133.6, 2616.2) * mm});
            skLineSegment(sketch, "E202.3", {"start": v(1117.6, 939.8) * mm, "end": v(2133.6, 939.8) * mm});
            skSolve(sketch);
        }
        {
            var Q0;
            Q0 = qSketchRegion(id + "F102", true);
            extrude(context, id + "F103", {"entities" : qUnion([Q0]), "operationType" : NewBodyOperationType.ADD, "depth" : 19.05 * mm});
        }
        {
            var Q0;
            Q0=makeQuery(id+"F34.opExtrude","CAP_FACE",FACE,{"disambiguationData":[OSD([sQuery(id+"F33.wireOp",EDGE,"E53.bottom"),sQuery(id+"F33.wireOp",EDGE,"E53.top"),sQuery(id+"F33.wireOp",EDGE,"E53.left"),sQuery(id+"F33.wireOp",EDGE,"E53.right")])],"isStart":false});
            var sketch = newSketch(context, id + "F104", { "sketchPlane" : qUnion([Q0])});
            skLineSegment(sketch, "E203.0.0", {"start": v(6908.8, 2595.47) * mm, "end": v(6908.8, 1071.47) * mm});
            skLineSegment(sketch, "E203.0.1", {"start": v(6908.8, 1071.47) * mm, "end": v(7772.4, 1071.47) * mm});
            skLineSegment(sketch, "E203.0.2", {"start": v(7772.4, 1071.47) * mm, "end": v(7772.4, 2595.47) * mm});
            skLineSegment(sketch, "E203.0.3", {"start": v(7772.4, 2595.47) * mm, "end": v(6908.8, 2595.47) * mm});
            skLineSegment(sketch, "E204.0", {"start": v(6934.2, 2570.07) * mm, "end": v(6934.2, 1096.87) * mm});
            skLineSegment(sketch, "E204.1", {"start": v(7747, 2570.07) * mm, "end": v(6934.2, 2570.07) * mm});
            skLineSegment(sketch, "E204.2", {"start": v(7747, 1096.87) * mm, "end": v(7747, 2570.07) * mm});
            skLineSegment(sketch, "E204.3", {"start": v(6934.2, 1096.87) * mm, "end": v(7747, 1096.87) * mm});
            skSolve(sketch);
        }
        {
            var Q0;
            Q0 = qSketchRegion(id + "F104", true);
            extrude(context, id + "F105", {"entities" : qUnion([Q0]), "operationType" : NewBodyOperationType.ADD, "depth" : 19.05 * mm});
        }
        {
            var Q0;
            Q0=makeQuery(id+"F38.boolean.opBoolean","SPLIT",FACE,{"disambiguationData":[TD([makeQuery(id+"F38.opExtrude","SWEPT_FACE",FACE,{"disambiguationData":[OSD([sQuery(id+"F35.wireOp",EDGE,"E54.0.0")])]})])],"derivedFrom":makeQuery(id+"F22.opExtrude","SWEPT_FACE",FACE,{"disambiguationData":[OSD([sQuery(id+"F21.wireOp",EDGE,"E36")])]})});
            var sketch = newSketch(context, id + "F106", { "sketchPlane" : qUnion([Q0])});
            skLineSegment(sketch, "E205.0.0", {"start": v(-16357.6, 2489.2) * mm, "end": v(-16357.6, 965.2) * mm});
            skLineSegment(sketch, "E205.0.1", {"start": v(-16357.6, 965.2) * mm, "end": v(-15392.4, 965.2) * mm});
            skLineSegment(sketch, "E205.0.2", {"start": v(-15392.4, 965.2) * mm, "end": v(-15392.4, 2489.2) * mm});
            skLineSegment(sketch, "E205.0.3", {"start": v(-15392.4, 2489.2) * mm, "end": v(-16357.6, 2489.2) * mm});
            skLineSegment(sketch, "E206.0.0", {"start": v(-15011.4, 2489.2) * mm, "end": v(-15011.4, 965.2) * mm});
            skLineSegment(sketch, "E206.0.1", {"start": v(-15011.4, 965.2) * mm, "end": v(-14046.2, 965.2) * mm});
            skLineSegment(sketch, "E206.0.2", {"start": v(-14046.2, 965.2) * mm, "end": v(-14046.2, 2489.2) * mm});
            skLineSegment(sketch, "E206.0.3", {"start": v(-14046.2, 2489.2) * mm, "end": v(-15011.4, 2489.2) * mm});
            skLineSegment(sketch, "E207.0", {"start": v(-14986, 2463.8) * mm, "end": v(-14986, 990.6) * mm});
            skLineSegment(sketch, "E207.1", {"start": v(-14071.6, 2463.8) * mm, "end": v(-14986, 2463.8) * mm});
            skLineSegment(sketch, "E207.2", {"start": v(-14071.6, 990.6) * mm, "end": v(-14071.6, 2463.8) * mm});
            skLineSegment(sketch, "E207.3", {"start": v(-14986, 990.6) * mm, "end": v(-14071.6, 990.6) * mm});
            skLineSegment(sketch, "E208.0", {"start": v(-16332.2, 2463.8) * mm, "end": v(-16332.2, 990.6) * mm});
            skLineSegment(sketch, "E208.1", {"start": v(-15417.8, 2463.8) * mm, "end": v(-16332.2, 2463.8) * mm});
            skLineSegment(sketch, "E208.2", {"start": v(-15417.8, 990.6) * mm, "end": v(-15417.8, 2463.8) * mm});
            skLineSegment(sketch, "E208.3", {"start": v(-16332.2, 990.6) * mm, "end": v(-15417.8, 990.6) * mm});
            skSolve(sketch);
        }
        {
            var Q0;
            Q0 = qSketchRegion(id + "F106", true);
            extrude(context, id + "F107", {"entities" : qUnion([Q0]), "operationType" : NewBodyOperationType.ADD, "depth" : 19.05 * mm});
        }
        {
            var Q0;
            Q0=makeQuery(id+"F97.boolean.opBoolean","MERGE",FACE,{"derivedFrom":[makeQuery(id+"F18.opExtrude","SWEPT_FACE",FACE,{"disambiguationData":[OSD([sQuery(id+"F17.wireOp",EDGE,"E22.bottom")])]}),makeQuery(id+"F97.opExtrude","SWEPT_FACE",FACE,{"disambiguationData":[OSD([sQuery(id+"F96.wireOp",EDGE,"E167.55")])]})]});
            var sketch = newSketch(context, id + "F108", { "sketchPlane" : qUnion([Q0])});
            skLineSegment(sketch, "E209.0", {"start": v(6959.6, 101.6) * mm, "end": v(4826, 101.6) * mm});
            skLineSegment(sketch, "E209.1", {"start": v(6959.6, -100.33) * mm, "end": v(6959.6, 101.6) * mm});
            skLineSegment(sketch, "E209.2", {"start": v(4826, -100.33) * mm, "end": v(6959.6, -100.33) * mm});
            skLineSegment(sketch, "E209.3", {"start": v(4826, 101.6) * mm, "end": v(4826, -100.33) * mm});
            skSolve(sketch);
        }
        {
            var Q0;
            Q0 = qSketchRegion(id + "F108", true);
            extrude(context, id + "F109", {"entities" : qUnion([Q0]), "operationType" : NewBodyOperationType.ADD, "depth" : 50.8 * mm});
        }
        {
            var Q0;
            Q0=makeQuery(id+"F109.opExtrude","CAP_FACE",FACE,{"disambiguationData":[OSD([sQuery(id+"F108.wireOp",EDGE,"E209.0"),sQuery(id+"F108.wireOp",EDGE,"E209.1"),sQuery(id+"F108.wireOp",EDGE,"E209.2"),sQuery(id+"F108.wireOp",EDGE,"E209.3")])],"isStart":false});
            var sketch = newSketch(context, id + "F110", { "sketchPlane" : qUnion([Q0])});
            skLineSegment(sketch, "E210.0", {"start": v(7035.8, -176.53) * mm, "end": v(7035.8, 101.6) * mm});
            skLineSegment(sketch, "E210.1", {"start": v(4749.8, -176.53) * mm, "end": v(7035.8, -176.53) * mm});
            skLineSegment(sketch, "E210.2", {"start": v(4749.8, 101.6) * mm, "end": v(4749.8, -176.53) * mm});
            skLineSegment(sketch, "E210.3", {"start": v(7035.8, 101.6) * mm, "end": v(4749.8, 101.6) * mm});
            skSolve(sketch);
        }
        {
            var Q0;
            Q0 = qSketchRegion(id + "F110", true);
            extrude(context, id + "F111", {"entities" : qUnion([Q0]), "operationType" : NewBodyOperationType.ADD, "depth" : 25.4 * mm});
        }
        {
            var Q0;
            Q0=makeQuery(id+"F111.opExtrude","SWEPT_FACE",FACE,{"disambiguationData":[OSD([sQuery(id+"F110.wireOp",EDGE,"E210.0")])]});
            var sketch = newSketch(context, id + "F112", { "sketchPlane" : qUnion([Q0])});
            skLineSegment(sketch, "E211", {"start": v(-176.53, 2717.8) * mm, "end": v(25.4, 2743.2) * mm});
            skLineSegment(sketch, "E212", {"start": v(25.4, 2743.2) * mm, "end": v(25.4, 2717.8) * mm});
            skLineSegment(sketch, "E213", {"start": v(25.4, 2717.8) * mm, "end": v(-176.53, 2717.8) * mm});
            skSolve(sketch);
        }
        {
            var Q0;
            Q0=makeQuery(id+"F112.imprint","IMPRINT",FACE,{"disambiguationData":[TD([[makeQuery(id+"F112.imprint","IMPRINT",EDGE,{"derivedFrom":sQuery(id+"F112.wireOp",EDGE,"E211")}),-1.0]])]});
            var Q1;
            Q1=makeQuery(id+"F111.opExtrude","SWEPT_FACE",FACE,{"disambiguationData":[OSD([sQuery(id+"F110.wireOp",EDGE,"E210.2")])]});
            extrude(context, id + "F113", {"entities" : qUnion([Q0]), "operationType" : NewBodyOperationType.ADD, "endBound" : BoundingType.UP_TO_SURFACE, "oppositeDirection" : true, "endBoundEntityFace" : qUnion([Q1]), "depth" : 25.4 * mm});
        }
        {
            var Q0;
            Q0=makeQuery(id+"F95.boolean.opBoolean","MERGE",FACE,{"derivedFrom":[makeQuery(id+"F24.opExtrude","SWEPT_FACE",FACE,{"disambiguationData":[OSD([sQuery(id+"F23.wireOp",EDGE,"E39.7.1")])]}),makeQuery(id+"F95.opExtrude","SWEPT_FACE",FACE,{"disambiguationData":[OSD([sQuery(id+"F94.wireOp",EDGE,"E160.0.1")])]})]});
            var sketch = newSketch(context, id + "F114", { "sketchPlane" : qUnion([Q0])});
            skLineSegment(sketch, "E214.0", {"start": v(4826, 11684) * mm, "end": v(6959.6, 11684) * mm});
            skLineSegment(sketch, "E214.1", {"start": v(4826, 11885.93) * mm, "end": v(4826, 11684) * mm});
            skLineSegment(sketch, "E214.2", {"start": v(6959.6, 11885.93) * mm, "end": v(4826, 11885.93) * mm});
            skLineSegment(sketch, "E214.3", {"start": v(6959.6, 11684) * mm, "end": v(6959.6, 11885.93) * mm});
            skSolve(sketch);
        }
        {
            var Q0;
            Q0 = qSketchRegion(id + "F114", true);
            extrude(context, id + "F115", {"entities" : qUnion([Q0]), "operationType" : NewBodyOperationType.ADD, "depth" : 76.2 * mm});
        }
        {
            var Q0;
            Q0=makeQuery(id+"F115.opExtrude","CAP_FACE",FACE,{"disambiguationData":[OSD([sQuery(id+"F114.wireOp",EDGE,"E214.0"),sQuery(id+"F114.wireOp",EDGE,"E214.1"),sQuery(id+"F114.wireOp",EDGE,"E214.2"),sQuery(id+"F114.wireOp",EDGE,"E214.3")])],"isStart":false});
            var sketch = newSketch(context, id + "F116", { "sketchPlane" : qUnion([Q0])});
            skLineSegment(sketch, "E215.0", {"start": v(4749.8, 11962.13) * mm, "end": v(4749.8, 11684) * mm});
            skLineSegment(sketch, "E215.1", {"start": v(7035.8, 11962.13) * mm, "end": v(4749.8, 11962.13) * mm});
            skLineSegment(sketch, "E215.2", {"start": v(7035.8, 11684) * mm, "end": v(7035.8, 11962.13) * mm});
            skLineSegment(sketch, "E215.3", {"start": v(4749.8, 11684) * mm, "end": v(7035.8, 11684) * mm});
            skSolve(sketch);
        }
        {
            var Q0;
            Q0 = qSketchRegion(id + "F116", true);
            extrude(context, id + "F117", {"entities" : qUnion([Q0]), "operationType" : NewBodyOperationType.ADD, "depth" : 25.4 * mm});
        }
        {
            var Q0;
            Q0=makeQuery(id+"F117.opExtrude","SWEPT_FACE",FACE,{"disambiguationData":[OSD([sQuery(id+"F116.wireOp",EDGE,"E215.0")])]});
            var sketch = newSketch(context, id + "F118", { "sketchPlane" : qUnion([Q0])});
            skLineSegment(sketch, "E216", {"start": v(-11962.13, 2743.2) * mm, "end": v(-11760.2, 2768.6) * mm});
            skLineSegment(sketch, "E217", {"start": v(-11760.2, 2768.6) * mm, "end": v(-11760.2, 2743.2) * mm});
            skSolve(sketch);
        }
        {
            var Q0;
            Q0=makeQuery(id+"F118.imprint","IMPRINT",FACE,{"disambiguationData":[TD([[makeQuery(id+"F118.imprint","IMPRINT",EDGE,{"derivedFrom":sQuery(id+"F118.wireOp",EDGE,"E216")}),-1.0]])]});
            var Q1;
            Q1=makeQuery(id+"F117.opExtrude","SWEPT_FACE",FACE,{"disambiguationData":[OSD([sQuery(id+"F116.wireOp",EDGE,"E215.2")])]});
            extrude(context, id + "F119", {"entities" : qUnion([Q0]), "operationType" : NewBodyOperationType.ADD, "endBound" : BoundingType.UP_TO_SURFACE, "oppositeDirection" : true, "endBoundEntityFace" : qUnion([Q1]), "depth" : 25.4 * mm});
        }
        {
            var Q0;
            Q0=makeQuery(id+"F16.boolean.opBoolean","COPY",FACE,{"derivedFrom":makeQuery(id+"F16.opExtrude","CAP_FACE",FACE,{"disambiguationData":[OSD([sQuery(id+"F15.wireOp",EDGE,"E11.0.0"),sQuery(id+"F15.wireOp",EDGE,"E11.0.1"),sQuery(id+"F15.wireOp",EDGE,"E11.0.2"),sQuery(id+"F15.wireOp",EDGE,"E11.0.3")])],"isStart":false})});
            var sketch = newSketch(context, id + "F120", { "sketchPlane" : qUnion([Q0])});
            skLineSegment(sketch, "E218.bottom", {"start": v(1092.2, 914.4) * mm, "end": v(2159, 914.4) * mm});
            skLineSegment(sketch, "E218.top", {"start": v(1092.2, 977.9) * mm, "end": v(2159, 977.9) * mm});
            skLineSegment(sketch, "E218.left", {"start": v(1092.2, 914.4) * mm, "end": v(1092.2, 977.9) * mm});
            skLineSegment(sketch, "E218.right", {"start": v(2159, 914.4) * mm, "end": v(2159, 977.9) * mm});
            skLineSegment(sketch, "E219.bottom", {"start": v(2921, 914.4) * mm, "end": v(3987.8, 914.4) * mm});
            skLineSegment(sketch, "E219.top", {"start": v(2921, 977.9) * mm, "end": v(3987.8, 977.9) * mm});
            skLineSegment(sketch, "E219.left", {"start": v(2921, 914.4) * mm, "end": v(2921, 977.9) * mm});
            skLineSegment(sketch, "E219.right", {"start": v(3987.8, 914.4) * mm, "end": v(3987.8, 977.9) * mm});
            skLineSegment(sketch, "E220.bottom", {"start": v(1092.2, 3556) * mm, "end": v(2159, 3556) * mm});
            skLineSegment(sketch, "E220.top", {"start": v(1092.2, 3619.5) * mm, "end": v(2159, 3619.5) * mm});
            skLineSegment(sketch, "E220.left", {"start": v(1092.2, 3556) * mm, "end": v(1092.2, 3619.5) * mm});
            skLineSegment(sketch, "E220.right", {"start": v(2159, 3556) * mm, "end": v(2159, 3619.5) * mm});
            skLineSegment(sketch, "E221.bottom", {"start": v(2921, 3556) * mm, "end": v(3987.8, 3556) * mm});
            skLineSegment(sketch, "E221.top", {"start": v(2921, 3619.5) * mm, "end": v(3987.8, 3619.5) * mm});
            skLineSegment(sketch, "E221.left", {"start": v(2921, 3556) * mm, "end": v(2921, 3619.5) * mm});
            skLineSegment(sketch, "E221.right", {"start": v(3987.8, 3556) * mm, "end": v(3987.8, 3619.5) * mm});
            skLineSegment(sketch, "E222.bottom", {"start": v(5359.4, 3556) * mm, "end": v(6426.2, 3556) * mm});
            skLineSegment(sketch, "E222.top", {"start": v(5359.4, 3619.5) * mm, "end": v(6426.2, 3619.5) * mm});
            skLineSegment(sketch, "E222.left", {"start": v(5359.4, 3556) * mm, "end": v(5359.4, 3619.5) * mm});
            skLineSegment(sketch, "E222.right", {"start": v(6426.2, 3556) * mm, "end": v(6426.2, 3619.5) * mm});
            skLineSegment(sketch, "E223.bottom", {"start": v(7797.8, 3556) * mm, "end": v(8864.6, 3556) * mm});
            skLineSegment(sketch, "E223.top", {"start": v(7797.8, 3619.5) * mm, "end": v(8864.6, 3619.5) * mm});
            skLineSegment(sketch, "E223.left", {"start": v(7797.8, 3556) * mm, "end": v(7797.8, 3619.5) * mm});
            skLineSegment(sketch, "E223.right", {"start": v(8864.6, 3556) * mm, "end": v(8864.6, 3619.5) * mm});
            skLineSegment(sketch, "E224.bottom", {"start": v(9626.6, 3556) * mm, "end": v(10693.4, 3556) * mm});
            skLineSegment(sketch, "E224.top", {"start": v(9626.6, 3619.5) * mm, "end": v(10693.4, 3619.5) * mm});
            skLineSegment(sketch, "E224.left", {"start": v(9626.6, 3556) * mm, "end": v(9626.6, 3619.5) * mm});
            skLineSegment(sketch, "E224.right", {"start": v(10693.4, 3556) * mm, "end": v(10693.4, 3619.5) * mm});
            skLineSegment(sketch, "E225.bottom", {"start": v(7797.8, 914.4) * mm, "end": v(8864.6, 914.4) * mm});
            skLineSegment(sketch, "E225.top", {"start": v(7797.8, 977.9) * mm, "end": v(8864.6, 977.9) * mm});
            skLineSegment(sketch, "E225.left", {"start": v(7797.8, 914.4) * mm, "end": v(7797.8, 977.9) * mm});
            skLineSegment(sketch, "E225.right", {"start": v(8864.6, 914.4) * mm, "end": v(8864.6, 977.9) * mm});
            skLineSegment(sketch, "E226.bottom", {"start": v(9626.6, 914.4) * mm, "end": v(10693.4, 914.4) * mm});
            skLineSegment(sketch, "E226.top", {"start": v(9626.6, 977.9) * mm, "end": v(10693.4, 977.9) * mm});
            skLineSegment(sketch, "E226.left", {"start": v(9626.6, 914.4) * mm, "end": v(9626.6, 977.9) * mm});
            skLineSegment(sketch, "E226.right", {"start": v(10693.4, 914.4) * mm, "end": v(10693.4, 977.9) * mm});
            skSolve(sketch);
        }
        {
            var Q0;
            Q0 = qSketchRegion(id + "F120", true);
            var Q1;
            Q1=makeQuery(id+"F63.boolean.opBoolean","COPY",FACE,{"derivedFrom":makeQuery(id+"F63.opExtrude","CAP_FACE",FACE,{"disambiguationData":[OSD([sQuery(id+"F62.wireOp",EDGE,"E113.0"),sQuery(id+"F62.wireOp",EDGE,"E113.1"),sQuery(id+"F62.wireOp",EDGE,"E113.2"),sQuery(id+"F62.wireOp",EDGE,"E113.3")])],"isStart":false})});
            extrude(context, id + "F121", {"entities" : qUnion([Q0]), "operationType" : NewBodyOperationType.ADD, "depth" : 88.9 * mm});
        }
        {
            var Q0;
            Q0=makeQuery(id+"F14.boolean.opBoolean","COPY",FACE,{"derivedFrom":makeQuery(id+"F14.opExtrude","CAP_FACE",FACE,{"disambiguationData":[OSD([sQuery(id+"F0.wireOp",EDGE,"E0.top"),sQuery(id+"F13.wireOp",EDGE,"E8"),sQuery(id+"F13.wireOp",EDGE,"E9"),sQuery(id+"F13.wireOp",EDGE,"E10")])],"isStart":false})});
            var sketch = newSketch(context, id + "F122", { "sketchPlane" : qUnion([Q0])});
            skLineSegment(sketch, "E227.0.0", {"start": v(-2159, 3619.5) * mm, "end": v(-1092.2, 3619.5) * mm});
            skLineSegment(sketch, "E227.0.1", {"start": v(-1092.2, 3619.5) * mm, "end": v(-1092.2, 3556) * mm});
            skLineSegment(sketch, "E227.0.2", {"start": v(-1092.2, 3556) * mm, "end": v(-2159, 3556) * mm});
            skLineSegment(sketch, "E227.0.3", {"start": v(-2159, 3556) * mm, "end": v(-2159, 3619.5) * mm});
            skLineSegment(sketch, "E227.1.0", {"start": v(-3987.8, 3619.5) * mm, "end": v(-2921, 3619.5) * mm});
            skLineSegment(sketch, "E227.1.1", {"start": v(-2921, 3619.5) * mm, "end": v(-2921, 3556) * mm});
            skLineSegment(sketch, "E227.1.2", {"start": v(-2921, 3556) * mm, "end": v(-3987.8, 3556) * mm});
            skLineSegment(sketch, "E227.1.3", {"start": v(-3987.8, 3556) * mm, "end": v(-3987.8, 3619.5) * mm});
            skLineSegment(sketch, "E227.2.0", {"start": v(-2159, 977.9) * mm, "end": v(-1092.2, 977.9) * mm});
            skLineSegment(sketch, "E227.2.1", {"start": v(-1092.2, 977.9) * mm, "end": v(-1092.2, 914.4) * mm});
            skLineSegment(sketch, "E227.2.2", {"start": v(-1092.2, 914.4) * mm, "end": v(-2159, 914.4) * mm});
            skLineSegment(sketch, "E227.2.3", {"start": v(-2159, 914.4) * mm, "end": v(-2159, 977.9) * mm});
            skLineSegment(sketch, "E227.3.0", {"start": v(-3987.8, 977.9) * mm, "end": v(-2921, 977.9) * mm});
            skLineSegment(sketch, "E227.3.1", {"start": v(-2921, 977.9) * mm, "end": v(-2921, 914.4) * mm});
            skLineSegment(sketch, "E227.3.2", {"start": v(-2921, 914.4) * mm, "end": v(-3987.8, 914.4) * mm});
            skLineSegment(sketch, "E227.3.3", {"start": v(-3987.8, 914.4) * mm, "end": v(-3987.8, 977.9) * mm});
            skLineSegment(sketch, "E227.4.0", {"start": v(-6426.2, 3619.5) * mm, "end": v(-5359.4, 3619.5) * mm});
            skLineSegment(sketch, "E227.4.1", {"start": v(-5359.4, 3619.5) * mm, "end": v(-5359.4, 3556) * mm});
            skLineSegment(sketch, "E227.4.2", {"start": v(-5359.4, 3556) * mm, "end": v(-6426.2, 3556) * mm});
            skLineSegment(sketch, "E227.4.3", {"start": v(-6426.2, 3556) * mm, "end": v(-6426.2, 3619.5) * mm});
            skLineSegment(sketch, "E227.5.0", {"start": v(-8864.6, 3619.5) * mm, "end": v(-7797.8, 3619.5) * mm});
            skLineSegment(sketch, "E227.5.1", {"start": v(-7797.8, 3619.5) * mm, "end": v(-7797.8, 3556) * mm});
            skLineSegment(sketch, "E227.5.2", {"start": v(-7797.8, 3556) * mm, "end": v(-8864.6, 3556) * mm});
            skLineSegment(sketch, "E227.5.3", {"start": v(-8864.6, 3556) * mm, "end": v(-8864.6, 3619.5) * mm});
            skLineSegment(sketch, "E227.6.0", {"start": v(-10693.4, 3619.5) * mm, "end": v(-9626.6, 3619.5) * mm});
            skLineSegment(sketch, "E227.6.1", {"start": v(-9626.6, 3619.5) * mm, "end": v(-9626.6, 3556) * mm});
            skLineSegment(sketch, "E227.6.2", {"start": v(-9626.6, 3556) * mm, "end": v(-10693.4, 3556) * mm});
            skLineSegment(sketch, "E227.6.3", {"start": v(-10693.4, 3556) * mm, "end": v(-10693.4, 3619.5) * mm});
            skLineSegment(sketch, "E227.7.0", {"start": v(-8864.6, 977.9) * mm, "end": v(-7797.8, 977.9) * mm});
            skLineSegment(sketch, "E227.7.1", {"start": v(-7797.8, 977.9) * mm, "end": v(-7797.8, 914.4) * mm});
            skLineSegment(sketch, "E227.7.2", {"start": v(-7797.8, 914.4) * mm, "end": v(-8864.6, 914.4) * mm});
            skLineSegment(sketch, "E227.7.3", {"start": v(-8864.6, 914.4) * mm, "end": v(-8864.6, 977.9) * mm});
            skLineSegment(sketch, "E227.8.0", {"start": v(-10693.4, 977.9) * mm, "end": v(-9626.6, 977.9) * mm});
            skLineSegment(sketch, "E227.8.1", {"start": v(-9626.6, 977.9) * mm, "end": v(-9626.6, 914.4) * mm});
            skLineSegment(sketch, "E227.8.2", {"start": v(-9626.6, 914.4) * mm, "end": v(-10693.4, 914.4) * mm});
            skLineSegment(sketch, "E227.8.3", {"start": v(-10693.4, 914.4) * mm, "end": v(-10693.4, 977.9) * mm});
            skSolve(sketch);
        }
        {
            var Q0;
            Q0 = qSketchRegion(id + "F122", true);
            extrude(context, id + "F123", {"entities" : qUnion([Q0]), "operationType" : NewBodyOperationType.ADD, "depth" : 88.9 * mm});
        }
        {
            var Q0;
            Q0=makeQuery(id+"F38.boolean.opBoolean","COPY",FACE,{"derivedFrom":makeQuery(id+"F38.opExtrude","CAP_FACE",FACE,{"disambiguationData":[OSD([sQuery(id+"F35.wireOp",EDGE,"E54.0.0"),sQuery(id+"F35.wireOp",EDGE,"E54.0.1"),sQuery(id+"F35.wireOp",EDGE,"E54.0.2"),sQuery(id+"F35.wireOp",EDGE,"E54.0.3"),sQuery(id+"F35.wireOp",EDGE,"E54.0.4"),sQuery(id+"F35.wireOp",EDGE,"E54.0.5"),sQuery(id+"F35.wireOp",EDGE,"E54.0.6"),sQuery(id+"F35.wireOp",EDGE,"E54.0.7"),sQuery(id+"F35.wireOp",EDGE,"E55.bottom"),sQuery(id+"F35.wireOp",EDGE,"E55.top"),sQuery(id+"F35.wireOp",EDGE,"E55.left"),sQuery(id+"F35.wireOp",EDGE,"E55.right"),sQuery(id+"F35.wireOp",EDGE,"E56.bottom"),sQuery(id+"F35.wireOp",EDGE,"E56.top"),sQuery(id+"F35.wireOp",EDGE,"E56.left"),sQuery(id+"F35.wireOp",EDGE,"E56.right")])],"isStart":false})});
            var sketch = newSketch(context, id + "F124", { "sketchPlane" : qUnion([Q0])});
            skLineSegment(sketch, "E228.bottom", {"start": v(-16357.6, 965.2) * mm, "end": v(-15392.4, 965.2) * mm});
            skLineSegment(sketch, "E228.top", {"start": v(-16357.6, 1028.7) * mm, "end": v(-15392.4, 1028.7) * mm});
            skLineSegment(sketch, "E228.left", {"start": v(-16357.6, 965.2) * mm, "end": v(-16357.6, 1028.7) * mm});
            skLineSegment(sketch, "E228.right", {"start": v(-15392.4, 965.2) * mm, "end": v(-15392.4, 1028.7) * mm});
            skLineSegment(sketch, "E229.bottom", {"start": v(-15011.4, 965.2) * mm, "end": v(-14046.2, 965.2) * mm});
            skLineSegment(sketch, "E229.top", {"start": v(-15011.4, 1028.7) * mm, "end": v(-14046.2, 1028.7) * mm});
            skLineSegment(sketch, "E229.left", {"start": v(-15011.4, 965.2) * mm, "end": v(-15011.4, 1028.7) * mm});
            skLineSegment(sketch, "E229.right", {"start": v(-14046.2, 965.2) * mm, "end": v(-14046.2, 1028.7) * mm});
            skSolve(sketch);
        }
        {
            var Q0;
            Q0 = qSketchRegion(id + "F124", true);
            extrude(context, id + "F125", {"entities" : qUnion([Q0]), "operationType" : NewBodyOperationType.ADD, "depth" : 88.9 * mm});
        }
        {
            var Q0;
            Q0=makeQuery(id+"F10.boolean.opBoolean","COPY",FACE,{"derivedFrom":makeQuery(id+"F10.opExtrude","CAP_FACE",FACE,{"disambiguationData":[OSD([sQuery(id+"F0.wireOp",EDGE,"E0.right"),sQuery(id+"F9.wireOp",EDGE,"E4"),sQuery(id+"F9.wireOp",EDGE,"E5"),sQuery(id+"F9.wireOp",EDGE,"E6")])],"isStart":false})});
            var sketch = newSketch(context, id + "F126", { "sketchPlane" : qUnion([Q0])});
            skLineSegment(sketch, "E230.bottom", {"start": v(1092.2, 3556) * mm, "end": v(2159, 3556) * mm});
            skLineSegment(sketch, "E230.top", {"start": v(1092.2, 3619.5) * mm, "end": v(2159, 3619.5) * mm});
            skLineSegment(sketch, "E230.left", {"start": v(1092.2, 3556) * mm, "end": v(1092.2, 3619.5) * mm});
            skLineSegment(sketch, "E230.right", {"start": v(2159, 3556) * mm, "end": v(2159, 3619.5) * mm});
            skLineSegment(sketch, "E231.bottom", {"start": v(2921, 3556) * mm, "end": v(3987.8, 3556) * mm});
            skLineSegment(sketch, "E231.top", {"start": v(2921, 3619.5) * mm, "end": v(3987.8, 3619.5) * mm});
            skLineSegment(sketch, "E231.left", {"start": v(2921, 3556) * mm, "end": v(2921, 3619.5) * mm});
            skLineSegment(sketch, "E231.right", {"start": v(3987.8, 3556) * mm, "end": v(3987.8, 3619.5) * mm});
            skLineSegment(sketch, "E232.bottom", {"start": v(1092.2, 914.4) * mm, "end": v(2159, 914.4) * mm});
            skLineSegment(sketch, "E232.top", {"start": v(1092.2, 977.9) * mm, "end": v(2159, 977.9) * mm});
            skLineSegment(sketch, "E232.left", {"start": v(1092.2, 914.4) * mm, "end": v(1092.2, 977.9) * mm});
            skLineSegment(sketch, "E232.right", {"start": v(2159, 914.4) * mm, "end": v(2159, 977.9) * mm});
            skLineSegment(sketch, "E233.bottom", {"start": v(5359.4, 4013.2) * mm, "end": v(6426.2, 4013.2) * mm});
            skLineSegment(sketch, "E233.top", {"start": v(5359.4, 4076.7) * mm, "end": v(6426.2, 4076.7) * mm});
            skLineSegment(sketch, "E233.left", {"start": v(5359.4, 4013.2) * mm, "end": v(5359.4, 4076.7) * mm});
            skLineSegment(sketch, "E233.right", {"start": v(6426.2, 4013.2) * mm, "end": v(6426.2, 4076.7) * mm});
            skLineSegment(sketch, "E234.bottom", {"start": v(7797.8, 3556) * mm, "end": v(8864.6, 3556) * mm});
            skLineSegment(sketch, "E234.top", {"start": v(7797.8, 3619.5) * mm, "end": v(8864.6, 3619.5) * mm});
            skLineSegment(sketch, "E234.left", {"start": v(7797.8, 3556) * mm, "end": v(7797.8, 3619.5) * mm});
            skLineSegment(sketch, "E234.right", {"start": v(8864.6, 3556) * mm, "end": v(8864.6, 3619.5) * mm});
            skLineSegment(sketch, "E235.bottom", {"start": v(9626.6, 3556) * mm, "end": v(10693.4, 3556) * mm});
            skLineSegment(sketch, "E235.top", {"start": v(9626.6, 3619.5) * mm, "end": v(10693.4, 3619.5) * mm});
            skLineSegment(sketch, "E235.left", {"start": v(9626.6, 3556) * mm, "end": v(9626.6, 3619.5) * mm});
            skLineSegment(sketch, "E235.right", {"start": v(10693.4, 3556) * mm, "end": v(10693.4, 3619.5) * mm});
            skSolve(sketch);
        }
        {
            var Q0;
            Q0 = qSketchRegion(id + "F126", true);
            extrude(context, id + "F127", {"entities" : qUnion([Q0]), "operationType" : NewBodyOperationType.ADD, "depth" : 88.9 * mm});
        }
        {
            var Q0;
            Q0=makeQuery(id+"F32.boolean.opBoolean","COPY",FACE,{"derivedFrom":makeQuery(id+"F32.opExtrude","CAP_FACE",FACE,{"disambiguationData":[OSD([sQuery(id+"F21.wireOp",EDGE,"E37"),sQuery(id+"F31.wireOp",EDGE,"E52.0"),sQuery(id+"F31.wireOp",EDGE,"E52.1"),sQuery(id+"F31.wireOp",EDGE,"E52.2"),sQuery(id+"F31.wireOp",EDGE,"E52.3")])],"isStart":false})});
            var sketch = newSketch(context, id + "F128", { "sketchPlane" : qUnion([Q0])});
            skLineSegment(sketch, "E236.bottom", {"start": v(6908.8, 1071.47) * mm, "end": v(7772.4, 1071.47) * mm});
            skLineSegment(sketch, "E236.top", {"start": v(6908.8, 1134.97) * mm, "end": v(7772.4, 1134.97) * mm});
            skLineSegment(sketch, "E236.left", {"start": v(6908.8, 1071.47) * mm, "end": v(6908.8, 1134.97) * mm});
            skLineSegment(sketch, "E236.right", {"start": v(7772.4, 1071.47) * mm, "end": v(7772.4, 1134.97) * mm});
            skSolve(sketch);
        }
        {
            var Q0;
            Q0 = qSketchRegion(id + "F128", true);
            extrude(context, id + "F129", {"entities" : qUnion([Q0]), "operationType" : NewBodyOperationType.ADD, "depth" : 88.9 * mm});
        }
        {
            var Q0;
            Q0=makeQuery(id+"F14.boolean.opBoolean","COPY",FACE,{"derivedFrom":makeQuery(id+"F14.opExtrude","CAP_FACE",FACE,{"disambiguationData":[OSD([sQuery(id+"F0.wireOp",EDGE,"E0.top"),sQuery(id+"F13.wireOp",EDGE,"E8"),sQuery(id+"F13.wireOp",EDGE,"E9"),sQuery(id+"F13.wireOp",EDGE,"E10")])],"isStart":false})});
            var sketch = newSketch(context, id + "F130", { "sketchPlane" : qUnion([Q0])});
            skLineSegment(sketch, "E237.bottom", {"start": v(-11582.4, 0) * mm, "end": v(-6883.4, 0) * mm});
            skLineSegment(sketch, "E237.top", {"start": v(-11582.4, 101.6) * mm, "end": v(-6883.4, 101.6) * mm});
            skLineSegment(sketch, "E237.left", {"start": v(-11582.4, 0) * mm, "end": v(-11582.4, 101.6) * mm});
            skLineSegment(sketch, "E237.right", {"start": v(-6883.4, 0) * mm, "end": v(-6883.4, 101.6) * mm});
            skLineSegment(sketch, "E238.bottom", {"start": v(-203.2, 0) * mm, "end": v(-4902.2, 0) * mm});
            skLineSegment(sketch, "E238.top", {"start": v(-203.2, 101.6) * mm, "end": v(-4902.2, 101.6) * mm});
            skLineSegment(sketch, "E238.left", {"start": v(-203.2, 0) * mm, "end": v(-203.2, 101.6) * mm});
            skLineSegment(sketch, "E238.right", {"start": v(-4902.2, 0) * mm, "end": v(-4902.2, 101.6) * mm});
            skSolve(sketch);
        }
        {
            var Q0;
            Q0 = qSketchRegion(id + "F130", true);
            extrude(context, id + "F131", {"entities" : qUnion([Q0]), "operationType" : NewBodyOperationType.ADD, "depth" : 19.05 * mm});
        }
        {
            var Q0;
            Q0=makeQuery(id+"F12.boolean.opBoolean","COPY",FACE,{"derivedFrom":makeQuery(id+"F12.opExtrude","CAP_FACE",FACE,{"disambiguationData":[OSD([sQuery(id+"F11.wireOp",EDGE,"E7.0.0"),sQuery(id+"F11.wireOp",EDGE,"E7.0.1"),sQuery(id+"F11.wireOp",EDGE,"E7.0.2"),sQuery(id+"F11.wireOp",EDGE,"E7.0.3")])],"isStart":false})});
            var sketch = newSketch(context, id + "F132", { "sketchPlane" : qUnion([Q0])});
            skLineSegment(sketch, "E239.bottom", {"start": v(-11582.4, 0) * mm, "end": v(-7239, 0) * mm});
            skLineSegment(sketch, "E239.top", {"start": v(-11582.4, 101.6) * mm, "end": v(-7239, 101.6) * mm});
            skLineSegment(sketch, "E239.left", {"start": v(-11582.4, 0) * mm, "end": v(-11582.4, 101.6) * mm});
            skLineSegment(sketch, "E239.right", {"start": v(-7239, 0) * mm, "end": v(-7239, 101.6) * mm});
            skLineSegment(sketch, "E240.bottom", {"start": v(-203.2, 0) * mm, "end": v(-5003.8, 0) * mm});
            skLineSegment(sketch, "E240.top", {"start": v(-203.2, 101.6) * mm, "end": v(-5003.8, 101.6) * mm});
            skLineSegment(sketch, "E240.left", {"start": v(-203.2, 0) * mm, "end": v(-203.2, 101.6) * mm});
            skLineSegment(sketch, "E240.right", {"start": v(-5003.8, 0) * mm, "end": v(-5003.8, 101.6) * mm});
            skSolve(sketch);
        }
        {
            var Q0;
            Q0 = qSketchRegion(id + "F132", true);
            extrude(context, id + "F133", {"entities" : qUnion([Q0]), "operationType" : NewBodyOperationType.ADD, "depth" : 19.05 * mm});
        }
        {
            var Q0;
            {var subQ0=sQuery(id+"F76.wireOp",EDGE,"E127.right");var subQ1=sQuery(id+"F76.wireOp",EDGE,"E127.left");var subQ2=sQuery(id+"F76.wireOp",EDGE,"E127.top");var subQ3=sQuery(id+"F76.wireOp",EDGE,"E127.bottom");Q0=makeQuery(id+"F79.boolean.opBoolean","MERGE",FACE,{"derivedFrom":[makeQuery(id+"F77.opExtrude","CAP_FACE",FACE,{"disambiguationData":[OSD([subQ3,subQ2,subQ1,subQ0])],"isStart":true}),makeQuery(id+"F79.opExtrude","CAP_FACE",FACE,{"disambiguationData":[OSD([subQ3,subQ2,subQ1,subQ0])],"isStart":false})]});}
            var sketch = newSketch(context, id + "F134", { "sketchPlane" : qUnion([Q0])});
            skLineSegment(sketch, "E241.0", {"start": v(279.4, -279.4) * mm, "end": v(279.4, -11506.2) * mm});
            skLineSegment(sketch, "E241.1", {"start": v(11506.2, -279.4) * mm, "end": v(279.4, -279.4) * mm});
            skLineSegment(sketch, "E241.2", {"start": v(279.4, -11506.2) * mm, "end": v(11506.2, -11506.2) * mm});
            skLineSegment(sketch, "E241.3", {"start": v(11506.2, -4318) * mm, "end": v(11506.2, -279.4) * mm});
            skLineSegment(sketch, "E241.4", {"start": v(11506.2, -11506.2) * mm, "end": v(11506.2, -8534.4) * mm});
            skLineSegment(sketch, "E241.5", {"start": v(11506.2, -8534.4) * mm, "end": v(18643.6, -8534.4) * mm});
            skLineSegment(sketch, "E241.6", {"start": v(18643.6, -8534.4) * mm, "end": v(18643.6, -4318) * mm});
            skLineSegment(sketch, "E241.7", {"start": v(18643.6, -4318) * mm, "end": v(11506.2, -4318) * mm});
            skSolve(sketch);
        }
        {
            var Q0;
            Q0=makeQuery(id+"F134.imprint","IMPRINT",FACE,{"disambiguationData":[TD([[makeQuery(id+"F134.imprint","IMPRINT",EDGE,{"derivedFrom":sQuery(id+"F134.wireOp",EDGE,"E241.0")}),1.0]])]});
            extrude(context, id + "F135", {"entities" : qUnion([Q0]), "operationType" : NewBodyOperationType.REMOVE, "oppositeDirection" : true, "depth" : 2540 * mm});
        }
        {
            var Q0;
            Q0=makeQuery(id+"F39.opShell","OFFSET_FACE",FACE,{"disambiguationData":[OSD([sQuery(id+"F17.wireOp",EDGE,"E13.bottom"),sQuery(id+"F17.wireOp",EDGE,"E13.top"),sQuery(id+"F17.wireOp",EDGE,"E13.left"),sQuery(id+"F17.wireOp",EDGE,"E13.right")])]});
            var Q1;
            Q1=makeQuery(id+"F39.opShell","OFFSET_FACE",FACE,{"disambiguationData":[OSD([sQuery(id+"F17.wireOp",EDGE,"E14.bottom"),sQuery(id+"F17.wireOp",EDGE,"E14.top"),sQuery(id+"F17.wireOp",EDGE,"E14.left"),sQuery(id+"F17.wireOp",EDGE,"E14.right")])]});
            var Q2;
            Q2=makeQuery(id+"F39.opShell","OFFSET_FACE",FACE,{"disambiguationData":[OSD([sQuery(id+"F17.wireOp",EDGE,"E15.bottom"),sQuery(id+"F17.wireOp",EDGE,"E15.top"),sQuery(id+"F17.wireOp",EDGE,"E15.left"),sQuery(id+"F17.wireOp",EDGE,"E15.right")])]});
            var Q3;
            Q3=makeQuery(id+"F39.opShell","OFFSET_FACE",FACE,{"disambiguationData":[OSD([sQuery(id+"F17.wireOp",EDGE,"E16.bottom"),sQuery(id+"F17.wireOp",EDGE,"E16.top"),sQuery(id+"F17.wireOp",EDGE,"E16.left"),sQuery(id+"F17.wireOp",EDGE,"E16.right")])]});
            var Q4;
            Q4=makeQuery(id+"F39.opShell","OFFSET_FACE",FACE,{"disambiguationData":[OSD([sQuery(id+"F17.wireOp",EDGE,"E17.bottom"),sQuery(id+"F17.wireOp",EDGE,"E17.top"),sQuery(id+"F17.wireOp",EDGE,"E17.left"),sQuery(id+"F17.wireOp",EDGE,"E17.right")])]});
            var Q5;
            Q5=makeQuery(id+"F39.opShell","OFFSET_FACE",FACE,{"disambiguationData":[OSD([sQuery(id+"F17.wireOp",EDGE,"E18.bottom"),sQuery(id+"F17.wireOp",EDGE,"E18.top"),sQuery(id+"F17.wireOp",EDGE,"E18.left"),sQuery(id+"F17.wireOp",EDGE,"E18.right")])]});
            var Q6;
            Q6=makeQuery(id+"F39.opShell","OFFSET_FACE",FACE,{"disambiguationData":[OSD([sQuery(id+"F17.wireOp",EDGE,"E19.bottom"),sQuery(id+"F17.wireOp",EDGE,"E19.top"),sQuery(id+"F17.wireOp",EDGE,"E19.left"),sQuery(id+"F17.wireOp",EDGE,"E19.right")])]});
            var Q7;
            Q7=makeQuery(id+"F39.opShell","OFFSET_FACE",FACE,{"disambiguationData":[OSD([sQuery(id+"F17.wireOp",EDGE,"E20.bottom"),sQuery(id+"F17.wireOp",EDGE,"E20.top"),sQuery(id+"F17.wireOp",EDGE,"E20.left"),sQuery(id+"F17.wireOp",EDGE,"E20.right")])]});
            var Q8;
            Q8=makeQuery(id+"F39.opShell","OFFSET_FACE",FACE,{"disambiguationData":[OSD([sQuery(id+"F17.wireOp",EDGE,"E21.bottom"),sQuery(id+"F17.wireOp",EDGE,"E21.top"),sQuery(id+"F17.wireOp",EDGE,"E21.left"),sQuery(id+"F17.wireOp",EDGE,"E21.right")])]});
            extrude(context, id + "F136", {"entities" : qUnion([Q0, Q1, Q2, Q3, Q4, Q5, Q6, Q7, Q8]), "operationType" : NewBodyOperationType.ADD, "depth" : 50.8 * mm});
        }
        {
            var Q0;
            Q0=makeQuery(id+"F39.opShell","OFFSET_FACE",FACE,{"disambiguationData":[OSD([sQuery(id+"F25.wireOp",EDGE,"E40.0.0"),sQuery(id+"F25.wireOp",EDGE,"E40.0.1"),sQuery(id+"F25.wireOp",EDGE,"E40.0.2"),sQuery(id+"F25.wireOp",EDGE,"E40.0.3")])]});
            var Q1;
            Q1=makeQuery(id+"F39.opShell","OFFSET_FACE",FACE,{"disambiguationData":[OSD([sQuery(id+"F25.wireOp",EDGE,"E40.1.0"),sQuery(id+"F25.wireOp",EDGE,"E40.1.1"),sQuery(id+"F25.wireOp",EDGE,"E40.1.2"),sQuery(id+"F25.wireOp",EDGE,"E40.1.3")])]});
            var Q2;
            Q2=makeQuery(id+"F39.opShell","OFFSET_FACE",FACE,{"disambiguationData":[OSD([sQuery(id+"F25.wireOp",EDGE,"E43.bottom"),sQuery(id+"F25.wireOp",EDGE,"E43.top"),sQuery(id+"F25.wireOp",EDGE,"E43.left"),sQuery(id+"F25.wireOp",EDGE,"E43.right")])]});
            var Q3;
            Q3=makeQuery(id+"F39.opShell","OFFSET_FACE",FACE,{"disambiguationData":[OSD([sQuery(id+"F25.wireOp",EDGE,"E40.4.0"),sQuery(id+"F25.wireOp",EDGE,"E40.4.1"),sQuery(id+"F25.wireOp",EDGE,"E40.4.2"),sQuery(id+"F25.wireOp",EDGE,"E40.4.3")])]});
            var Q4;
            Q4=makeQuery(id+"F39.opShell","OFFSET_FACE",FACE,{"disambiguationData":[OSD([sQuery(id+"F25.wireOp",EDGE,"E45.bottom"),sQuery(id+"F25.wireOp",EDGE,"E45.top"),sQuery(id+"F25.wireOp",EDGE,"E45.left"),sQuery(id+"F25.wireOp",EDGE,"E45.right")])]});
            var Q5;
            Q5=makeQuery(id+"F39.opShell","OFFSET_FACE",FACE,{"disambiguationData":[OSD([sQuery(id+"F25.wireOp",EDGE,"E40.3.0"),sQuery(id+"F25.wireOp",EDGE,"E40.3.1"),sQuery(id+"F25.wireOp",EDGE,"E40.3.2"),sQuery(id+"F25.wireOp",EDGE,"E40.3.3")])]});
            var Q6;
            Q6=makeQuery(id+"F39.opShell","OFFSET_FACE",FACE,{"disambiguationData":[OSD([sQuery(id+"F25.wireOp",EDGE,"E40.2.0"),sQuery(id+"F25.wireOp",EDGE,"E40.2.1"),sQuery(id+"F25.wireOp",EDGE,"E40.2.2"),sQuery(id+"F25.wireOp",EDGE,"E40.2.3")])]});
            var Q7;
            Q7=makeQuery(id+"F39.opShell","OFFSET_FACE",FACE,{"disambiguationData":[OSD([sQuery(id+"F25.wireOp",EDGE,"E44.bottom"),sQuery(id+"F25.wireOp",EDGE,"E44.top"),sQuery(id+"F25.wireOp",EDGE,"E44.left"),sQuery(id+"F25.wireOp",EDGE,"E44.right")])]});
            var Q8;
            Q8=makeQuery(id+"F39.opShell","OFFSET_FACE",FACE,{"disambiguationData":[OSD([sQuery(id+"F25.wireOp",EDGE,"E42.bottom"),sQuery(id+"F25.wireOp",EDGE,"E42.top"),sQuery(id+"F25.wireOp",EDGE,"E42.left"),sQuery(id+"F25.wireOp",EDGE,"E42.right")])]});
            var Q9;
            Q9=makeQuery(id+"F39.opShell","OFFSET_FACE",FACE,{"disambiguationData":[OSD([sQuery(id+"F25.wireOp",EDGE,"E41.bottom"),sQuery(id+"F25.wireOp",EDGE,"E41.top"),sQuery(id+"F25.wireOp",EDGE,"E41.left"),sQuery(id+"F25.wireOp",EDGE,"E41.right")])]});
            extrude(context, id + "F137", {"entities" : qUnion([Q0, Q1, Q2, Q3, Q4, Q5, Q6, Q7, Q8, Q9]), "operationType" : NewBodyOperationType.ADD, "depth" : 50.8 * mm});
        }
        {
            var Q0;
            Q0=makeQuery(id+"F39.opShell","OFFSET_FACE",FACE,{"disambiguationData":[OSD([sQuery(id+"F23.wireOp",EDGE,"E39.0.0"),sQuery(id+"F23.wireOp",EDGE,"E39.0.1"),sQuery(id+"F23.wireOp",EDGE,"E39.0.2"),sQuery(id+"F23.wireOp",EDGE,"E39.0.3")])]});
            var Q1;
            Q1=makeQuery(id+"F39.opShell","OFFSET_FACE",FACE,{"disambiguationData":[OSD([sQuery(id+"F23.wireOp",EDGE,"E39.1.0"),sQuery(id+"F23.wireOp",EDGE,"E39.1.1"),sQuery(id+"F23.wireOp",EDGE,"E39.1.2"),sQuery(id+"F23.wireOp",EDGE,"E39.1.3")])]});
            var Q2;
            Q2=makeQuery(id+"F39.opShell","OFFSET_FACE",FACE,{"disambiguationData":[OSD([sQuery(id+"F23.wireOp",EDGE,"E39.2.0"),sQuery(id+"F23.wireOp",EDGE,"E39.2.1"),sQuery(id+"F23.wireOp",EDGE,"E39.2.2"),sQuery(id+"F23.wireOp",EDGE,"E39.2.3")])]});
            var Q3;
            Q3=makeQuery(id+"F39.opShell","OFFSET_FACE",FACE,{"disambiguationData":[OSD([sQuery(id+"F23.wireOp",EDGE,"E39.3.0"),sQuery(id+"F23.wireOp",EDGE,"E39.3.1"),sQuery(id+"F23.wireOp",EDGE,"E39.3.2"),sQuery(id+"F23.wireOp",EDGE,"E39.3.3")])]});
            var Q4;
            Q4=makeQuery(id+"F39.opShell","OFFSET_FACE",FACE,{"disambiguationData":[OSD([sQuery(id+"F23.wireOp",EDGE,"E39.4.0"),sQuery(id+"F23.wireOp",EDGE,"E39.4.1"),sQuery(id+"F23.wireOp",EDGE,"E39.4.2"),sQuery(id+"F23.wireOp",EDGE,"E39.4.3")])]});
            var Q5;
            Q5=makeQuery(id+"F39.opShell","OFFSET_FACE",FACE,{"disambiguationData":[OSD([sQuery(id+"F23.wireOp",EDGE,"E39.5.0"),sQuery(id+"F23.wireOp",EDGE,"E39.5.1"),sQuery(id+"F23.wireOp",EDGE,"E39.5.2"),sQuery(id+"F23.wireOp",EDGE,"E39.5.3")])]});
            var Q6;
            Q6=makeQuery(id+"F39.opShell","OFFSET_FACE",FACE,{"disambiguationData":[OSD([sQuery(id+"F23.wireOp",EDGE,"E39.6.0"),sQuery(id+"F23.wireOp",EDGE,"E39.6.1"),sQuery(id+"F23.wireOp",EDGE,"E39.6.2"),sQuery(id+"F23.wireOp",EDGE,"E39.6.3")])]});
            var Q7;
            Q7=makeQuery(id+"F39.opShell","OFFSET_FACE",FACE,{"disambiguationData":[OSD([sQuery(id+"F23.wireOp",EDGE,"E39.8.0"),sQuery(id+"F23.wireOp",EDGE,"E39.8.1"),sQuery(id+"F23.wireOp",EDGE,"E39.8.2"),sQuery(id+"F23.wireOp",EDGE,"E39.8.3")])]});
            var Q8;
            Q8=makeQuery(id+"F39.opShell","OFFSET_FACE",FACE,{"disambiguationData":[OSD([sQuery(id+"F23.wireOp",EDGE,"E39.9.0"),sQuery(id+"F23.wireOp",EDGE,"E39.9.1"),sQuery(id+"F23.wireOp",EDGE,"E39.9.2"),sQuery(id+"F23.wireOp",EDGE,"E39.9.3")])]});
            extrude(context, id + "F138", {"entities" : qUnion([Q0, Q1, Q2, Q3, Q4, Q5, Q6, Q7, Q8]), "operationType" : NewBodyOperationType.ADD, "depth" : 50.8 * mm});
        }
        {
            var Q0;
            {var subQ0=sQuery(id+"F21.wireOp",EDGE,"E36");Q0=makeQuery(id+"F39.opShell","OFFSET_FACE",FACE,{"disambiguationData":[OSD([subQ0]),TDD([makeQuery(id+"F38.boolean.opBoolean","SPLIT",FACE,{"disambiguationData":[TD([makeQuery(id+"F38.opExtrude","SWEPT_FACE",FACE,{"disambiguationData":[OSD([sQuery(id+"F35.wireOp",EDGE,"E54.0.0")])]})])],"derivedFrom":makeQuery(id+"F22.opExtrude","SWEPT_FACE",FACE,{"disambiguationData":[OSD([subQ0])]})})])]});}
            var Q1;
            {var subQ0=sQuery(id+"F21.wireOp",EDGE,"E36");Q1=makeQuery(id+"F39.opShell","OFFSET_FACE",FACE,{"disambiguationData":[OSD([subQ0]),TDD([makeQuery(id+"F38.boolean.opBoolean","SPLIT",FACE,{"disambiguationData":[TD([makeQuery(id+"F38.opExtrude","SWEPT_FACE",FACE,{"disambiguationData":[OSD([sQuery(id+"F35.wireOp",EDGE,"E55.bottom")])]})])],"derivedFrom":makeQuery(id+"F22.opExtrude","SWEPT_FACE",FACE,{"disambiguationData":[OSD([subQ0])]})})])]});}
            var Q2;
            {var subQ0=sQuery(id+"F21.wireOp",EDGE,"E36");Q2=makeQuery(id+"F39.opShell","OFFSET_FACE",FACE,{"disambiguationData":[OSD([subQ0]),TDD([makeQuery(id+"F38.boolean.opBoolean","SPLIT",FACE,{"disambiguationData":[TD([makeQuery(id+"F38.opExtrude","SWEPT_FACE",FACE,{"disambiguationData":[OSD([sQuery(id+"F35.wireOp",EDGE,"E56.bottom")])]})])],"derivedFrom":makeQuery(id+"F22.opExtrude","SWEPT_FACE",FACE,{"disambiguationData":[OSD([subQ0])]})})])]});}
            extrude(context, id + "F139", {"entities" : qUnion([Q0, Q1, Q2]), "operationType" : NewBodyOperationType.ADD, "depth" : 50.8 * mm});
        }
        {
            var Q0;
            Q0=makeQuery(id+"F39.opShell","OFFSET_FACE",FACE,{"disambiguationData":[OSD([sQuery(id+"F19.wireOp",EDGE,"E27.bottom"),sQuery(id+"F19.wireOp",EDGE,"E27.top"),sQuery(id+"F19.wireOp",EDGE,"E27.left"),sQuery(id+"F19.wireOp",EDGE,"E27.right")])]});
            var Q1;
            Q1=makeQuery(id+"F39.opShell","OFFSET_FACE",FACE,{"disambiguationData":[OSD([sQuery(id+"F19.wireOp",EDGE,"E26.bottom"),sQuery(id+"F19.wireOp",EDGE,"E26.top"),sQuery(id+"F19.wireOp",EDGE,"E26.left"),sQuery(id+"F19.wireOp",EDGE,"E26.right")])]});
            var Q2;
            Q2=makeQuery(id+"F39.opShell","OFFSET_FACE",FACE,{"disambiguationData":[OSD([sQuery(id+"F19.wireOp",EDGE,"E25.bottom"),sQuery(id+"F19.wireOp",EDGE,"E25.left"),sQuery(id+"F19.wireOp",EDGE,"E25.right"),sQuery(id+"F19.wireOp",EDGE,"E31")])]});
            var Q3;
            Q3=makeQuery(id+"F39.opShell","OFFSET_FACE",FACE,{"disambiguationData":[OSD([sQuery(id+"F19.wireOp",EDGE,"E24.bottom"),sQuery(id+"F19.wireOp",EDGE,"E24.top"),sQuery(id+"F19.wireOp",EDGE,"E24.left"),sQuery(id+"F19.wireOp",EDGE,"E24.right")])]});
            var Q4;
            Q4=makeQuery(id+"F39.opShell","OFFSET_FACE",FACE,{"disambiguationData":[OSD([sQuery(id+"F19.wireOp",EDGE,"E23.bottom"),sQuery(id+"F19.wireOp",EDGE,"E23.top"),sQuery(id+"F19.wireOp",EDGE,"E23.left"),sQuery(id+"F19.wireOp",EDGE,"E23.right")])]});
            var Q5;
            Q5=makeQuery(id+"F39.opShell","OFFSET_FACE",FACE,{"disambiguationData":[OSD([sQuery(id+"F19.wireOp",EDGE,"E30.bottom"),sQuery(id+"F19.wireOp",EDGE,"E30.top"),sQuery(id+"F19.wireOp",EDGE,"E30.left"),sQuery(id+"F19.wireOp",EDGE,"E30.right")])]});
            var Q6;
            Q6=makeQuery(id+"F39.opShell","OFFSET_FACE",FACE,{"disambiguationData":[OSD([sQuery(id+"F19.wireOp",EDGE,"E29.bottom"),sQuery(id+"F19.wireOp",EDGE,"E29.top"),sQuery(id+"F19.wireOp",EDGE,"E29.left"),sQuery(id+"F19.wireOp",EDGE,"E29.right")])]});
            extrude(context, id + "F140", {"entities" : qUnion([Q0, Q1, Q2, Q3, Q4, Q5, Q6]), "operationType" : NewBodyOperationType.ADD, "depth" : 50.8 * mm});
        }
        {
            var Q0;
            Q0=makeQuery(id+"F39.opShell","OFFSET_FACE",FACE,{"disambiguationData":[OSD([sQuery(id+"F29.wireOp",EDGE,"E50.bottom"),sQuery(id+"F29.wireOp",EDGE,"E50.top"),sQuery(id+"F29.wireOp",EDGE,"E50.left"),sQuery(id+"F29.wireOp",EDGE,"E50.right")])]});
            var Q1;
            Q1=makeQuery(id+"F39.opShell","OFFSET_FACE",FACE,{"disambiguationData":[OSD([sQuery(id+"F29.wireOp",EDGE,"E51.bottom"),sQuery(id+"F29.wireOp",EDGE,"E51.top"),sQuery(id+"F29.wireOp",EDGE,"E51.left"),sQuery(id+"F29.wireOp",EDGE,"E51.right")])]});
            extrude(context, id + "F141", {"entities" : qUnion([Q0, Q1]), "operationType" : NewBodyOperationType.ADD, "depth" : 50.8 * mm});
        }
        {
            var Q0;
            Q0=makeQuery(id+"F39.opShell","OFFSET_FACE",FACE,{"disambiguationData":[OSD([sQuery(id+"F33.wireOp",EDGE,"E53.bottom"),sQuery(id+"F33.wireOp",EDGE,"E53.top"),sQuery(id+"F33.wireOp",EDGE,"E53.left"),sQuery(id+"F33.wireOp",EDGE,"E53.right")])]});
            extrude(context, id + "F142", {"entities" : qUnion([Q0]), "operationType" : NewBodyOperationType.ADD, "depth" : 50.8 * mm});
        }
        {
            var Q0;
            Q0=makeQuery(id+"F65.boolean.opBoolean","COPY",FACE,{"derivedFrom":makeQuery(id+"F65.opExtrude","CAP_FACE",FACE,{"disambiguationData":[OSD([sQuery(id+"F64.wireOp",EDGE,"E114.bottom"),sQuery(id+"F64.wireOp",EDGE,"E114.top"),sQuery(id+"F64.wireOp",EDGE,"E114.left"),sQuery(id+"F64.wireOp",EDGE,"E114.right")])],"isStart":false})});
            var sketch = newSketch(context, id + "F143", { "sketchPlane" : qUnion([Q0])});
            skLineSegment(sketch, "E242.bottom", {"start": v(5054.6, 1041.4) * mm, "end": v(5334, 1041.4) * mm});
            skLineSegment(sketch, "E242.top", {"start": v(5054.6, 965.2) * mm, "end": v(5334, 965.2) * mm});
            skLineSegment(sketch, "E242.left", {"start": v(5054.6, 1041.4) * mm, "end": v(5054.6, 965.2) * mm});
            skLineSegment(sketch, "E242.right", {"start": v(5334, 1041.4) * mm, "end": v(5334, 965.2) * mm});
            skPoint(sketch, "E243.firstSnap0", {"position": v(5194.3, 1041.4) * mm});
            skLineSegment(sketch, "E243.bottom", {"start": v(6441.29, 1041.4) * mm, "end": v(6754.26, 1041.4) * mm});
            skLineSegment(sketch, "E243.top", {"start": v(6441.29, 965.2) * mm, "end": v(6754.26, 965.2) * mm});
            skLineSegment(sketch, "E243.left", {"start": v(6441.29, 1041.4) * mm, "end": v(6441.29, 965.2) * mm});
            skLineSegment(sketch, "E243.right", {"start": v(6754.26, 1041.4) * mm, "end": v(6754.26, 965.2) * mm});
            skSolve(sketch);
        }
        {
            var Q0;
            Q0 = qSketchRegion(id + "F143", true);
            extrude(context, id + "F144", {"entities" : qUnion([Q0]), "operationType" : NewBodyOperationType.ADD, "depth" : 25.4 * mm});
        }
        {
            var Q0;
            Q0=makeQuery(id+"F67.boolean.opBoolean","COPY",FACE,{"derivedFrom":makeQuery(id+"F67.opExtrude","CAP_FACE",FACE,{"disambiguationData":[OSD([sQuery(id+"F66.wireOp",EDGE,"E117.2.0"),sQuery(id+"F66.wireOp",EDGE,"E117.2.1"),sQuery(id+"F66.wireOp",EDGE,"E117.2.2"),sQuery(id+"F66.wireOp",EDGE,"E117.2.3")])],"isStart":false})});
            var sketch = newSketch(context, id + "F145", { "sketchPlane" : qUnion([Q0])});
            skLineSegment(sketch, "E244.0.0", {"start": v(-5054.6, 1041.4) * mm, "end": v(-5054.6, 965.2) * mm});
            skLineSegment(sketch, "E244.0.1", {"start": v(-5054.6, 965.2) * mm, "end": v(-5334, 965.2) * mm});
            skLineSegment(sketch, "E244.0.2", {"start": v(-5334, 965.2) * mm, "end": v(-5334, 1041.4) * mm});
            skLineSegment(sketch, "E244.0.3", {"start": v(-5334, 1041.4) * mm, "end": v(-5054.6, 1041.4) * mm});
            skLineSegment(sketch, "E245.0.0", {"start": v(-6451.6, 1041.4) * mm, "end": v(-6451.6, 965.2) * mm});
            skLineSegment(sketch, "E245.0.1", {"start": v(-6451.6, 965.2) * mm, "end": v(-6731, 965.2) * mm});
            skLineSegment(sketch, "E245.0.2", {"start": v(-6731, 965.2) * mm, "end": v(-6731, 1041.4) * mm});
            skLineSegment(sketch, "E245.0.3", {"start": v(-6731, 1041.4) * mm, "end": v(-6451.6, 1041.4) * mm});
            skSolve(sketch);
        }
        {
            var Q0;
            Q0 = qSketchRegion(id + "F145", true);
            extrude(context, id + "F146", {"entities" : qUnion([Q0]), "operationType" : NewBodyOperationType.ADD, "depth" : 25.4 * mm});
        }
        {
            var Q0;
            Q0=makeQuery(id+"F16.boolean.opBoolean","COPY",FACE,{"derivedFrom":makeQuery(id+"F16.opExtrude","CAP_FACE",FACE,{"disambiguationData":[OSD([sQuery(id+"F15.wireOp",EDGE,"E11.0.0"),sQuery(id+"F15.wireOp",EDGE,"E11.0.1"),sQuery(id+"F15.wireOp",EDGE,"E11.0.2"),sQuery(id+"F15.wireOp",EDGE,"E11.0.3")])],"isStart":false})});
            var sketch = newSketch(context, id + "F147", { "sketchPlane" : qUnion([Q0])});
            skLineSegment(sketch, "E246.bottom", {"start": v(203.2, 0) * mm, "end": v(4902.2, 0) * mm});
            skLineSegment(sketch, "E246.top", {"start": v(203.2, 101.6) * mm, "end": v(4902.2, 101.6) * mm});
            skLineSegment(sketch, "E246.left", {"start": v(203.2, 0) * mm, "end": v(203.2, 101.6) * mm});
            skLineSegment(sketch, "E246.right", {"start": v(4902.2, 0) * mm, "end": v(4902.2, 101.6) * mm});
            skLineSegment(sketch, "E247.bottom", {"start": v(11582.4, 0) * mm, "end": v(6883.4, 0) * mm});
            skLineSegment(sketch, "E247.top", {"start": v(11582.4, 101.6) * mm, "end": v(6883.4, 101.6) * mm});
            skLineSegment(sketch, "E247.left", {"start": v(11582.4, 0) * mm, "end": v(11582.4, 101.6) * mm});
            skLineSegment(sketch, "E247.right", {"start": v(6883.4, 0) * mm, "end": v(6883.4, 101.6) * mm});
            skSolve(sketch);
        }
        {
            var Q0;
            Q0 = qSketchRegion(id + "F147", true);
            extrude(context, id + "F148", {"entities" : qUnion([Q0]), "operationType" : NewBodyOperationType.ADD, "depth" : 19.05 * mm});
        }
        {
            var Q0;
            Q0=makeQuery(id+"F79.opExtrude","SWEPT_FACE",FACE,{"disambiguationData":[OSD([sQuery(id+"F78.wireOp",EDGE,"E128.top")])]});
            var sketch = newSketch(context, id + "F149", { "sketchPlane" : qUnion([Q0])});
            skLineSegment(sketch, "E248.bottom", {"start": v(11709.4, -101.6) * mm, "end": v(18796, -101.6) * mm});
            skLineSegment(sketch, "E248.top", {"start": v(11709.4, -304.8) * mm, "end": v(18796, -304.8) * mm});
            skLineSegment(sketch, "E248.left", {"start": v(11709.4, -101.6) * mm, "end": v(11709.4, -304.8) * mm});
            skLineSegment(sketch, "E248.right", {"start": v(18796, -101.6) * mm, "end": v(18796, -304.8) * mm});
            skSolve(sketch);
        }
        {
            var Q0;
            Q0 = qSketchRegion(id + "F149", true);
            extrude(context, id + "F150", {"entities" : qUnion([Q0]), "operationType" : NewBodyOperationType.ADD, "depth" : 2006.6 * mm});
        }
        {
            var Q0;
            Q0=makeQuery(id+"F150.opExtrude","CAP_FACE",FACE,{"disambiguationData":[OSD([sQuery(id+"F149.wireOp",EDGE,"E248.bottom"),sQuery(id+"F149.wireOp",EDGE,"E248.top"),sQuery(id+"F149.wireOp",EDGE,"E248.left"),sQuery(id+"F149.wireOp",EDGE,"E248.right")])],"isStart":false});
            var sketch = newSketch(context, id + "F151", { "sketchPlane" : qUnion([Q0])});
            skLineSegment(sketch, "E249.bottom", {"start": v(12420.6, -304.8) * mm, "end": v(13944.6, -304.8) * mm});
            skLineSegment(sketch, "E249.top", {"start": v(12420.6, -127) * mm, "end": v(13944.6, -127) * mm});
            skLineSegment(sketch, "E249.left", {"start": v(12420.6, -304.8) * mm, "end": v(12420.6, -127) * mm});
            skLineSegment(sketch, "E249.right", {"start": v(13944.6, -304.8) * mm, "end": v(13944.6, -127) * mm});
            skSolve(sketch);
        }
        {
            var Q0;
            Q0 = qSketchRegion(id + "F151", true);
            extrude(context, id + "F152", {"entities" : qUnion([Q0]), "operationType" : NewBodyOperationType.ADD, "depth" : 965.2 * mm});
        }
        {
            var Q0;
            Q0=makeQuery(id+"F150.opExtrude","SWEPT_FACE",FACE,{"disambiguationData":[OSD([sQuery(id+"F149.wireOp",EDGE,"E248.bottom")])]});
            var sketch = newSketch(context, id + "F153", { "sketchPlane" : qUnion([Q0])});
            skLineSegment(sketch, "E250.bottom", {"start": v(14020.8, 2108.2) * mm, "end": v(18846.8, 2108.2) * mm});
            skLineSegment(sketch, "E250.top", {"start": v(14020.8, 1955.8) * mm, "end": v(18846.8, 1955.8) * mm});
            skLineSegment(sketch, "E250.left", {"start": v(14020.8, 2108.2) * mm, "end": v(14020.8, 1955.8) * mm});
            skLineSegment(sketch, "E251", {"start": v(18846.8, 2108.2) * mm, "end": v(18846.8, 1955.8) * mm});
            skPoint(sketch, "E252.orphan", {"position": v(18796, 1955.8) * mm});
            skSolve(sketch);
        }
        {
            var Q0;
            Q0 = qSketchRegion(id + "F153", true);
            extrude(context, id + "F154", {"entities" : qUnion([Q0]), "operationType" : NewBodyOperationType.ADD, "depth" : 25.4 * mm, "hasSecondDirection" : true, "secondDirectionOppositeDirection" : true, "secondDirectionDepth" : 254 * mm});
        }
        {
            var Q0;
            Q0=makeQuery(id+"F8.opExtrude","SWEPT_FACE",FACE,{"disambiguationData":[OSD([sQuery(id+"F6.wireOp",EDGE,"E3.2")])]});
            var sketch = newSketch(context, id + "F155", { "sketchPlane" : qUnion([Q0])});
            skLineSegment(sketch, "E253", {"start": v(-73.72, 2135.2) * mm, "end": v(5892.8, 8718.53) * mm});
            skLineSegment(sketch, "E254", {"start": v(5892.8, 8718.53) * mm, "end": v(11859.32, 2135.2) * mm});
            skSolve(sketch);
        }
        {
            var Q0;
            {var subQ4=sQuery(id+"F155.wireOp",EDGE,"E253");Q0=makeQuery(id+"F155.imprint","IMPRINT",FACE,{"disambiguationData":[TD([[makeQuery(id+"F155.imprint","IMPRINT",EDGE,{"derivedFrom":subQ4}),1.0]])]});}
            extrude(context, id + "F156", {"entities" : qUnion([Q0]), "operationType" : NewBodyOperationType.ADD, "depth" : 12.7 * mm, "hasDraft" : true, "draftAngle" : 15 * degree});
        }
        {
            var Q0;
            Q0=makeQuery(id+"F8.opExtrude","SWEPT_FACE",FACE,{"disambiguationData":[OSD([sQuery(id+"F6.wireOp",EDGE,"E3.3")])]});
            var sketch = newSketch(context, id + "F157", { "sketchPlane" : qUnion([Q0])});
            skLineSegment(sketch, "E255", {"start": v(2135.2, 11859.32) * mm, "end": v(8721.85, 5889.8) * mm});
            skLineSegment(sketch, "E256", {"start": v(8721.85, 5889.8) * mm, "end": v(2135.2, -79.73) * mm});
            skSolve(sketch);
        }
        {
            var Q0;
            {var subQ5=sQuery(id+"F157.wireOp",EDGE,"E255");Q0=makeQuery(id+"F157.imprint","IMPRINT",FACE,{"disambiguationData":[TD([[makeQuery(id+"F157.imprint","IMPRINT",EDGE,{"derivedFrom":subQ5}),1.0]])]});}
            extrude(context, id + "F158", {"entities" : qUnion([Q0]), "operationType" : NewBodyOperationType.ADD, "depth" : 12.7 * mm, "hasDraft" : true, "draftAngle" : 15 * degree});
        }
        {
            var Q0;
            Q0=makeQuery(id+"F8.opExtrude","SWEPT_FACE",FACE,{"disambiguationData":[OSD([sQuery(id+"F6.wireOp",EDGE,"E3.0")])]});
            var sketch = newSketch(context, id + "F159", { "sketchPlane" : qUnion([Q0])});
            skLineSegment(sketch, "E257", {"start": v(-73.72, 8546.18) * mm, "end": v(5892.8, 1962.85) * mm});
            skLineSegment(sketch, "E258", {"start": v(5892.8, 1962.85) * mm, "end": v(11859.32, 8546.18) * mm});
            skSolve(sketch);
        }
        {
            var Q0;
            {var subQ5=sQuery(id+"F159.wireOp",EDGE,"E257");Q0=makeQuery(id+"F159.imprint","IMPRINT",FACE,{"disambiguationData":[TD([[makeQuery(id+"F159.imprint","IMPRINT",EDGE,{"derivedFrom":subQ5}),-1.0]])]});}
            extrude(context, id + "F160", {"entities" : qUnion([Q0]), "operationType" : NewBodyOperationType.ADD, "depth" : 12.7 * mm, "hasDraft" : true, "draftAngle" : 15 * degree});
        }
        {
            var Q0;
            Q0=makeQuery(id+"F8.opExtrude","SWEPT_FACE",FACE,{"disambiguationData":[OSD([sQuery(id+"F6.wireOp",EDGE,"E3.1")])]});
            var sketch = newSketch(context, id + "F161", { "sketchPlane" : qUnion([Q0])});
            skLineSegment(sketch, "E259", {"start": v(8546.18, 11865.33) * mm, "end": v(1956.22, 5892.8) * mm});
            skLineSegment(sketch, "E260", {"start": v(1956.22, 5892.8) * mm, "end": v(8546.18, -79.73) * mm});
            skSolve(sketch);
        }
        {
            var Q0;
            {var subQ6=sQuery(id+"F161.wireOp",EDGE,"E259");Q0=makeQuery(id+"F161.imprint","IMPRINT",FACE,{"disambiguationData":[TD([[makeQuery(id+"F161.imprint","IMPRINT",EDGE,{"derivedFrom":subQ6}),-1.0]])]});}
            extrude(context, id + "F162", {"entities" : qUnion([Q0]), "operationType" : NewBodyOperationType.ADD, "depth" : 12.7 * mm, "hasDraft" : true, "draftAngle" : 15 * degree});
        }
        {
            var Q0;
            Q0=makeQuery(id+"F77.opExtrude","SWEPT_FACE",FACE,{"disambiguationData":[OSD([sQuery(id+"F76.wireOp",EDGE,"E127.right")])]});
            var sketch = newSketch(context, id + "F163", { "sketchPlane" : qUnion([Q0])});
            skLineSegment(sketch, "E261.bottom", {"start": v(-4577, -1778) * mm, "end": v(-990.6, -1778) * mm});
            skLineSegment(sketch, "E261.top", {"start": v(-4577, 0) * mm, "end": v(-990.6, 0) * mm});
            skLineSegment(sketch, "E261.left", {"start": v(-4577, -1778) * mm, "end": v(-4577, 0) * mm});
            skLineSegment(sketch, "E261.right", {"start": v(-990.6, -1778) * mm, "end": v(-990.6, 0) * mm});
            skLineSegment(sketch, "E262.bottom", {"start": v(-5186.6, 0) * mm, "end": v(-9070.76, 0) * mm});
            skLineSegment(sketch, "E262.top", {"start": v(-5186.6, -1778) * mm, "end": v(-9070.76, -1778) * mm});
            skLineSegment(sketch, "E262.left", {"start": v(-5186.6, 0) * mm, "end": v(-5186.6, -1778) * mm});
            skLineSegment(sketch, "E262.right", {"start": v(-9070.76, 0) * mm, "end": v(-9070.76, -1778) * mm});
            skSolve(sketch);
        }
        {
            var Q0;
            Q0 = qSketchRegion(id + "F163", true);
            extrude(context, id + "F164", {"entities" : qUnion([Q0]), "operationType" : NewBodyOperationType.REMOVE, "oppositeDirection" : true, "depth" : 609.6 * mm});
        }
        {
            var Q0;
            {var subQ0=sQuery(id+"F76.wireOp",EDGE,"E127.right");var subQ2=sQuery(id+"F76.wireOp",EDGE,"E127.top");Q0=makeQuery(id+"F164.boolean.opBoolean","SPLIT",FACE,{"disambiguationData":[TD([makeQuery(id+"F77.opExtrude","SWEPT_FACE",FACE,{"disambiguationData":[OSD([subQ2])]})])],"derivedFrom":makeQuery(id+"F77.opExtrude","SWEPT_FACE",FACE,{"disambiguationData":[OSD([subQ0])]})});}
            var sketch = newSketch(context, id + "F165", { "sketchPlane" : qUnion([Q0])});
            skLineSegment(sketch, "E263.bottom", {"start": v(-990.6, -1778) * mm, "end": v(-340.5, -1778) * mm});
            skLineSegment(sketch, "E263.top", {"start": v(-990.6, 0) * mm, "end": v(-340.5, 0) * mm});
            skLineSegment(sketch, "E263.left", {"start": v(-990.6, -1778) * mm, "end": v(-990.6, 0) * mm});
            skLineSegment(sketch, "E263.right", {"start": v(-340.5, -1778) * mm, "end": v(-340.5, 0) * mm});
            skSolve(sketch);
        }
        {
            var Q0;
            Q0=makeQuery(id+"F165.imprint","IMPRINT",FACE,{"disambiguationData":[TD([[makeQuery(id+"F165.imprint","IMPRINT",EDGE,{"derivedFrom":sQuery(id+"F165.wireOp",EDGE,"E263.bottom")}),1.0]])]});
            extrude(context, id + "F166", {"entities" : qUnion([Q0]), "operationType" : NewBodyOperationType.REMOVE, "oppositeDirection" : true, "depth" : 25.4 * mm});
        }
        {
            var Q0;
            {var subQ0=sQuery(id+"F76.wireOp",EDGE,"E127.right");Q0=makeQuery(id+"F164.boolean.opBoolean","SPLIT",FACE,{"disambiguationData":[TD([makeQuery(id+"F164.opExtrude","SWEPT_FACE",FACE,{"disambiguationData":[OSD([sQuery(id+"F163.wireOp",EDGE,"E261.left")])]})])],"derivedFrom":makeQuery(id+"F77.opExtrude","SWEPT_FACE",FACE,{"disambiguationData":[OSD([subQ0])]})});}
            var Q1;
            Q1=makeQuery(id+"F166.boolean.opBoolean","COPY",FACE,{"derivedFrom":makeQuery(id+"F166.opExtrude","CAP_FACE",FACE,{"disambiguationData":[OSD([sQuery(id+"F165.wireOp",EDGE,"E263.bottom"),sQuery(id+"F165.wireOp",EDGE,"E263.top"),sQuery(id+"F165.wireOp",EDGE,"E263.left"),sQuery(id+"F165.wireOp",EDGE,"E263.right")])],"isStart":false})});
            extrude(context, id + "F167", {"entities" : qUnion([Q0, Q1]), "operationType" : NewBodyOperationType.ADD, "oppositeDirection" : true, "depth" : 609.6 * mm});
        }
        {
            var Q0;
            Q0=makeQuery(id+"F38.boolean.opBoolean","COPY",FACE,{"derivedFrom":makeQuery(id+"F38.opExtrude","CAP_FACE",FACE,{"disambiguationData":[OSD([sQuery(id+"F35.wireOp",EDGE,"E54.0.0"),sQuery(id+"F35.wireOp",EDGE,"E54.0.1"),sQuery(id+"F35.wireOp",EDGE,"E54.0.2"),sQuery(id+"F35.wireOp",EDGE,"E54.0.3"),sQuery(id+"F35.wireOp",EDGE,"E54.0.4"),sQuery(id+"F35.wireOp",EDGE,"E54.0.5"),sQuery(id+"F35.wireOp",EDGE,"E54.0.6"),sQuery(id+"F35.wireOp",EDGE,"E54.0.7"),sQuery(id+"F35.wireOp",EDGE,"E55.bottom"),sQuery(id+"F35.wireOp",EDGE,"E55.top"),sQuery(id+"F35.wireOp",EDGE,"E55.left"),sQuery(id+"F35.wireOp",EDGE,"E55.right"),sQuery(id+"F35.wireOp",EDGE,"E56.bottom"),sQuery(id+"F35.wireOp",EDGE,"E56.top"),sQuery(id+"F35.wireOp",EDGE,"E56.left"),sQuery(id+"F35.wireOp",EDGE,"E56.right")])],"isStart":false})});
            cPlane(context, id + "F168", {"entities" : qUnion([Q0]), "cplaneType" : CPlaneType.OFFSET, "offset" : 50.8 * mm, "width" : 152.4 * mm, "height" : 152.4 * mm});
        }
        {
            var Q0;
            Q0=qCreatedBy(id+"F168.planeOp",FACE);
            var sketch = newSketch(context, id + "F169", { "sketchPlane" : qUnion([Q0])});
            skLineSegment(sketch, "E264.bottom", {"start": v(-18923, 50.8) * mm, "end": v(-11734.8, 50.8) * mm});
            skLineSegment(sketch, "E264.top", {"start": v(-18923, -203.2) * mm, "end": v(-11734.8, -203.2) * mm});
            skLineSegment(sketch, "E264.left", {"start": v(-18923, 50.8) * mm, "end": v(-18923, -203.2) * mm});
            skLineSegment(sketch, "E264.right", {"start": v(-11734.8, 50.8) * mm, "end": v(-11734.8, -203.2) * mm});
            skSolve(sketch);
        }
        {
            var Q0;
            Q0 = qSketchRegion(id + "F169", true);
            extrude(context, id + "F170", {"entities" : qUnion([Q0]), "depth" : 5080 * mm});
        }
        {
            var Q0;
            Q0=makeQuery(id+"F170.opExtrude","SWEPT_FACE",FACE,{"disambiguationData":[OSD([sQuery(id+"F169.wireOp",EDGE,"E264.bottom")])]});
            var sketch = newSketch(context, id + "F171", { "sketchPlane" : qUnion([Q0])});
            skLineSegment(sketch, "E265.0", {"start": v(11709.4, 8813.8) * mm, "end": v(18948.4, 8813.8) * mm});
            skLineSegment(sketch, "E265.1", {"start": v(11709.4, 13944.6) * mm, "end": v(11709.4, 8813.8) * mm});
            skLineSegment(sketch, "E265.2", {"start": v(18948.4, 13944.6) * mm, "end": v(11709.4, 13944.6) * mm});
            skLineSegment(sketch, "E265.3", {"start": v(18948.4, 8813.8) * mm, "end": v(18948.4, 13944.6) * mm});
            skSolve(sketch);
        }
        {
            var Q0;
            Q0 = qSketchRegion(id + "F171", true);
            extrude(context, id + "F172", {"entities" : qUnion([Q0]), "operationType" : NewBodyOperationType.ADD, "depth" : 25.4 * mm});
        }
        {
            var Q0;
            Q0=makeQuery(id+"F172.opExtrude","CAP_FACE",FACE,{"disambiguationData":[OSD([sQuery(id+"F171.wireOp",EDGE,"E265.0"),sQuery(id+"F171.wireOp",EDGE,"E265.1"),sQuery(id+"F171.wireOp",EDGE,"E265.2"),sQuery(id+"F171.wireOp",EDGE,"E265.3")])],"isStart":false});
            var sketch = newSketch(context, id + "F173", { "sketchPlane" : qUnion([Q0])});
            skLineSegment(sketch, "E266.bottom", {"start": v(18770.6, 9982.2) * mm, "end": v(18872.2, 9982.2) * mm});
            skLineSegment(sketch, "E266.top", {"start": v(18770.6, 9880.6) * mm, "end": v(18872.2, 9880.6) * mm});
            skLineSegment(sketch, "E266.left", {"start": v(18770.6, 9982.2) * mm, "end": v(18770.6, 9880.6) * mm});
            skLineSegment(sketch, "E266.right", {"start": v(18872.2, 9982.2) * mm, "end": v(18872.2, 9880.6) * mm});
            skLineSegment(sketch, "E267.bottom", {"start": v(18770.6, 11925.3) * mm, "end": v(18872.2, 11925.3) * mm});
            skLineSegment(sketch, "E267.top", {"start": v(18770.6, 11823.7) * mm, "end": v(18872.2, 11823.7) * mm});
            skLineSegment(sketch, "E267.left", {"start": v(18770.6, 11925.3) * mm, "end": v(18770.6, 11823.7) * mm});
            skLineSegment(sketch, "E267.right", {"start": v(18872.2, 11925.3) * mm, "end": v(18872.2, 11823.7) * mm});
            skLineSegment(sketch, "E268.bottom", {"start": v(18770.6, 13868.4) * mm, "end": v(18872.2, 13868.4) * mm});
            skLineSegment(sketch, "E268.top", {"start": v(18770.6, 13766.8) * mm, "end": v(18872.2, 13766.8) * mm});
            skLineSegment(sketch, "E268.left", {"start": v(18770.6, 13868.4) * mm, "end": v(18770.6, 13766.8) * mm});
            skLineSegment(sketch, "E268.right", {"start": v(18872.2, 13868.4) * mm, "end": v(18872.2, 13766.8) * mm});
            skLineSegment(sketch, "E269.bottom", {"start": v(16442.27, 13868.4) * mm, "end": v(16543.87, 13868.4) * mm});
            skLineSegment(sketch, "E269.top", {"start": v(16442.27, 13766.8) * mm, "end": v(16543.87, 13766.8) * mm});
            skLineSegment(sketch, "E269.left", {"start": v(16442.27, 13868.4) * mm, "end": v(16442.27, 13766.8) * mm});
            skLineSegment(sketch, "E269.right", {"start": v(16543.87, 13868.4) * mm, "end": v(16543.87, 13766.8) * mm});
            skLineSegment(sketch, "E270.bottom", {"start": v(14113.93, 13868.4) * mm, "end": v(14215.53, 13868.4) * mm});
            skLineSegment(sketch, "E270.top", {"start": v(14113.93, 13766.8) * mm, "end": v(14215.53, 13766.8) * mm});
            skLineSegment(sketch, "E270.left", {"start": v(14113.93, 13868.4) * mm, "end": v(14113.93, 13766.8) * mm});
            skLineSegment(sketch, "E270.right", {"start": v(14215.53, 13868.4) * mm, "end": v(14215.53, 13766.8) * mm});
            skLineSegment(sketch, "E271.bottom", {"start": v(11785.6, 13868.4) * mm, "end": v(11887.2, 13868.4) * mm});
            skLineSegment(sketch, "E271.top", {"start": v(11785.6, 13766.8) * mm, "end": v(11887.2, 13766.8) * mm});
            skLineSegment(sketch, "E271.left", {"start": v(11785.6, 13868.4) * mm, "end": v(11785.6, 13766.8) * mm});
            skLineSegment(sketch, "E271.right", {"start": v(11887.2, 13868.4) * mm, "end": v(11887.2, 13766.8) * mm});
            skLineSegment(sketch, "E272.bottom", {"start": v(11785.6, 11735.59) * mm, "end": v(11887.2, 11735.59) * mm});
            skLineSegment(sketch, "E272.top", {"start": v(11785.6, 11633.99) * mm, "end": v(11887.2, 11633.99) * mm});
            skLineSegment(sketch, "E272.left", {"start": v(11785.6, 11735.59) * mm, "end": v(11785.6, 11633.99) * mm});
            skLineSegment(sketch, "E272.right", {"start": v(11887.2, 11735.59) * mm, "end": v(11887.2, 11633.99) * mm});
            skLineSegment(sketch, "E273", {"start": v(11887.2, 13868.4) * mm, "end": v(14113.93, 13868.4) * mm, "construction": true});
            skLineSegment(sketch, "E274", {"start": v(14215.53, 13868.4) * mm, "end": v(16442.27, 13868.4) * mm, "construction": true});
            skLineSegment(sketch, "E275", {"start": v(16543.87, 13868.4) * mm, "end": v(18770.6, 13868.4) * mm, "construction": true});
            skLineSegment(sketch, "E276", {"start": v(18872.2, 13766.8) * mm, "end": v(18872.2, 11925.3) * mm, "construction": true});
            skLineSegment(sketch, "E277", {"start": v(18872.2, 11823.7) * mm, "end": v(18872.2, 9982.2) * mm, "construction": true});
            skLineSegment(sketch, "E278", {"start": v(11785.6, 13766.8) * mm, "end": v(11785.6, 11735.59) * mm, "construction": true});
            skSolve(sketch);
        }
        {
            var Q0;
            Q0 = qSketchRegion(id + "F173", true);
            extrude(context, id + "F174", {"entities" : qUnion([Q0]), "operationType" : NewBodyOperationType.ADD, "depth" : 863.6 * mm, "hasSecondDirection" : true, "secondDirectionOppositeDirection" : true, "secondDirectionDepth" : 2032 * mm});
        }
        {
            var Q0;
            Q0=makeQuery(id+"F174.opExtrude","CAP_FACE",FACE,{"disambiguationData":[OSD([sQuery(id+"F173.wireOp",EDGE,"E266.bottom"),sQuery(id+"F173.wireOp",EDGE,"E266.top"),sQuery(id+"F173.wireOp",EDGE,"E266.left"),sQuery(id+"F173.wireOp",EDGE,"E266.right")])],"isStart":false});
            var sketch = newSketch(context, id + "F175", { "sketchPlane" : qUnion([Q0])});
            skLineSegment(sketch, "E279", {"start": v(18757.9, 9867.9) * mm, "end": v(18884.9, 9867.9) * mm});
            skLineSegment(sketch, "E280", {"start": v(18884.9, 9867.9) * mm, "end": v(18884.9, 13881.1) * mm});
            skLineSegment(sketch, "E281", {"start": v(18884.9, 13881.1) * mm, "end": v(11772.9, 13881.1) * mm});
            skLineSegment(sketch, "E282", {"start": v(11772.9, 13881.1) * mm, "end": v(11772.9, 11621.29) * mm});
            skLineSegment(sketch, "E283", {"start": v(11772.9, 11621.29) * mm, "end": v(11899.9, 11621.29) * mm});
            skLineSegment(sketch, "E284", {"start": v(11899.9, 11621.29) * mm, "end": v(11899.9, 13754.1) * mm});
            skLineSegment(sketch, "E285", {"start": v(11899.9, 13754.1) * mm, "end": v(18757.9, 13754.1) * mm});
            skLineSegment(sketch, "E286", {"start": v(18757.9, 13754.1) * mm, "end": v(18757.9, 9867.9) * mm});
            skSolve(sketch);
        }
        {
            var Q0;
            Q0 = qSketchRegion(id + "F175", true);
            extrude(context, id + "F176", {"entities" : qUnion([Q0]), "operationType" : NewBodyOperationType.ADD, "depth" : 38.1 * mm});
        }
        {
            var Q0;
            Q0=makeQuery(id+"F176.opExtrude","CAP_FACE",FACE,{"disambiguationData":[OSD([sQuery(id+"F175.wireOp",EDGE,"E279"),sQuery(id+"F175.wireOp",EDGE,"E280"),sQuery(id+"F175.wireOp",EDGE,"E281"),sQuery(id+"F175.wireOp",EDGE,"E282"),sQuery(id+"F175.wireOp",EDGE,"E283"),sQuery(id+"F175.wireOp",EDGE,"E284"),sQuery(id+"F175.wireOp",EDGE,"E285"),sQuery(id+"F175.wireOp",EDGE,"E286")])],"isStart":false});
            var sketch = newSketch(context, id + "F177", { "sketchPlane" : qUnion([Q0])});
            skLineSegment(sketch, "E287.0", {"start": v(11925.3, 11595.89) * mm, "end": v(11925.3, 13728.7) * mm});
            skLineSegment(sketch, "E287.1", {"start": v(11747.5, 11595.89) * mm, "end": v(11925.3, 11595.89) * mm});
            skLineSegment(sketch, "E287.2", {"start": v(11925.3, 13728.7) * mm, "end": v(18732.5, 13728.7) * mm});
            skLineSegment(sketch, "E287.3", {"start": v(11747.5, 13906.5) * mm, "end": v(11747.5, 11595.89) * mm});
            skLineSegment(sketch, "E287.4", {"start": v(18732.5, 13728.7) * mm, "end": v(18732.5, 9842.5) * mm});
            skLineSegment(sketch, "E287.5", {"start": v(18732.5, 9842.5) * mm, "end": v(18910.3, 9842.5) * mm});
            skLineSegment(sketch, "E287.6", {"start": v(18910.3, 9842.5) * mm, "end": v(18910.3, 13906.5) * mm});
            skLineSegment(sketch, "E287.7", {"start": v(18910.3, 13906.5) * mm, "end": v(11747.5, 13906.5) * mm});
            skSolve(sketch);
        }
        {
            var Q0;
            Q0 = qSketchRegion(id + "F177", true);
            extrude(context, id + "F178", {"entities" : qUnion([Q0]), "operationType" : NewBodyOperationType.ADD, "depth" : 25.4 * mm});
        }
        {
            var Q0;
            Q0=makeQuery(id+"F170.opExtrude","SWEPT_FACE",FACE,{"disambiguationData":[OSD([sQuery(id+"F169.wireOp",EDGE,"E264.top")])]});
            var sketch = newSketch(context, id + "F179", { "sketchPlane" : qUnion([Q0])});
            skLineSegment(sketch, "E288.0", {"start": v(18821.4, -8940.8) * mm, "end": v(11836.4, -8940.8) * mm});
            skLineSegment(sketch, "E288.1", {"start": v(18821.4, -13817.6) * mm, "end": v(18821.4, -8940.8) * mm});
            skLineSegment(sketch, "E288.2", {"start": v(11836.4, -13817.6) * mm, "end": v(18821.4, -13817.6) * mm});
            skLineSegment(sketch, "E288.3", {"start": v(11836.4, -8940.8) * mm, "end": v(11836.4, -13817.6) * mm});
            skSolve(sketch);
        }
        {
            var Q0;
            Q0 = qSketchRegion(id + "F179", true);
            extrude(context, id + "F180", {"entities" : qUnion([Q0]), "operationType" : NewBodyOperationType.ADD, "depth" : 1371.6 * mm});
        }
        {
            var Q0;
            Q0=makeQuery(id+"F170.opExtrude","SWEPT_FACE",FACE,{"disambiguationData":[OSD([sQuery(id+"F169.wireOp",EDGE,"E264.left")])]});
            var sketch = newSketch(context, id + "F181", { "sketchPlane" : qUnion([Q0])});
            skLineSegment(sketch, "E289.bottom", {"start": v(8839.2, -127) * mm, "end": v(9906, -127) * mm});
            skLineSegment(sketch, "E289.top", {"start": v(8839.2, -330.2) * mm, "end": v(9906, -330.2) * mm});
            skLineSegment(sketch, "E289.left", {"start": v(8839.2, -127) * mm, "end": v(8839.2, -330.2) * mm});
            skLineSegment(sketch, "E289.right", {"start": v(9906, -127) * mm, "end": v(9906, -330.2) * mm});
            skSolve(sketch);
        }
        {
            var Q0;
            Q0 = qSketchRegion(id + "F181", true);
            extrude(context, id + "F182", {"entities" : qUnion([Q0]), "operationType" : NewBodyOperationType.ADD, "depth" : 254 * mm});
        }
        {
            var Q0;
            Q0=makeQuery(id+"F182.opExtrude","SWEPT_FACE",FACE,{"disambiguationData":[OSD([sQuery(id+"F181.wireOp",EDGE,"E289.bottom")])]});
            var sketch = newSketch(context, id + "F183", { "sketchPlane" : qUnion([Q0])});
            skLineSegment(sketch, "E290.0", {"start": v(18897.6, 9931.4) * mm, "end": v(18897.6, 8813.8) * mm});
            skLineSegment(sketch, "E290.1", {"start": v(19202.4, 9931.4) * mm, "end": v(18897.6, 9931.4) * mm});
            skLineSegment(sketch, "E290.2", {"start": v(19202.4, 8813.8) * mm, "end": v(19202.4, 9931.4) * mm});
            skLineSegment(sketch, "E290.3", {"start": v(18897.6, 8813.8) * mm, "end": v(19202.4, 8813.8) * mm});
            skSolve(sketch);
        }
        {
            var Q0;
            Q0 = qSketchRegion(id + "F183", true);
            extrude(context, id + "F184", {"entities" : qUnion([Q0]), "operationType" : NewBodyOperationType.ADD, "oppositeDirection" : true, "depth" : 25.4 * mm});
        }
        {
            var Q0;
            Q0=makeQuery(id+"F182.opExtrude","SWEPT_FACE",FACE,{"disambiguationData":[OSD([sQuery(id+"F181.wireOp",EDGE,"E289.top")])]});
            var sketch = newSketch(context, id + "F185", { "sketchPlane" : qUnion([Q0])});
            skLineSegment(sketch, "E291.bottom", {"start": v(18923, -8839.2) * mm, "end": v(19431, -8839.2) * mm});
            skLineSegment(sketch, "E291.top", {"start": v(18923, -10160) * mm, "end": v(19431, -10160) * mm});
            skLineSegment(sketch, "E291.left", {"start": v(18923, -8839.2) * mm, "end": v(18923, -10160) * mm});
            skLineSegment(sketch, "E291.right", {"start": v(19431, -8839.2) * mm, "end": v(19431, -10160) * mm});
            skSolve(sketch);
        }
        {
            var Q0;
            Q0 = qSketchRegion(id + "F185", true);
            extrude(context, id + "F186", {"entities" : qUnion([Q0]), "operationType" : NewBodyOperationType.ADD, "depth" : 203.2 * mm});
        }
        {
            var Q0;
            Q0=makeQuery(id+"F186.opExtrude","CAP_FACE",FACE,{"disambiguationData":[OSD([sQuery(id+"F185.wireOp",EDGE,"E291.bottom"),sQuery(id+"F185.wireOp",EDGE,"E291.top"),sQuery(id+"F185.wireOp",EDGE,"E291.left"),sQuery(id+"F185.wireOp",EDGE,"E291.right")])],"isStart":true});
            var sketch = newSketch(context, id + "F187", { "sketchPlane" : qUnion([Q0])});
            skLineSegment(sketch, "E292.0", {"start": v(18897.6, 10185.4) * mm, "end": v(18897.6, 9880.6) * mm});
            skLineSegment(sketch, "E292.1", {"start": v(19151.6, 9880.6) * mm, "end": v(19151.6, 8813.8) * mm});
            skLineSegment(sketch, "E292.2", {"start": v(19151.6, 8813.8) * mm, "end": v(19456.4, 8813.8) * mm});
            skLineSegment(sketch, "E292.3", {"start": v(18897.6, 9880.6) * mm, "end": v(19151.6, 9880.6) * mm});
            skLineSegment(sketch, "E292.4", {"start": v(19456.4, 8813.8) * mm, "end": v(19456.4, 10185.4) * mm});
            skLineSegment(sketch, "E292.5", {"start": v(19456.4, 10185.4) * mm, "end": v(18897.6, 10185.4) * mm});
            skSolve(sketch);
        }
        {
            var Q0;
            Q0 = qSketchRegion(id + "F187", true);
            extrude(context, id + "F188", {"entities" : qUnion([Q0]), "operationType" : NewBodyOperationType.ADD, "oppositeDirection" : true, "depth" : 25.4 * mm});
        }
        {
            var Q0;
            Q0=makeQuery(id+"F186.opExtrude","CAP_FACE",FACE,{"disambiguationData":[OSD([sQuery(id+"F185.wireOp",EDGE,"E291.bottom"),sQuery(id+"F185.wireOp",EDGE,"E291.top"),sQuery(id+"F185.wireOp",EDGE,"E291.left"),sQuery(id+"F185.wireOp",EDGE,"E291.right")])],"isStart":false});
            var sketch = newSketch(context, id + "F189", { "sketchPlane" : qUnion([Q0])});
            skLineSegment(sketch, "E293.bottom", {"start": v(18923, -8839.2) * mm, "end": v(19685, -8839.2) * mm});
            skLineSegment(sketch, "E293.top", {"start": v(18923, -10414) * mm, "end": v(19685, -10414) * mm});
            skLineSegment(sketch, "E293.left", {"start": v(18923, -8839.2) * mm, "end": v(18923, -10414) * mm});
            skLineSegment(sketch, "E293.right", {"start": v(19685, -8839.2) * mm, "end": v(19685, -10414) * mm});
            skSolve(sketch);
        }
        {
            var Q0;
            Q0 = qSketchRegion(id + "F189", true);
            extrude(context, id + "F190", {"entities" : qUnion([Q0]), "operationType" : NewBodyOperationType.ADD, "depth" : 203.2 * mm});
        }
        {
            var Q0;
            Q0=makeQuery(id+"F190.opExtrude","CAP_FACE",FACE,{"disambiguationData":[OSD([sQuery(id+"F189.wireOp",EDGE,"E293.bottom"),sQuery(id+"F189.wireOp",EDGE,"E293.top"),sQuery(id+"F189.wireOp",EDGE,"E293.left"),sQuery(id+"F189.wireOp",EDGE,"E293.right")])],"isStart":true});
            var sketch = newSketch(context, id + "F191", { "sketchPlane" : qUnion([Q0])});
            skLineSegment(sketch, "E294.0", {"start": v(19710.4, 10439.4) * mm, "end": v(18897.6, 10439.4) * mm});
            skLineSegment(sketch, "E294.1", {"start": v(18897.6, 10134.6) * mm, "end": v(19405.6, 10134.6) * mm});
            skLineSegment(sketch, "E294.2", {"start": v(19405.6, 10134.6) * mm, "end": v(19405.6, 8813.8) * mm});
            skLineSegment(sketch, "E294.3", {"start": v(18897.6, 10439.4) * mm, "end": v(18897.6, 10134.6) * mm});
            skLineSegment(sketch, "E294.4", {"start": v(19405.6, 8813.8) * mm, "end": v(19710.4, 8813.8) * mm});
            skLineSegment(sketch, "E294.5", {"start": v(19710.4, 8813.8) * mm, "end": v(19710.4, 10439.4) * mm});
            skSolve(sketch);
        }
        {
            var Q0;
            Q0 = qSketchRegion(id + "F191", true);
            extrude(context, id + "F192", {"entities" : qUnion([Q0]), "operationType" : NewBodyOperationType.ADD, "oppositeDirection" : true, "depth" : 25.4 * mm});
        }
        {
            var Q0;
            {var subQ1=sQuery(id+"F173.wireOp",EDGE,"E267.right");Q0=makeQuery(id+"F174.boolean.opBoolean","SPLIT",FACE,{"disambiguationData":[TD([makeQuery(id+"F170.opExtrude","SWEPT_FACE",FACE,{"disambiguationData":[OSD([sQuery(id+"F169.wireOp",EDGE,"E264.top")])]})])],"derivedFrom":makeQuery(id+"F174.opExtrude","SWEPT_FACE",FACE,{"disambiguationData":[OSD([subQ1])]})});}
            var sketch = newSketch(context, id + "F193", { "sketchPlane" : qUnion([Q0])});
            skLineSegment(sketch, "E295", {"start": v(9968.96, -571.16) * mm, "end": v(13868.4, -1016) * mm});
            skLineSegment(sketch, "E296", {"start": v(13868.4, -1016) * mm, "end": v(13868.4, -1118.26) * mm});
            skLineSegment(sketch, "E297", {"start": v(13868.4, -1118.26) * mm, "end": v(9959.61, -672.36) * mm});
            skLineSegment(sketch, "E298", {"start": v(9959.61, -672.36) * mm, "end": v(9968.96, -571.16) * mm});
            skSolve(sketch);
        }
        {
            var Q0;
            Q0 = qSketchRegion(id + "F193", true);
            extrude(context, id + "F194", {"entities" : qUnion([Q0]), "operationType" : NewBodyOperationType.ADD, "depth" : 25.4 * mm, "hasSecondDirection" : true, "secondDirectionOppositeDirection" : true, "secondDirectionDepth" : 25.4 * mm});
        }
        {
            var Q0;
            {var subQ2=sQuery(id+"F173.wireOp",EDGE,"E268.bottom");Q0=makeQuery(id+"F194.boolean.opBoolean","MERGE",FACE,{"derivedFrom":[makeQuery(id+"F174.boolean.opBoolean","SPLIT",FACE,{"disambiguationData":[TD([makeQuery(id+"F170.opExtrude","SWEPT_FACE",FACE,{"disambiguationData":[OSD([sQuery(id+"F169.wireOp",EDGE,"E264.top")])]})])],"derivedFrom":makeQuery(id+"F174.opExtrude","SWEPT_FACE",FACE,{"disambiguationData":[OSD([subQ2])]})}),makeQuery(id+"F194.opExtrude","SWEPT_FACE",FACE,{"disambiguationData":[OSD([sQuery(id+"F193.wireOp",EDGE,"E296")])]})]});}
            var sketch = newSketch(context, id + "F195", { "sketchPlane" : qUnion([Q0])});
            skLineSegment(sketch, "E299.bottom", {"start": v(-18897.6, -1016) * mm, "end": v(-11785.6, -1016) * mm});
            skLineSegment(sketch, "E299.top", {"start": v(-18897.6, -1118.26) * mm, "end": v(-11785.6, -1118.26) * mm});
            skLineSegment(sketch, "E299.left", {"start": v(-18897.6, -1016) * mm, "end": v(-18897.6, -1118.26) * mm});
            skLineSegment(sketch, "E299.right", {"start": v(-11785.6, -1016) * mm, "end": v(-11785.6, -1118.26) * mm});
            skSolve(sketch);
        }
        {
            var Q0;
            Q0 = qSketchRegion(id + "F195", true);
            extrude(context, id + "F196", {"entities" : qUnion([Q0]), "operationType" : NewBodyOperationType.ADD, "depth" : 25.4 * mm, "hasSecondDirection" : true, "secondDirectionOppositeDirection" : true, "secondDirectionDepth" : 25.4 * mm});
        }
        {
            var Q0;
            {var subQ0=sQuery(id+"F173.wireOp",EDGE,"E271.left");Q0=makeQuery(id+"F196.boolean.opBoolean","MERGE",FACE,{"derivedFrom":[makeQuery(id+"F174.boolean.opBoolean","SPLIT",FACE,{"disambiguationData":[TD([makeQuery(id+"F170.opExtrude","SWEPT_FACE",FACE,{"disambiguationData":[OSD([sQuery(id+"F169.wireOp",EDGE,"E264.top")])]})])],"derivedFrom":makeQuery(id+"F174.opExtrude","SWEPT_FACE",FACE,{"disambiguationData":[OSD([subQ0])]})}),makeQuery(id+"F196.opExtrude","SWEPT_FACE",FACE,{"disambiguationData":[OSD([sQuery(id+"F195.wireOp",EDGE,"E299.right")])]})]});}
            var sketch = newSketch(context, id + "F197", { "sketchPlane" : qUnion([Q0])});
            skLineSegment(sketch, "E300.bottom", {"start": v(-13893.8, -1016) * mm, "end": v(-11593.4, -1016) * mm});
            skLineSegment(sketch, "E300.top", {"start": v(-13893.8, -1118.26) * mm, "end": v(-11593.4, -1118.26) * mm});
            skLineSegment(sketch, "E300.left", {"start": v(-13893.8, -1016) * mm, "end": v(-13893.8, -1118.26) * mm});
            skLineSegment(sketch, "E300.right", {"start": v(-11593.4, -1016) * mm, "end": v(-11593.4, -1118.26) * mm});
            skSolve(sketch);
        }
        {
            var Q0;
            Q0 = qSketchRegion(id + "F197", true);
            extrude(context, id + "F198", {"entities" : qUnion([Q0]), "operationType" : NewBodyOperationType.ADD, "depth" : 25.4 * mm, "hasSecondDirection" : true, "secondDirectionOppositeDirection" : true, "secondDirectionDepth" : 25.4 * mm});
        }
        {
            var Q0;
            {var subQ2=sQuery(id+"F173.wireOp",EDGE,"E266.bottom");Q0=makeQuery(id+"F174.boolean.opBoolean","SPLIT",FACE,{"disambiguationData":[TD([makeQuery(id+"F172.opExtrude","CAP_FACE",FACE,{"disambiguationData":[OSD([sQuery(id+"F171.wireOp",EDGE,"E265.0"),sQuery(id+"F171.wireOp",EDGE,"E265.1"),sQuery(id+"F171.wireOp",EDGE,"E265.2"),sQuery(id+"F171.wireOp",EDGE,"E265.3")])],"isStart":false})])],"derivedFrom":makeQuery(id+"F174.opExtrude","SWEPT_FACE",FACE,{"disambiguationData":[OSD([subQ2])]})});}
            var sketch = newSketch(context, id + "F199", { "sketchPlane" : qUnion([Q0])});
            skLineSegment(sketch, "E301.bottom", {"start": v(-18826.48, 731.52) * mm, "end": v(-18816.32, 731.52) * mm});
            skLineSegment(sketch, "E301.top", {"start": v(-18826.48, 721.36) * mm, "end": v(-18816.32, 721.36) * mm});
            skLineSegment(sketch, "E301.left", {"start": v(-18826.48, 731.52) * mm, "end": v(-18826.48, 721.36) * mm});
            skLineSegment(sketch, "E301.right", {"start": v(-18816.32, 731.52) * mm, "end": v(-18816.32, 721.36) * mm});
            skLineSegment(sketch, "E302.bottom", {"start": v(-18826.48, 294.64) * mm, "end": v(-18816.32, 294.64) * mm});
            skLineSegment(sketch, "E302.top", {"start": v(-18826.48, 284.48) * mm, "end": v(-18816.32, 284.48) * mm});
            skLineSegment(sketch, "E302.left", {"start": v(-18826.48, 294.64) * mm, "end": v(-18826.48, 284.48) * mm});
            skLineSegment(sketch, "E302.right", {"start": v(-18816.32, 294.64) * mm, "end": v(-18816.32, 284.48) * mm});
            skLineSegment(sketch, "E303.bottom", {"start": v(-18826.48, 513.08) * mm, "end": v(-18816.32, 513.08) * mm});
            skLineSegment(sketch, "E303.top", {"start": v(-18826.48, 502.92) * mm, "end": v(-18816.32, 502.92) * mm});
            skLineSegment(sketch, "E303.left", {"start": v(-18826.48, 513.08) * mm, "end": v(-18826.48, 502.92) * mm});
            skLineSegment(sketch, "E303.right", {"start": v(-18816.32, 513.08) * mm, "end": v(-18816.32, 502.92) * mm});
            skLineSegment(sketch, "E304", {"start": v(-18821.4, 76.2) * mm, "end": v(-18821.4, 284.48) * mm, "construction": true});
            skLineSegment(sketch, "E305", {"start": v(-18816.32, 294.64) * mm, "end": v(-18816.32, 502.92) * mm, "construction": true});
            skLineSegment(sketch, "E306", {"start": v(-18816.32, 513.08) * mm, "end": v(-18816.32, 721.36) * mm, "construction": true});
            skLineSegment(sketch, "E307", {"start": v(-18816.32, 731.52) * mm, "end": v(-18816.32, 939.8) * mm, "construction": true});
            skSolve(sketch);
        }
        {
            var Q0;
            Q0 = qSketchRegion(id + "F199", true);
            var Q1;
            {var subQ2=sQuery(id+"F173.wireOp",EDGE,"E268.top");Q1=makeQuery(id+"F174.boolean.opBoolean","SPLIT",FACE,{"disambiguationData":[TD([makeQuery(id+"F172.opExtrude","CAP_FACE",FACE,{"disambiguationData":[OSD([sQuery(id+"F171.wireOp",EDGE,"E265.0"),sQuery(id+"F171.wireOp",EDGE,"E265.1"),sQuery(id+"F171.wireOp",EDGE,"E265.2"),sQuery(id+"F171.wireOp",EDGE,"E265.3")])],"isStart":false})])],"derivedFrom":makeQuery(id+"F174.opExtrude","SWEPT_FACE",FACE,{"disambiguationData":[OSD([subQ2])]})});}
            extrude(context, id + "F200", {"entities" : qUnion([Q0]), "operationType" : NewBodyOperationType.ADD, "endBound" : BoundingType.UP_TO_SURFACE, "endBoundEntityFace" : qUnion([Q1]), "depth" : 25.4 * mm});
        }
        {
            var Q0;
            {var subQ1=sQuery(id+"F173.wireOp",EDGE,"E268.left");Q0=makeQuery(id+"F174.boolean.opBoolean","SPLIT",FACE,{"disambiguationData":[TD([makeQuery(id+"F172.opExtrude","CAP_FACE",FACE,{"disambiguationData":[OSD([sQuery(id+"F171.wireOp",EDGE,"E265.0"),sQuery(id+"F171.wireOp",EDGE,"E265.1"),sQuery(id+"F171.wireOp",EDGE,"E265.2"),sQuery(id+"F171.wireOp",EDGE,"E265.3")])],"isStart":false})])],"derivedFrom":makeQuery(id+"F174.opExtrude","SWEPT_FACE",FACE,{"disambiguationData":[OSD([subQ1])]})});}
            var sketch = newSketch(context, id + "F201", { "sketchPlane" : qUnion([Q0])});
            skLineSegment(sketch, "E308.bottom", {"start": v(-13822.68, 731.52) * mm, "end": v(-13812.52, 731.52) * mm});
            skLineSegment(sketch, "E308.top", {"start": v(-13822.68, 721.36) * mm, "end": v(-13812.52, 721.36) * mm});
            skLineSegment(sketch, "E308.left", {"start": v(-13822.68, 731.52) * mm, "end": v(-13822.68, 721.36) * mm});
            skLineSegment(sketch, "E308.right", {"start": v(-13812.52, 731.52) * mm, "end": v(-13812.52, 721.36) * mm});
            skLineSegment(sketch, "E309.bottom", {"start": v(-13822.68, 513.08) * mm, "end": v(-13812.52, 513.08) * mm});
            skLineSegment(sketch, "E309.top", {"start": v(-13822.68, 502.92) * mm, "end": v(-13812.52, 502.92) * mm});
            skLineSegment(sketch, "E309.left", {"start": v(-13822.68, 513.08) * mm, "end": v(-13822.68, 502.92) * mm});
            skLineSegment(sketch, "E309.right", {"start": v(-13812.52, 513.08) * mm, "end": v(-13812.52, 502.92) * mm});
            skLineSegment(sketch, "E310.bottom", {"start": v(-13822.68, 294.64) * mm, "end": v(-13812.52, 294.64) * mm});
            skLineSegment(sketch, "E310.top", {"start": v(-13822.68, 284.48) * mm, "end": v(-13812.52, 284.48) * mm});
            skLineSegment(sketch, "E310.left", {"start": v(-13822.68, 294.64) * mm, "end": v(-13822.68, 284.48) * mm});
            skLineSegment(sketch, "E310.right", {"start": v(-13812.52, 294.64) * mm, "end": v(-13812.52, 284.48) * mm});
            skLineSegment(sketch, "E311", {"start": v(-13817.6, 284.48) * mm, "end": v(-13817.6, 76.2) * mm, "construction": true});
            skSolve(sketch);
        }
        {
            var Q0;
            Q0 = qSketchRegion(id + "F201", true);
            var Q1;
            {var subQ2=sQuery(id+"F173.wireOp",EDGE,"E271.right");Q1=makeQuery(id+"F174.boolean.opBoolean","SPLIT",FACE,{"disambiguationData":[TD([makeQuery(id+"F172.opExtrude","CAP_FACE",FACE,{"disambiguationData":[OSD([sQuery(id+"F171.wireOp",EDGE,"E265.0"),sQuery(id+"F171.wireOp",EDGE,"E265.1"),sQuery(id+"F171.wireOp",EDGE,"E265.2"),sQuery(id+"F171.wireOp",EDGE,"E265.3")])],"isStart":false})])],"derivedFrom":makeQuery(id+"F174.opExtrude","SWEPT_FACE",FACE,{"disambiguationData":[OSD([subQ2])]})});}
            extrude(context, id + "F202", {"entities" : qUnion([Q0]), "operationType" : NewBodyOperationType.ADD, "endBound" : BoundingType.UP_TO_SURFACE, "endBoundEntityFace" : qUnion([Q1]), "depth" : 25.4 * mm});
        }
        {
            var Q0;
            {var subQ2=sQuery(id+"F173.wireOp",EDGE,"E272.bottom");Q0=makeQuery(id+"F174.boolean.opBoolean","SPLIT",FACE,{"disambiguationData":[TD([makeQuery(id+"F172.opExtrude","CAP_FACE",FACE,{"disambiguationData":[OSD([sQuery(id+"F171.wireOp",EDGE,"E265.0"),sQuery(id+"F171.wireOp",EDGE,"E265.1"),sQuery(id+"F171.wireOp",EDGE,"E265.2"),sQuery(id+"F171.wireOp",EDGE,"E265.3")])],"isStart":false})])],"derivedFrom":makeQuery(id+"F174.opExtrude","SWEPT_FACE",FACE,{"disambiguationData":[OSD([subQ2])]})});}
            var sketch = newSketch(context, id + "F203", { "sketchPlane" : qUnion([Q0])});
            skLineSegment(sketch, "E312.bottom", {"start": v(-11841.48, 731.52) * mm, "end": v(-11831.32, 731.52) * mm});
            skLineSegment(sketch, "E312.top", {"start": v(-11841.48, 721.36) * mm, "end": v(-11831.32, 721.36) * mm});
            skLineSegment(sketch, "E312.left", {"start": v(-11841.48, 731.52) * mm, "end": v(-11841.48, 721.36) * mm});
            skLineSegment(sketch, "E312.right", {"start": v(-11831.32, 731.52) * mm, "end": v(-11831.32, 721.36) * mm});
            skLineSegment(sketch, "E313.bottom", {"start": v(-11841.48, 513.08) * mm, "end": v(-11831.32, 513.08) * mm});
            skLineSegment(sketch, "E313.top", {"start": v(-11841.48, 502.92) * mm, "end": v(-11831.32, 502.92) * mm});
            skLineSegment(sketch, "E313.left", {"start": v(-11841.48, 513.08) * mm, "end": v(-11841.48, 502.92) * mm});
            skLineSegment(sketch, "E313.right", {"start": v(-11831.32, 513.08) * mm, "end": v(-11831.32, 502.92) * mm});
            skLineSegment(sketch, "E314.bottom", {"start": v(-11841.48, 294.64) * mm, "end": v(-11831.32, 294.64) * mm});
            skLineSegment(sketch, "E314.top", {"start": v(-11841.48, 284.48) * mm, "end": v(-11831.32, 284.48) * mm});
            skLineSegment(sketch, "E314.left", {"start": v(-11841.48, 294.64) * mm, "end": v(-11841.48, 284.48) * mm});
            skLineSegment(sketch, "E314.right", {"start": v(-11831.32, 294.64) * mm, "end": v(-11831.32, 284.48) * mm});
            skLineSegment(sketch, "E315", {"start": v(-11836.4, 284.48) * mm, "end": v(-11836.4, 76.2) * mm, "construction": true});
            skSolve(sketch);
        }
        {
            var Q0;
            Q0 = qSketchRegion(id + "F203", true);
            var Q1;
            {var subQ2=sQuery(id+"F173.wireOp",EDGE,"E271.top");Q1=makeQuery(id+"F174.boolean.opBoolean","SPLIT",FACE,{"disambiguationData":[TD([makeQuery(id+"F172.opExtrude","CAP_FACE",FACE,{"disambiguationData":[OSD([sQuery(id+"F171.wireOp",EDGE,"E265.0"),sQuery(id+"F171.wireOp",EDGE,"E265.1"),sQuery(id+"F171.wireOp",EDGE,"E265.2"),sQuery(id+"F171.wireOp",EDGE,"E265.3")])],"isStart":false})])],"derivedFrom":makeQuery(id+"F174.opExtrude","SWEPT_FACE",FACE,{"disambiguationData":[OSD([subQ2])]})});}
            extrude(context, id + "F204", {"entities" : qUnion([Q0]), "operationType" : NewBodyOperationType.ADD, "endBound" : BoundingType.UP_TO_SURFACE, "endBoundEntityFace" : qUnion([Q1]), "depth" : 25.4 * mm});
        }
        {
            var Q0;
            Q0=makeQuery(id+"F133.opExtrude","CAP_FACE",FACE,{"disambiguationData":[OSD([sQuery(id+"F132.wireOp",EDGE,"E239.bottom"),sQuery(id+"F132.wireOp",EDGE,"E239.top"),sQuery(id+"F132.wireOp",EDGE,"E239.left"),sQuery(id+"F132.wireOp",EDGE,"E239.right")])],"isStart":false});
            cPlane(context, id + "F205", {"entities" : qUnion([Q0]), "cplaneType" : CPlaneType.OFFSET, "offset" : 50.8 * mm, "width" : 152.4 * mm, "height" : 152.4 * mm});
        }
        {
            var Q0;
            Q0=qCreatedBy(id+"F205.planeOp",FACE);
            var sketch = newSketch(context, id + "F206", { "sketchPlane" : qUnion([Q0])});
            skLineSegment(sketch, "E316.bottom", {"start": v(-11687.94, 79.2) * mm, "end": v(-4669.66, 79.2) * mm});
            skLineSegment(sketch, "E316.top", {"start": v(-11687.94, -174.8) * mm, "end": v(-4669.66, -174.8) * mm});
            skLineSegment(sketch, "E316.left", {"start": v(-11687.94, 79.2) * mm, "end": v(-11687.94, -174.8) * mm});
            skLineSegment(sketch, "E316.right", {"start": v(-4669.66, 79.2) * mm, "end": v(-4669.66, -174.8) * mm});
            skSolve(sketch);
        }
        {
            var Q0;
            Q0 = qSketchRegion(id + "F206", true);
            extrude(context, id + "F207", {"entities" : qUnion([Q0]), "depth" : 2438.4 * mm});
        }
        {
            var Q0;
            Q0=makeQuery(id+"F207.opExtrude","CAP_FACE",FACE,{"disambiguationData":[OSD([sQuery(id+"F206.wireOp",EDGE,"E316.bottom"),sQuery(id+"F206.wireOp",EDGE,"E316.top"),sQuery(id+"F206.wireOp",EDGE,"E316.left"),sQuery(id+"F206.wireOp",EDGE,"E316.right")])],"isStart":false});
            var sketch = newSketch(context, id + "F208", { "sketchPlane" : qUnion([Q0])});
            skLineSegment(sketch, "E317.bottom", {"start": v(-11687.94, 79.2) * mm, "end": v(-7386.44, 79.2) * mm});
            skLineSegment(sketch, "E317.top", {"start": v(-11687.94, -174.8) * mm, "end": v(-7386.44, -174.8) * mm});
            skLineSegment(sketch, "E317.left", {"start": v(-11687.94, 79.2) * mm, "end": v(-11687.94, -174.8) * mm});
            skLineSegment(sketch, "E317.right", {"start": v(-7386.44, 79.2) * mm, "end": v(-7386.44, -174.8) * mm});
            skSolve(sketch);
        }
        {
            var Q0;
            Q0 = qSketchRegion(id + "F208", true);
            extrude(context, id + "F209", {"entities" : qUnion([Q0]), "operationType" : NewBodyOperationType.ADD, "depth" : 1219.2 * mm});
        }
        {
            var Q0;
            Q0=makeQuery(id+"F209.boolean.opBoolean","MERGE",FACE,{"derivedFrom":[makeQuery(id+"F207.opExtrude","SWEPT_FACE",FACE,{"disambiguationData":[OSD([sQuery(id+"F206.wireOp",EDGE,"E316.bottom")])]}),makeQuery(id+"F209.opExtrude","SWEPT_FACE",FACE,{"disambiguationData":[OSD([sQuery(id+"F208.wireOp",EDGE,"E317.bottom")])]})]});
            var sketch = newSketch(context, id + "F210", { "sketchPlane" : qUnion([Q0])});
            skLineSegment(sketch, "E318.0", {"start": v(-2508.25, 4644.26) * mm, "end": v(-19.05, 4644.26) * mm});
            skLineSegment(sketch, "E318.1", {"start": v(-19.05, 11713.34) * mm, "end": v(-3727.45, 11713.34) * mm});
            skLineSegment(sketch, "E318.2", {"start": v(-3727.45, 11713.34) * mm, "end": v(-3727.45, 7361.04) * mm});
            skLineSegment(sketch, "E318.3", {"start": v(-19.05, 4644.26) * mm, "end": v(-19.05, 11713.34) * mm});
            skLineSegment(sketch, "E318.4", {"start": v(-3727.45, 7361.04) * mm, "end": v(-2508.25, 7361.04) * mm});
            skLineSegment(sketch, "E318.5", {"start": v(-2508.25, 7361.04) * mm, "end": v(-2508.25, 4644.26) * mm});
            skSolve(sketch);
        }
        {
            var Q0;
            Q0 = qSketchRegion(id + "F210", true);
            extrude(context, id + "F211", {"entities" : qUnion([Q0]), "operationType" : NewBodyOperationType.ADD, "depth" : 25.4 * mm});
        }
        {
            var Q0;
            Q0=makeQuery(id+"F209.opExtrude","CAP_FACE",FACE,{"disambiguationData":[OSD([sQuery(id+"F208.wireOp",EDGE,"E317.bottom"),sQuery(id+"F208.wireOp",EDGE,"E317.top"),sQuery(id+"F208.wireOp",EDGE,"E317.left"),sQuery(id+"F208.wireOp",EDGE,"E317.right")])],"isStart":false});
            var sketch = newSketch(context, id + "F212", { "sketchPlane" : qUnion([Q0])});
            skLineSegment(sketch, "E319", {"start": v(-7829.28, 79.2) * mm, "end": v(-4828.48, -2021.98) * mm});
            skLineSegment(sketch, "E320", {"start": v(-4828.48, -2021.98) * mm, "end": v(-4385.64, -2021.98) * mm});
            skLineSegment(sketch, "E321", {"start": v(-4385.64, -2021.98) * mm, "end": v(-7386.44, 79.2) * mm});
            skLineSegment(sketch, "E322", {"start": v(-7386.44, 79.2) * mm, "end": v(-7829.28, 79.2) * mm});
            skSolve(sketch);
        }
        {
            var Q0;
            Q0 = qSketchRegion(id + "F212", true);
            extrude(context, id + "F213", {"entities" : qUnion([Q0]), "operationType" : NewBodyOperationType.ADD, "depth" : 6.35 * mm, "hasSecondDirection" : true, "secondDirectionOppositeDirection" : true, "secondDirectionDepth" : 31.75 * mm});
        }
        {
            var Q0;
            Q0=makeQuery(id+"F207.opExtrude","CAP_FACE",FACE,{"disambiguationData":[OSD([sQuery(id+"F206.wireOp",EDGE,"E316.bottom"),sQuery(id+"F206.wireOp",EDGE,"E316.top"),sQuery(id+"F206.wireOp",EDGE,"E316.left"),sQuery(id+"F206.wireOp",EDGE,"E316.right")])],"isStart":false});
            var sketch = newSketch(context, id + "F214", { "sketchPlane" : qUnion([Q0])});
            skLineSegment(sketch, "E323.0.0", {"start": v(-4828.48, -2021.98) * mm, "end": v(-4385.64, -2021.98) * mm});
            skLineSegment(sketch, "E323.0.1", {"start": v(-4385.64, -2021.98) * mm, "end": v(-7386.44, 79.2) * mm});
            skLineSegment(sketch, "E323.0.2", {"start": v(-7386.44, 79.2) * mm, "end": v(-7829.28, 79.2) * mm});
            skLineSegment(sketch, "E323.0.3", {"start": v(-7829.28, 79.2) * mm, "end": v(-4828.48, -2021.98) * mm});
            skSolve(sketch);
        }
        {
            var Q0;
            Q0 = qSketchRegion(id + "F214", true);
            extrude(context, id + "F215", {"entities" : qUnion([Q0]), "operationType" : NewBodyOperationType.ADD, "depth" : 38.1 * mm});
        }
        {
            var Q0;
            Q0=makeQuery(id+"F215.opExtrude","CAP_FACE",FACE,{"disambiguationData":[OSD([sQuery(id+"F214.wireOp",EDGE,"E323.0.0"),sQuery(id+"F214.wireOp",EDGE,"E323.0.1"),sQuery(id+"F214.wireOp",EDGE,"E323.0.2"),sQuery(id+"F214.wireOp",EDGE,"E323.0.3")])],"isStart":false});
            var sketch = newSketch(context, id + "F216", { "sketchPlane" : qUnion([Q0])});
            skLineSegment(sketch, "E324.bottom", {"start": v(-7502.8, -124) * mm, "end": v(-7034.57, -124) * mm});
            skLineSegment(sketch, "E324.top", {"start": v(-7502.8, -149.4) * mm, "end": v(-7034.57, -149.4) * mm});
            skLineSegment(sketch, "E324.left", {"start": v(-7502.8, -124) * mm, "end": v(-7502.8, -149.4) * mm});
            skLineSegment(sketch, "E324.right", {"start": v(-7034.57, -124) * mm, "end": v(-7034.57, -149.4) * mm});
            skLineSegment(sketch, "E325.bottom", {"start": v(-7176.33, -352.6) * mm, "end": v(-6708.1, -352.6) * mm});
            skLineSegment(sketch, "E325.top", {"start": v(-7176.33, -378) * mm, "end": v(-6708.1, -378) * mm});
            skLineSegment(sketch, "E325.left", {"start": v(-7176.33, -352.6) * mm, "end": v(-7176.33, -378) * mm});
            skLineSegment(sketch, "E325.right", {"start": v(-6708.1, -352.6) * mm, "end": v(-6708.1, -378) * mm});
            skLineSegment(sketch, "E326.bottom", {"start": v(-6849.85, -581.2) * mm, "end": v(-6381.62, -581.2) * mm});
            skLineSegment(sketch, "E326.top", {"start": v(-6849.85, -606.6) * mm, "end": v(-6381.62, -606.6) * mm});
            skLineSegment(sketch, "E326.left", {"start": v(-6849.85, -581.2) * mm, "end": v(-6849.85, -606.6) * mm});
            skLineSegment(sketch, "E326.right", {"start": v(-6381.62, -581.2) * mm, "end": v(-6381.62, -606.6) * mm});
            skLineSegment(sketch, "E327.bottom", {"start": v(-6523.38, -809.8) * mm, "end": v(-6055.14, -809.8) * mm});
            skLineSegment(sketch, "E327.top", {"start": v(-6523.38, -835.2) * mm, "end": v(-6055.14, -835.2) * mm});
            skLineSegment(sketch, "E327.left", {"start": v(-6523.38, -809.8) * mm, "end": v(-6523.38, -835.2) * mm});
            skLineSegment(sketch, "E327.right", {"start": v(-6055.14, -809.8) * mm, "end": v(-6055.14, -835.2) * mm});
            skLineSegment(sketch, "E328.bottom", {"start": v(-6196.9, -1038.4) * mm, "end": v(-5728.67, -1038.4) * mm});
            skLineSegment(sketch, "E328.top", {"start": v(-6196.9, -1063.8) * mm, "end": v(-5728.67, -1063.8) * mm});
            skLineSegment(sketch, "E328.left", {"start": v(-6196.9, -1038.4) * mm, "end": v(-6196.9, -1063.8) * mm});
            skLineSegment(sketch, "E328.right", {"start": v(-5728.67, -1038.4) * mm, "end": v(-5728.67, -1063.8) * mm});
            skLineSegment(sketch, "E329.bottom", {"start": v(-5870.43, -1267) * mm, "end": v(-5402.2, -1267) * mm});
            skLineSegment(sketch, "E329.top", {"start": v(-5870.43, -1292.4) * mm, "end": v(-5402.2, -1292.4) * mm});
            skLineSegment(sketch, "E329.left", {"start": v(-5870.43, -1267) * mm, "end": v(-5870.43, -1292.4) * mm});
            skLineSegment(sketch, "E329.right", {"start": v(-5402.2, -1267) * mm, "end": v(-5402.2, -1292.4) * mm});
            skLineSegment(sketch, "E330.bottom", {"start": v(-5543.95, -1495.6) * mm, "end": v(-5075.72, -1495.6) * mm});
            skLineSegment(sketch, "E330.top", {"start": v(-5543.95, -1521) * mm, "end": v(-5075.72, -1521) * mm});
            skLineSegment(sketch, "E330.left", {"start": v(-5543.95, -1495.6) * mm, "end": v(-5543.95, -1521) * mm});
            skLineSegment(sketch, "E330.right", {"start": v(-5075.72, -1495.6) * mm, "end": v(-5075.72, -1521) * mm});
            skLineSegment(sketch, "E331", {"start": v(-7361.04, 104.6) * mm, "end": v(-5075.72, -1495.6) * mm, "construction": true});
            skLineSegment(sketch, "E332.bottom", {"start": v(-5217.48, -1749.6) * mm, "end": v(-4749.24, -1749.6) * mm});
            skLineSegment(sketch, "E332.top", {"start": v(-5217.48, -1724.2) * mm, "end": v(-4749.24, -1724.2) * mm});
            skLineSegment(sketch, "E332.left", {"start": v(-5217.48, -1749.6) * mm, "end": v(-5217.48, -1724.2) * mm});
            skLineSegment(sketch, "E332.right", {"start": v(-4749.24, -1749.6) * mm, "end": v(-4749.24, -1724.2) * mm});
            skSolve(sketch);
        }
        {
            var Q0;
            Q0 = qSketchRegion(id + "F216", true);
            var Q1;
            Q1=makeQuery(id+"F213.opExtrude","CAP_FACE",FACE,{"disambiguationData":[OSD([sQuery(id+"F212.wireOp",EDGE,"E319"),sQuery(id+"F212.wireOp",EDGE,"E320"),sQuery(id+"F212.wireOp",EDGE,"E321"),sQuery(id+"F212.wireOp",EDGE,"E322")])],"isStart":true});
            extrude(context, id + "F217", {"entities" : qUnion([Q0]), "operationType" : NewBodyOperationType.ADD, "endBound" : BoundingType.UP_TO_SURFACE, "endBoundEntityFace" : qUnion([Q1]), "depth" : 25.4 * mm});
        }
        {
            var Q0;
            Q0=makeQuery(id+"F211.opExtrude","CAP_FACE",FACE,{"disambiguationData":[OSD([sQuery(id+"F210.wireOp",EDGE,"E318.0"),sQuery(id+"F210.wireOp",EDGE,"E318.1"),sQuery(id+"F210.wireOp",EDGE,"E318.2"),sQuery(id+"F210.wireOp",EDGE,"E318.3"),sQuery(id+"F210.wireOp",EDGE,"E318.4"),sQuery(id+"F210.wireOp",EDGE,"E318.5")])],"isStart":false});
            var sketch = newSketch(context, id + "F218", { "sketchPlane" : qUnion([Q0])});
            skLineSegment(sketch, "E333.bottom", {"start": v(-3651.25, 7538.84) * mm, "end": v(-3549.65, 7538.84) * mm});
            skLineSegment(sketch, "E333.top", {"start": v(-3651.25, 7437.24) * mm, "end": v(-3549.65, 7437.24) * mm});
            skLineSegment(sketch, "E333.left", {"start": v(-3651.25, 7538.84) * mm, "end": v(-3651.25, 7437.24) * mm});
            skLineSegment(sketch, "E333.right", {"start": v(-3549.65, 7538.84) * mm, "end": v(-3549.65, 7437.24) * mm});
            skLineSegment(sketch, "E334.bottom", {"start": v(-3651.25, 8904.94) * mm, "end": v(-3549.65, 8904.94) * mm});
            skLineSegment(sketch, "E334.top", {"start": v(-3651.25, 8803.34) * mm, "end": v(-3549.65, 8803.34) * mm});
            skLineSegment(sketch, "E334.left", {"start": v(-3651.25, 8904.94) * mm, "end": v(-3651.25, 8803.34) * mm});
            skLineSegment(sketch, "E334.right", {"start": v(-3549.65, 8904.94) * mm, "end": v(-3549.65, 8803.34) * mm});
            skLineSegment(sketch, "E335.bottom", {"start": v(-3651.25, 10271.04) * mm, "end": v(-3549.65, 10271.04) * mm});
            skLineSegment(sketch, "E335.top", {"start": v(-3651.25, 10169.44) * mm, "end": v(-3549.65, 10169.44) * mm});
            skLineSegment(sketch, "E335.left", {"start": v(-3651.25, 10271.04) * mm, "end": v(-3651.25, 10169.44) * mm});
            skLineSegment(sketch, "E335.right", {"start": v(-3549.65, 10271.04) * mm, "end": v(-3549.65, 10169.44) * mm});
            skLineSegment(sketch, "E336.bottom", {"start": v(-3651.25, 11637.14) * mm, "end": v(-3549.65, 11637.14) * mm});
            skLineSegment(sketch, "E336.top", {"start": v(-3651.25, 11535.54) * mm, "end": v(-3549.65, 11535.54) * mm});
            skLineSegment(sketch, "E336.left", {"start": v(-3651.25, 11637.14) * mm, "end": v(-3651.25, 11535.54) * mm});
            skLineSegment(sketch, "E336.right", {"start": v(-3549.65, 11637.14) * mm, "end": v(-3549.65, 11535.54) * mm});
            skLineSegment(sketch, "E337.bottom", {"start": v(-1924.05, 11637.14) * mm, "end": v(-1822.45, 11637.14) * mm});
            skLineSegment(sketch, "E337.top", {"start": v(-1924.05, 11535.54) * mm, "end": v(-1822.45, 11535.54) * mm});
            skLineSegment(sketch, "E337.left", {"start": v(-1924.05, 11637.14) * mm, "end": v(-1924.05, 11535.54) * mm});
            skLineSegment(sketch, "E337.right", {"start": v(-1822.45, 11637.14) * mm, "end": v(-1822.45, 11535.54) * mm});
            skLineSegment(sketch, "E338.bottom", {"start": v(-196.85, 11637.14) * mm, "end": v(-95.25, 11637.14) * mm});
            skLineSegment(sketch, "E338.top", {"start": v(-196.85, 11535.54) * mm, "end": v(-95.25, 11535.54) * mm});
            skLineSegment(sketch, "E338.left", {"start": v(-196.85, 11637.14) * mm, "end": v(-196.85, 11535.54) * mm});
            skLineSegment(sketch, "E338.right", {"start": v(-95.25, 11637.14) * mm, "end": v(-95.25, 11535.54) * mm});
            skLineSegment(sketch, "E339.bottom", {"start": v(-2432.05, 7538.84) * mm, "end": v(-2330.45, 7538.84) * mm});
            skLineSegment(sketch, "E339.top", {"start": v(-2432.05, 7437.24) * mm, "end": v(-2330.45, 7437.24) * mm});
            skLineSegment(sketch, "E339.left", {"start": v(-2432.05, 7538.84) * mm, "end": v(-2432.05, 7437.24) * mm});
            skLineSegment(sketch, "E339.right", {"start": v(-2330.45, 7538.84) * mm, "end": v(-2330.45, 7437.24) * mm});
            skLineSegment(sketch, "E340.bottom", {"start": v(-2432.05, 6180.45) * mm, "end": v(-2330.45, 6180.45) * mm});
            skLineSegment(sketch, "E340.top", {"start": v(-2432.05, 6078.85) * mm, "end": v(-2330.45, 6078.85) * mm});
            skLineSegment(sketch, "E340.left", {"start": v(-2432.05, 6180.45) * mm, "end": v(-2432.05, 6078.85) * mm});
            skLineSegment(sketch, "E340.right", {"start": v(-2330.45, 6180.45) * mm, "end": v(-2330.45, 6078.85) * mm});
            skLineSegment(sketch, "E341.bottom", {"start": v(-2432.05, 4822.06) * mm, "end": v(-2330.45, 4822.06) * mm});
            skLineSegment(sketch, "E341.top", {"start": v(-2432.05, 4720.46) * mm, "end": v(-2330.45, 4720.46) * mm});
            skLineSegment(sketch, "E341.left", {"start": v(-2432.05, 4822.06) * mm, "end": v(-2432.05, 4720.46) * mm});
            skLineSegment(sketch, "E341.right", {"start": v(-2330.45, 4822.06) * mm, "end": v(-2330.45, 4720.46) * mm});
            skLineSegment(sketch, "E342.bottom", {"start": v(-196.85, 4822.06) * mm, "end": v(-95.25, 4822.06) * mm});
            skLineSegment(sketch, "E342.top", {"start": v(-196.85, 4720.46) * mm, "end": v(-95.25, 4720.46) * mm});
            skLineSegment(sketch, "E342.left", {"start": v(-196.85, 4822.06) * mm, "end": v(-196.85, 4720.46) * mm});
            skLineSegment(sketch, "E342.right", {"start": v(-95.25, 4822.06) * mm, "end": v(-95.25, 4720.46) * mm});
            skLineSegment(sketch, "E343", {"start": v(-2330.45, 7437.24) * mm, "end": v(-2330.45, 6180.45) * mm, "construction": true});
            skLineSegment(sketch, "E344", {"start": v(-2330.45, 6078.85) * mm, "end": v(-2330.45, 4822.06) * mm, "construction": true});
            skLineSegment(sketch, "E345", {"start": v(-3549.65, 7538.84) * mm, "end": v(-3549.65, 8803.34) * mm, "construction": true});
            skLineSegment(sketch, "E346", {"start": v(-3549.65, 8904.94) * mm, "end": v(-3549.65, 10169.44) * mm, "construction": true});
            skLineSegment(sketch, "E347", {"start": v(-3549.65, 10271.04) * mm, "end": v(-3549.65, 11535.54) * mm, "construction": true});
            skLineSegment(sketch, "E348", {"start": v(-3549.65, 11535.54) * mm, "end": v(-1924.05, 11535.54) * mm, "construction": true});
            skLineSegment(sketch, "E349", {"start": v(-1822.45, 11535.54) * mm, "end": v(-196.85, 11535.54) * mm, "construction": true});
            skLineSegment(sketch, "E350.bottom", {"start": v(-1314.45, 4822.06) * mm, "end": v(-1212.85, 4822.06) * mm});
            skLineSegment(sketch, "E350.top", {"start": v(-1314.45, 4720.46) * mm, "end": v(-1212.85, 4720.46) * mm});
            skLineSegment(sketch, "E350.left", {"start": v(-1314.45, 4822.06) * mm, "end": v(-1314.45, 4720.46) * mm});
            skLineSegment(sketch, "E350.right", {"start": v(-1212.85, 4822.06) * mm, "end": v(-1212.85, 4720.46) * mm});
            skLineSegment(sketch, "E351", {"start": v(-2330.45, 4720.46) * mm, "end": v(-1314.45, 4720.46) * mm, "construction": true});
            skLineSegment(sketch, "E352", {"start": v(-1212.85, 4720.46) * mm, "end": v(-196.85, 4720.46) * mm, "construction": true});
            skSolve(sketch);
        }
        {
            var Q0;
            Q0 = qSketchRegion(id + "F218", true);
            extrude(context, id + "F219", {"entities" : qUnion([Q0]), "operationType" : NewBodyOperationType.ADD, "depth" : 863.6 * mm, "hasSecondDirection" : true, "secondDirectionOppositeDirection" : true, "secondDirectionDepth" : 2540 * mm});
        }
        {
            var Q0;
            Q0=makeQuery(id+"F219.opExtrude","CAP_FACE",FACE,{"disambiguationData":[OSD([sQuery(id+"F218.wireOp",EDGE,"E341.bottom"),sQuery(id+"F218.wireOp",EDGE,"E341.top"),sQuery(id+"F218.wireOp",EDGE,"E341.left"),sQuery(id+"F218.wireOp",EDGE,"E341.right")])],"isStart":false});
            var sketch = newSketch(context, id + "F220", { "sketchPlane" : qUnion([Q0])});
            skLineSegment(sketch, "E353", {"start": v(-2444.75, 7551.54) * mm, "end": v(-2317.75, 7551.54) * mm});
            skLineSegment(sketch, "E354", {"start": v(-2317.75, 7551.54) * mm, "end": v(-2317.75, 4834.76) * mm});
            skLineSegment(sketch, "E355", {"start": v(-2317.75, 4834.76) * mm, "end": v(-82.55, 4834.76) * mm});
            skLineSegment(sketch, "E356", {"start": v(-82.55, 4834.76) * mm, "end": v(-82.55, 4707.76) * mm});
            skLineSegment(sketch, "E357", {"start": v(-82.55, 4707.76) * mm, "end": v(-2444.75, 4707.76) * mm});
            skLineSegment(sketch, "E358", {"start": v(-2444.75, 4707.76) * mm, "end": v(-2444.75, 7551.54) * mm});
            skLineSegment(sketch, "E359", {"start": v(-3536.95, 7424.54) * mm, "end": v(-3536.95, 11522.84) * mm});
            skLineSegment(sketch, "E360", {"start": v(-3536.95, 11522.84) * mm, "end": v(-81.65, 11522.84) * mm});
            skLineSegment(sketch, "E361", {"start": v(-81.65, 11522.84) * mm, "end": v(-81.65, 11649.84) * mm});
            skLineSegment(sketch, "E362", {"start": v(-81.65, 11649.84) * mm, "end": v(-3663.95, 11649.84) * mm});
            skLineSegment(sketch, "E363", {"start": v(-3663.95, 11649.84) * mm, "end": v(-3663.95, 7424.54) * mm});
            skLineSegment(sketch, "E364", {"start": v(-3663.95, 7424.54) * mm, "end": v(-3536.95, 7424.54) * mm});
            skSolve(sketch);
        }
        {
            var Q0;
            Q0 = qSketchRegion(id + "F220", true);
            extrude(context, id + "F221", {"entities" : qUnion([Q0]), "operationType" : NewBodyOperationType.ADD, "depth" : 38.1 * mm});
        }
        {
            var Q0;
            Q0=makeQuery(id+"F221.opExtrude","CAP_FACE",FACE,{"disambiguationData":[OSD([sQuery(id+"F220.wireOp",EDGE,"E359"),sQuery(id+"F220.wireOp",EDGE,"E360"),sQuery(id+"F220.wireOp",EDGE,"E361"),sQuery(id+"F220.wireOp",EDGE,"E362"),sQuery(id+"F220.wireOp",EDGE,"E363"),sQuery(id+"F220.wireOp",EDGE,"E364")])],"isStart":false});
            var sketch = newSketch(context, id + "F222", { "sketchPlane" : qUnion([Q0])});
            skLineSegment(sketch, "E365.0", {"start": v(-56.25, 11675.24) * mm, "end": v(-3689.35, 11675.24) * mm});
            skLineSegment(sketch, "E365.1", {"start": v(-3689.35, 7399.14) * mm, "end": v(-3511.55, 7399.14) * mm});
            skLineSegment(sketch, "E365.2", {"start": v(-3511.55, 7399.14) * mm, "end": v(-3511.55, 11497.44) * mm});
            skLineSegment(sketch, "E365.3", {"start": v(-3689.35, 11675.24) * mm, "end": v(-3689.35, 7399.14) * mm});
            skLineSegment(sketch, "E365.4", {"start": v(-3511.55, 11497.44) * mm, "end": v(-56.25, 11497.44) * mm});
            skLineSegment(sketch, "E365.5", {"start": v(-56.25, 11497.44) * mm, "end": v(-56.25, 11675.24) * mm});
            skLineSegment(sketch, "E366.0", {"start": v(-2292.35, 7576.94) * mm, "end": v(-2470.15, 7576.94) * mm});
            skLineSegment(sketch, "E366.1", {"start": v(-2470.15, 4682.36) * mm, "end": v(-57.15, 4682.36) * mm});
            skLineSegment(sketch, "E366.2", {"start": v(-57.15, 4682.36) * mm, "end": v(-57.15, 4860.16) * mm});
            skLineSegment(sketch, "E366.3", {"start": v(-2470.15, 7576.94) * mm, "end": v(-2470.15, 4682.36) * mm});
            skLineSegment(sketch, "E366.4", {"start": v(-57.15, 4860.16) * mm, "end": v(-2292.35, 4860.16) * mm});
            skLineSegment(sketch, "E366.5", {"start": v(-2292.35, 4860.16) * mm, "end": v(-2292.35, 7576.94) * mm});
            skSolve(sketch);
        }
        {
            var Q0;
            Q0 = qSketchRegion(id + "F222", true);
            extrude(context, id + "F223", {"entities" : qUnion([Q0]), "operationType" : NewBodyOperationType.ADD, "depth" : 25.4 * mm});
        }
        {
            var Q0;
            {var subQ0=sQuery(id+"F218.wireOp",EDGE,"E334.bottom");var subQ1=sQuery(id+"F218.wireOp",EDGE,"E334.left");var subQ2=sQuery(id+"F218.wireOp",EDGE,"E334.top");Q0=makeQuery(id+"F219.boolean.opBoolean","SPLIT",FACE,{"disambiguationData":[TD([makeQuery(id+"F219.opExtrude","CAP_FACE",FACE,{"disambiguationData":[OSD([subQ0,subQ2,subQ1,sQuery(id+"F218.wireOp",EDGE,"E334.right")])],"isStart":false})])],"derivedFrom":makeQuery(id+"F219.opExtrude","SWEPT_FACE",FACE,{"disambiguationData":[OSD([subQ1])]})});}
            cPlane(context, id + "F224", {"entities" : qUnion([Q0]), "cplaneType" : CPlaneType.OFFSET, "offset" : 50.8 * mm, "oppositeDirection" : true, "width" : 152.4 * mm, "height" : 152.4 * mm});
        }
        {
            var Q0;
            Q0=qCreatedBy(id+"F224.planeOp",FACE);
            var sketch = newSketch(context, id + "F225", { "sketchPlane" : qUnion([Q0])});
            skLineSegment(sketch, "E367.bottom", {"start": v(-11535.54, 968.2) * mm, "end": v(-7538.84, 968.2) * mm});
            skLineSegment(sketch, "E367.top", {"start": v(-11535.54, 180.8) * mm, "end": v(-7538.84, 180.8) * mm});
            skLineSegment(sketch, "E367.left", {"start": v(-11535.54, 968.2) * mm, "end": v(-11535.54, 180.8) * mm});
            skLineSegment(sketch, "E367.right", {"start": v(-7538.84, 968.2) * mm, "end": v(-7538.84, 180.8) * mm});
            skLineSegment(sketch, "E368.bottom", {"start": v(-11592.33, 0) * mm, "end": v(-7671.88, 0) * mm});
            skLineSegment(sketch, "E368.top", {"start": v(-11592.33, -1848.93) * mm, "end": v(-7476.93, -1848.93) * mm});
            skLineSegment(sketch, "E368.left", {"start": v(-11592.33, 0) * mm, "end": v(-11592.33, -1848.93) * mm});
            skLineSegment(sketch, "E369", {"start": v(-7671.88, 0) * mm, "end": v(-4804.98, -2007.42) * mm});
            skLineSegment(sketch, "E370", {"start": v(-4745.98, -1848.93) * mm, "end": v(-7476.93, -1848.93) * mm});
            skSolve(sketch);
        }
        {
            var Q0;
            Q0 = qSketchRegion(id + "F225", true);
            extrude(context, id + "F226", {"entities" : qUnion([Q0]), "operationType" : NewBodyOperationType.ADD, "oppositeDirection" : true, "depth" : 6.35 * mm});
        }
        {
            var Q0;
            {var subQ0=sQuery(id+"F218.wireOp",EDGE,"E339.bottom");var subQ1=sQuery(id+"F218.wireOp",EDGE,"E339.left");var subQ2=sQuery(id+"F218.wireOp",EDGE,"E339.top");Q0=makeQuery(id+"F219.boolean.opBoolean","SPLIT",FACE,{"disambiguationData":[TD([makeQuery(id+"F219.opExtrude","CAP_FACE",FACE,{"disambiguationData":[OSD([subQ0,subQ2,subQ1,sQuery(id+"F218.wireOp",EDGE,"E339.right")])],"isStart":false})])],"derivedFrom":makeQuery(id+"F219.opExtrude","SWEPT_FACE",FACE,{"disambiguationData":[OSD([subQ1])]})});}
            cPlane(context, id + "F227", {"entities" : qUnion([Q0]), "cplaneType" : CPlaneType.OFFSET, "offset" : 50.8 * mm, "oppositeDirection" : true, "width" : 152.4 * mm, "height" : 152.4 * mm});
        }
        {
            var Q0;
            Q0=qCreatedBy(id+"F227.planeOp",FACE);
            var sketch = newSketch(context, id + "F228", { "sketchPlane" : qUnion([Q0])});
            skLineSegment(sketch, "E371.bottom", {"start": v(-7437.24, 968.2) * mm, "end": v(-4822.06, 968.2) * mm});
            skLineSegment(sketch, "E371.top", {"start": v(-7437.24, 180.8) * mm, "end": v(-4822.06, 180.8) * mm});
            skLineSegment(sketch, "E371.left", {"start": v(-7437.24, 968.2) * mm, "end": v(-7437.24, 180.8) * mm});
            skLineSegment(sketch, "E371.right", {"start": v(-4822.06, 968.2) * mm, "end": v(-4822.06, 180.8) * mm});
            skLineSegment(sketch, "E372.bottom", {"start": v(-7483.58, -45.51) * mm, "end": v(-4769.55, -45.51) * mm});
            skLineSegment(sketch, "E372.top", {"start": v(-7483.58, -1876.88) * mm, "end": v(-4769.55, -1876.88) * mm});
            skLineSegment(sketch, "E372.left", {"start": v(-7483.58, -45.51) * mm, "end": v(-7483.58, -1876.88) * mm});
            skLineSegment(sketch, "E372.right", {"start": v(-4769.55, -45.51) * mm, "end": v(-4769.55, -1876.88) * mm});
            skSolve(sketch);
        }
        {
            var Q0;
            Q0 = qSketchRegion(id + "F228", true);
            extrude(context, id + "F229", {"entities" : qUnion([Q0]), "operationType" : NewBodyOperationType.ADD, "oppositeDirection" : true, "depth" : 6.35 * mm});
        }
        {
            var Q0;
            {var subQ0=sQuery(id+"F218.wireOp",EDGE,"E341.right");var subQ1=sQuery(id+"F218.wireOp",EDGE,"E341.left");var subQ2=sQuery(id+"F218.wireOp",EDGE,"E341.top");Q0=makeQuery(id+"F219.boolean.opBoolean","SPLIT",FACE,{"disambiguationData":[TD([makeQuery(id+"F219.opExtrude","CAP_FACE",FACE,{"disambiguationData":[OSD([sQuery(id+"F218.wireOp",EDGE,"E341.bottom"),subQ2,subQ1,subQ0])],"isStart":false})])],"derivedFrom":makeQuery(id+"F219.opExtrude","SWEPT_FACE",FACE,{"disambiguationData":[OSD([subQ2])]})});}
            cPlane(context, id + "F230", {"entities" : qUnion([Q0]), "cplaneType" : CPlaneType.OFFSET, "offset" : 50.8 * mm, "oppositeDirection" : true, "width" : 152.4 * mm, "height" : 152.4 * mm});
        }
        {
            var Q0;
            Q0=qCreatedBy(id+"F230.planeOp",FACE);
            var sketch = newSketch(context, id + "F231", { "sketchPlane" : qUnion([Q0])});
            skLineSegment(sketch, "E373.bottom", {"start": v(-2330.45, 968.2) * mm, "end": v(-196.85, 968.2) * mm});
            skLineSegment(sketch, "E373.top", {"start": v(-2330.45, 180.8) * mm, "end": v(-196.85, 180.8) * mm});
            skLineSegment(sketch, "E373.left", {"start": v(-2330.45, 968.2) * mm, "end": v(-2330.45, 180.8) * mm});
            skLineSegment(sketch, "E373.right", {"start": v(-196.85, 968.2) * mm, "end": v(-196.85, 180.8) * mm});
            skLineSegment(sketch, "E374.bottom", {"start": v(-2384.42, -103.18) * mm, "end": v(-131.8, -103.18) * mm});
            skLineSegment(sketch, "E374.top", {"start": v(-2384.42, -1643.97) * mm, "end": v(-131.8, -1643.97) * mm});
            skLineSegment(sketch, "E374.left", {"start": v(-2384.42, -103.18) * mm, "end": v(-2384.42, -1643.97) * mm});
            skLineSegment(sketch, "E374.right", {"start": v(-131.8, -103.18) * mm, "end": v(-131.8, -1643.97) * mm});
            skSolve(sketch);
        }
        {
            var Q0;
            Q0 = qSketchRegion(id + "F231", true);
            extrude(context, id + "F232", {"entities" : qUnion([Q0]), "operationType" : NewBodyOperationType.ADD, "oppositeDirection" : true, "depth" : 6.35 * mm});
        }
        {
            var Q0;
            {var subQ0=sQuery(id+"F218.wireOp",EDGE,"E336.right");var subQ1=sQuery(id+"F218.wireOp",EDGE,"E336.left");var subQ2=sQuery(id+"F218.wireOp",EDGE,"E336.bottom");Q0=makeQuery(id+"F219.boolean.opBoolean","SPLIT",FACE,{"disambiguationData":[TD([makeQuery(id+"F219.opExtrude","CAP_FACE",FACE,{"disambiguationData":[OSD([subQ2,sQuery(id+"F218.wireOp",EDGE,"E336.top"),subQ1,subQ0])],"isStart":false})])],"derivedFrom":makeQuery(id+"F219.opExtrude","SWEPT_FACE",FACE,{"disambiguationData":[OSD([subQ2])]})});}
            cPlane(context, id + "F233", {"entities" : qUnion([Q0]), "cplaneType" : CPlaneType.OFFSET, "offset" : 50.8 * mm, "oppositeDirection" : true, "width" : 152.4 * mm, "height" : 152.4 * mm});
        }
        {
            var Q0;
            Q0=qCreatedBy(id+"F233.planeOp",FACE);
            var sketch = newSketch(context, id + "F234", { "sketchPlane" : qUnion([Q0])});
            skLineSegment(sketch, "E375.bottom", {"start": v(196.85, 968.2) * mm, "end": v(3549.65, 968.2) * mm});
            skLineSegment(sketch, "E375.top", {"start": v(196.85, 180.8) * mm, "end": v(3549.65, 180.8) * mm});
            skLineSegment(sketch, "E375.left", {"start": v(196.85, 968.2) * mm, "end": v(196.85, 180.8) * mm});
            skLineSegment(sketch, "E375.right", {"start": v(3549.65, 968.2) * mm, "end": v(3549.65, 180.8) * mm});
            skLineSegment(sketch, "E376.bottom", {"start": v(91.67, -98.3) * mm, "end": v(3597.45, -98.3) * mm});
            skLineSegment(sketch, "E376.top", {"start": v(91.67, -1864.88) * mm, "end": v(3597.45, -1864.88) * mm});
            skLineSegment(sketch, "E376.left", {"start": v(91.67, -98.3) * mm, "end": v(91.67, -1864.88) * mm});
            skLineSegment(sketch, "E376.right", {"start": v(3597.45, -98.3) * mm, "end": v(3597.45, -1864.88) * mm});
            skSolve(sketch);
        }
        {
            var Q0;
            Q0 = qSketchRegion(id + "F234", true);
            extrude(context, id + "F235", {"entities" : qUnion([Q0]), "operationType" : NewBodyOperationType.ADD, "oppositeDirection" : true, "depth" : 6.35 * mm});
        }
        {
            var Q0;
            {var subQ0=sQuery(id+"F234.wireOp",EDGE,"E375.top");Q0=makeQuery(id+"F235.boolean.opBoolean","SPLIT",FACE,{"disambiguationData":[TD([makeQuery(id+"F219.opExtrude","SWEPT_FACE",FACE,{"disambiguationData":[OSD([sQuery(id+"F218.wireOp",EDGE,"E337.right")])]})])],"derivedFrom":makeQuery(id+"F235.opExtrude","CAP_FACE",FACE,{"disambiguationData":[OSD([sQuery(id+"F234.wireOp",EDGE,"E375.bottom"),subQ0,sQuery(id+"F234.wireOp",EDGE,"E375.left"),sQuery(id+"F234.wireOp",EDGE,"E375.right")])],"isStart":true})});}
            var sketch = newSketch(context, id + "F236", { "sketchPlane" : qUnion([Q0])});
            skLineSegment(sketch, "E377.bottom", {"start": v(196.85, 180.8) * mm, "end": v(3585.18, 180.8) * mm});
            skLineSegment(sketch, "E377.top", {"start": v(196.85, 257) * mm, "end": v(3585.18, 257) * mm});
            skLineSegment(sketch, "E377.left", {"start": v(196.85, 180.8) * mm, "end": v(196.85, 257) * mm});
            skLineSegment(sketch, "E377.right", {"start": v(3585.18, 180.8) * mm, "end": v(3585.18, 257) * mm});
            skLineSegment(sketch, "E378.bottom", {"start": v(196.85, 968.2) * mm, "end": v(3607.72, 968.2) * mm});
            skLineSegment(sketch, "E378.top", {"start": v(196.85, 892) * mm, "end": v(3607.72, 892) * mm});
            skLineSegment(sketch, "E378.left", {"start": v(196.85, 968.2) * mm, "end": v(196.85, 892) * mm});
            skLineSegment(sketch, "E378.right", {"start": v(3607.72, 968.2) * mm, "end": v(3607.72, 892) * mm});
            skSolve(sketch);
        }
        {
            var Q0;
            Q0 = qSketchRegion(id + "F236", true);
            extrude(context, id + "F237", {"entities" : qUnion([Q0]), "operationType" : NewBodyOperationType.ADD, "depth" : 25.4 * mm, "hasSecondDirection" : true, "secondDirectionOppositeDirection" : true, "secondDirectionDepth" : 25.4 * mm});
        }
        {
            var Q0;
            {var subQ0=sQuery(id+"F225.wireOp",EDGE,"E367.top");Q0=makeQuery(id+"F226.boolean.opBoolean","SPLIT",FACE,{"disambiguationData":[TD([makeQuery(id+"F219.opExtrude","SWEPT_FACE",FACE,{"disambiguationData":[OSD([sQuery(id+"F218.wireOp",EDGE,"E335.bottom")])]})])],"derivedFrom":makeQuery(id+"F226.opExtrude","CAP_FACE",FACE,{"disambiguationData":[OSD([sQuery(id+"F225.wireOp",EDGE,"E367.bottom"),subQ0,sQuery(id+"F225.wireOp",EDGE,"E367.left"),sQuery(id+"F225.wireOp",EDGE,"E367.right")])],"isStart":true})});}
            var sketch = newSketch(context, id + "F238", { "sketchPlane" : qUnion([Q0])});
            skLineSegment(sketch, "E379.bottom", {"start": v(-11535.54, 968.2) * mm, "end": v(-7485.72, 968.2) * mm});
            skLineSegment(sketch, "E379.top", {"start": v(-11535.54, 892) * mm, "end": v(-7485.72, 892) * mm});
            skLineSegment(sketch, "E379.left", {"start": v(-11535.54, 968.2) * mm, "end": v(-11535.54, 892) * mm});
            skLineSegment(sketch, "E379.right", {"start": v(-7485.72, 968.2) * mm, "end": v(-7485.72, 892) * mm});
            skLineSegment(sketch, "E380.bottom", {"start": v(-11535.54, 180.8) * mm, "end": v(-7509.74, 180.8) * mm});
            skLineSegment(sketch, "E380.top", {"start": v(-11535.54, 257) * mm, "end": v(-7509.74, 257) * mm});
            skLineSegment(sketch, "E380.left", {"start": v(-11535.54, 180.8) * mm, "end": v(-11535.54, 257) * mm});
            skLineSegment(sketch, "E380.right", {"start": v(-7509.74, 180.8) * mm, "end": v(-7509.74, 257) * mm});
            skSolve(sketch);
        }
        {
            var Q0;
            Q0 = qSketchRegion(id + "F238", true);
            extrude(context, id + "F239", {"entities" : qUnion([Q0]), "operationType" : NewBodyOperationType.ADD, "depth" : 25.4 * mm, "hasSecondDirection" : true, "secondDirectionOppositeDirection" : true, "secondDirectionDepth" : 25.4 * mm});
        }
        {
            var Q0;
            {var subQ0=sQuery(id+"F228.wireOp",EDGE,"E371.top");Q0=makeQuery(id+"F229.boolean.opBoolean","SPLIT",FACE,{"disambiguationData":[TD([makeQuery(id+"F219.opExtrude","SWEPT_FACE",FACE,{"disambiguationData":[OSD([sQuery(id+"F218.wireOp",EDGE,"E339.top")])]})])],"derivedFrom":makeQuery(id+"F229.opExtrude","CAP_FACE",FACE,{"disambiguationData":[OSD([sQuery(id+"F228.wireOp",EDGE,"E371.bottom"),subQ0,sQuery(id+"F228.wireOp",EDGE,"E371.left"),sQuery(id+"F228.wireOp",EDGE,"E371.right")])],"isStart":true})});}
            var sketch = newSketch(context, id + "F240", { "sketchPlane" : qUnion([Q0])});
            skLineSegment(sketch, "E381.bottom", {"start": v(-7437.24, 968.2) * mm, "end": v(-4770.83, 968.2) * mm});
            skLineSegment(sketch, "E381.top", {"start": v(-7437.24, 892) * mm, "end": v(-4770.83, 892) * mm});
            skLineSegment(sketch, "E381.left", {"start": v(-7437.24, 968.2) * mm, "end": v(-7437.24, 892) * mm});
            skLineSegment(sketch, "E381.right", {"start": v(-4770.83, 968.2) * mm, "end": v(-4770.83, 892) * mm});
            skLineSegment(sketch, "E382.bottom", {"start": v(-7437.24, 180.8) * mm, "end": v(-4764.82, 180.8) * mm});
            skLineSegment(sketch, "E382.top", {"start": v(-7437.24, 257) * mm, "end": v(-4764.82, 257) * mm});
            skLineSegment(sketch, "E382.left", {"start": v(-7437.24, 180.8) * mm, "end": v(-7437.24, 257) * mm});
            skLineSegment(sketch, "E382.right", {"start": v(-4764.82, 180.8) * mm, "end": v(-4764.82, 257) * mm});
            skSolve(sketch);
        }
        {
            var Q0;
            Q0 = qSketchRegion(id + "F240", true);
            extrude(context, id + "F241", {"entities" : qUnion([Q0]), "operationType" : NewBodyOperationType.ADD, "depth" : 25.4 * mm, "hasSecondDirection" : true, "secondDirectionOppositeDirection" : true, "secondDirectionDepth" : 25.4 * mm});
        }
        {
            var Q0;
            {var subQ0=sQuery(id+"F231.wireOp",EDGE,"E373.top");Q0=makeQuery(id+"F232.boolean.opBoolean","SPLIT",FACE,{"disambiguationData":[TD([makeQuery(id+"F219.opExtrude","SWEPT_FACE",FACE,{"disambiguationData":[OSD([sQuery(id+"F218.wireOp",EDGE,"E341.right")])]})])],"derivedFrom":makeQuery(id+"F232.opExtrude","CAP_FACE",FACE,{"disambiguationData":[OSD([sQuery(id+"F231.wireOp",EDGE,"E373.bottom"),subQ0,sQuery(id+"F231.wireOp",EDGE,"E373.left"),sQuery(id+"F231.wireOp",EDGE,"E373.right")])],"isStart":true})});}
            var sketch = newSketch(context, id + "F242", { "sketchPlane" : qUnion([Q0])});
            skLineSegment(sketch, "E383.bottom", {"start": v(-2330.45, 968.2) * mm, "end": v(-157.59, 968.2) * mm});
            skLineSegment(sketch, "E383.top", {"start": v(-2330.45, 892) * mm, "end": v(-157.59, 892) * mm});
            skLineSegment(sketch, "E383.left", {"start": v(-2330.45, 968.2) * mm, "end": v(-2330.45, 892) * mm});
            skLineSegment(sketch, "E383.right", {"start": v(-157.59, 968.2) * mm, "end": v(-157.59, 892) * mm});
            skLineSegment(sketch, "E384.bottom", {"start": v(-2330.45, 180.8) * mm, "end": v(-151.2, 180.8) * mm});
            skLineSegment(sketch, "E384.top", {"start": v(-2330.45, 257) * mm, "end": v(-151.2, 257) * mm});
            skLineSegment(sketch, "E384.left", {"start": v(-2330.45, 180.8) * mm, "end": v(-2330.45, 257) * mm});
            skLineSegment(sketch, "E384.right", {"start": v(-151.2, 180.8) * mm, "end": v(-151.2, 257) * mm});
            skSolve(sketch);
        }
        {
            var Q0;
            Q0 = qSketchRegion(id + "F242", true);
            extrude(context, id + "F243", {"entities" : qUnion([Q0]), "operationType" : NewBodyOperationType.ADD, "depth" : 25.4 * mm, "hasSecondDirection" : true, "secondDirectionOppositeDirection" : true, "secondDirectionDepth" : 25.4 * mm});
        }
        {
            var Q0;
            {var subQ0=sQuery(id+"F218.wireOp",EDGE,"E333.bottom");var subQ1=sQuery(id+"F218.wireOp",EDGE,"E333.left");var subQ2=sQuery(id+"F218.wireOp",EDGE,"E333.top");Q0=makeQuery(id+"F219.boolean.opBoolean","SPLIT",FACE,{"disambiguationData":[TD([makeQuery(id+"F219.opExtrude","CAP_FACE",FACE,{"disambiguationData":[OSD([subQ0,subQ2,subQ1,sQuery(id+"F218.wireOp",EDGE,"E333.right")])],"isStart":false})])],"derivedFrom":makeQuery(id+"F219.opExtrude","SWEPT_FACE",FACE,{"disambiguationData":[OSD([subQ1])]})});}
            var sketch = newSketch(context, id + "F244", { "sketchPlane" : qUnion([Q0])});
            skLineSegment(sketch, "E385", {"start": v(-7488.04, 917.4) * mm, "end": v(-7218.02, 917.4) * mm});
            skLineSegment(sketch, "E386", {"start": v(-7218.02, 917.4) * mm, "end": v(-4742.8, -815.77) * mm});
            skLineSegment(sketch, "E387", {"start": v(-4742.8, -815.77) * mm, "end": v(-4742.8, -877.79) * mm});
            skLineSegment(sketch, "E388", {"start": v(-4742.8, -877.79) * mm, "end": v(-7234.04, 866.6) * mm});
            skLineSegment(sketch, "E389", {"start": v(-7234.04, 866.6) * mm, "end": v(-7488.04, 866.6) * mm});
            skLineSegment(sketch, "E390", {"start": v(-7488.04, 866.6) * mm, "end": v(-7488.04, 917.4) * mm});
            skSolve(sketch);
        }
        {
            var Q0;
            Q0 = qSketchRegion(id + "F244", true);
            extrude(context, id + "F245", {"entities" : qUnion([Q0]), "operationType" : NewBodyOperationType.ADD, "depth" : 38.1 * mm, "hasSecondDirection" : true, "secondDirectionOppositeDirection" : true, "secondDirectionDepth" : 50.8 * mm});
        }
        {
            var Q0;
            Q0=makeQuery(id+"F245.opExtrude","CAP_FACE",FACE,{"disambiguationData":[OSD([sQuery(id+"F244.wireOp",EDGE,"E385"),sQuery(id+"F244.wireOp",EDGE,"E386"),sQuery(id+"F244.wireOp",EDGE,"E387"),sQuery(id+"F244.wireOp",EDGE,"E388"),sQuery(id+"F244.wireOp",EDGE,"E389"),sQuery(id+"F244.wireOp",EDGE,"E390")])],"isStart":false});
            var sketch = newSketch(context, id + "F246", { "sketchPlane" : qUnion([Q0])});
            skLineSegment(sketch, "E391", {"start": v(-7218.02, 917.4) * mm, "end": v(-7518.17, 917.4) * mm});
            skLineSegment(sketch, "E392", {"start": v(-7518.17, 917.4) * mm, "end": v(-7518.17, 942.8) * mm});
            skLineSegment(sketch, "E393", {"start": v(-7518.17, 942.8) * mm, "end": v(-7216.2, 942.8) * mm});
            skLineSegment(sketch, "E394", {"start": v(-7216.2, 942.8) * mm, "end": v(-4704.7, -815.77) * mm});
            skLineSegment(sketch, "E395", {"start": v(-4704.7, -842.45) * mm, "end": v(-7218.02, 917.4) * mm});
            skLineSegment(sketch, "E396", {"start": v(-4704.7, -842.45) * mm, "end": v(-4704.7, -815.77) * mm});
            skSolve(sketch);
        }
        {
            var Q0;
            Q0 = qSketchRegion(id + "F246", true);
            extrude(context, id + "F247", {"entities" : qUnion([Q0]), "operationType" : NewBodyOperationType.ADD, "depth" : 25.4 * mm, "hasSecondDirection" : true, "secondDirectionOppositeDirection" : true, "secondDirectionDepth" : 114.3 * mm});
        }
        {
            var Q0;
            Q0=makeQuery(id+"F217.opExtrude","SWEPT_FACE",FACE,{"disambiguationData":[OSD([sQuery(id+"F216.wireOp",EDGE,"E327.bottom")])]});
            var sketch = newSketch(context, id + "F248", { "sketchPlane" : qUnion([Q0])});
            skLineSegment(sketch, "E397.bottom", {"start": v(-3676.65, 6296.08) * mm, "end": v(-3587.75, 6296.08) * mm});
            skLineSegment(sketch, "E397.top", {"start": v(-3676.65, 6207.18) * mm, "end": v(-3587.75, 6207.18) * mm});
            skLineSegment(sketch, "E397.left", {"start": v(-3676.65, 6296.08) * mm, "end": v(-3676.65, 6207.18) * mm});
            skLineSegment(sketch, "E397.right", {"start": v(-3587.75, 6296.08) * mm, "end": v(-3587.75, 6207.18) * mm});
            skSolve(sketch);
        }
        {
            var Q0;
            Q0 = qSketchRegion(id + "F248", true);
            var Q1;
            Q1=makeQuery(id+"F245.opExtrude","SWEPT_FACE",FACE,{"disambiguationData":[OSD([sQuery(id+"F244.wireOp",EDGE,"E388")])]});
            extrude(context, id + "F249", {"entities" : qUnion([Q0]), "operationType" : NewBodyOperationType.ADD, "endBound" : BoundingType.UP_TO_SURFACE, "endBoundEntityFace" : qUnion([Q1]), "depth" : 25.4 * mm, "hasSecondDirection" : true, "secondDirectionOppositeDirection" : true, "secondDirectionDepth" : 1524 * mm});
        }
        {
            var Q0;
            Q0=makeQuery(id+"F217.opExtrude","SWEPT_FACE",FACE,{"disambiguationData":[OSD([sQuery(id+"F216.wireOp",EDGE,"E332.top")])]});
            var sketch = newSketch(context, id + "F250", { "sketchPlane" : qUnion([Q0])});
            skLineSegment(sketch, "E398.bottom", {"start": v(-3676.65, 4850.84) * mm, "end": v(-3587.75, 4850.84) * mm});
            skLineSegment(sketch, "E398.top", {"start": v(-3676.65, 4939.74) * mm, "end": v(-3587.75, 4939.74) * mm});
            skLineSegment(sketch, "E398.left", {"start": v(-3676.65, 4850.84) * mm, "end": v(-3676.65, 4939.74) * mm});
            skLineSegment(sketch, "E398.right", {"start": v(-3587.75, 4850.84) * mm, "end": v(-3587.75, 4939.74) * mm});
            skSolve(sketch);
        }
        {
            var Q0;
            Q0 = qSketchRegion(id + "F250", true);
            var Q1;
            Q1=makeQuery(id+"F245.opExtrude","SWEPT_FACE",FACE,{"disambiguationData":[OSD([sQuery(id+"F244.wireOp",EDGE,"E388")])]});
            extrude(context, id + "F251", {"entities" : qUnion([Q0]), "operationType" : NewBodyOperationType.ADD, "endBound" : BoundingType.UP_TO_SURFACE, "endBoundEntityFace" : qUnion([Q1]), "depth" : 25.4 * mm});
        }
        {
            var Q0;
            {var subQ0=sQuery(id+"F238.wireOp",EDGE,"E380.bottom");var subQ1=sQuery(id+"F238.wireOp",EDGE,"E380.top");Q0=makeQuery(id+"F239.boolean.opBoolean","SPLIT",FACE,{"disambiguationData":[TD([makeQuery(id+"F219.opExtrude","SWEPT_FACE",FACE,{"disambiguationData":[OSD([sQuery(id+"F218.wireOp",EDGE,"E333.bottom")])]})])],"derivedFrom":makeQuery(id+"F239.opExtrude","CAP_FACE",FACE,{"disambiguationData":[OSD([subQ0,subQ1,sQuery(id+"F238.wireOp",EDGE,"E380.left"),sQuery(id+"F238.wireOp",EDGE,"E380.right")])],"isStart":false})});}
            var sketch = newSketch(context, id + "F252", { "sketchPlane" : qUnion([Q0])});
            skFitSpline(sketch, "E399", {"points": [v(-7459.34, 662.97) * mm, v(-7205.23, 587.27) * mm, v(-7105.94, 392.55) * mm, v(-6849.33, 203.25) * mm, v(-6546.46, 0) * mm, v(-6403.43, -175.35) * mm, v(-6024.68, -323.9) * mm, v(-5613.57, -724.92) * mm, v(-5139.41, -868.52) * mm, v(-4920.05, -1167.3) * mm], "startDerivative": vector(2942.99, -243.21) * mm, "endDerivative": vector(-418.62, 1141.9) * mm});
            skFitSpline(sketch, "E400.0", {"points": [v(-7469.8, 536.4) * mm, v(-7462.53, 535.8) * mm, v(-7448.07, 534.54) * mm, v(-7426.79, 532.37) * mm, v(-7406.14, 529.86) * mm, v(-7386.38, 526.95) * mm, v(-7367.78, 523.62) * mm, v(-7350.63, 519.88) * mm, v(-7335.24, 515.76) * mm, v(-7321.94, 511.4) * mm, v(-7311.03, 506.97) * mm, v(-7304.16, 503.5) * mm, v(-7300.04, 501.07) * mm, v(-7298.04, 499.74) * mm, v(-7296.76, 498.81) * mm, v(-7295.96, 498.2) * mm, v(-7295.3, 497.66) * mm, v(-7294.88, 497.3) * mm, v(-7294.6, 497.05) * mm, v(-7294.46, 496.9) * mm, v(-7294.36, 496.81) * mm, v(-7294.27, 496.72) * mm, v(-7294.15, 496.6) * mm, v(-7293.99, 496.43) * mm, v(-7293.75, 496.17) * mm, v(-7293.4, 495.78) * mm, v(-7292.9, 495.18) * mm, v(-7292.12, 494.2) * mm, v(-7290.94, 492.56) * mm, v(-7289.2, 489.9) * mm, v(-7287.2, 486.45) * mm, v(-7284.94, 482.22) * mm, v(-7281.66, 475.5) * mm, v(-7277.1, 465.14) * mm, v(-7270.98, 449.75) * mm, v(-7264.13, 431.72) * mm, v(-7257.6, 414.71) * mm, v(-7251.7, 400.07) * mm, v(-7246.86, 388.6) * mm, v(-7241.55, 376.68) * mm, v(-7235.68, 364.35) * mm, v(-7230.27, 353.79) * mm, v(-7225.58, 345.2) * mm, v(-7221.87, 338.68) * mm, v(-7217.96, 332.1) * mm, v(-7214.53, 326.6) * mm, v(-7211.67, 322.17) * mm, v(-7209.5, 318.88) * mm, v(-7207.3, 315.63) * mm, v(-7204.33, 311.33) * mm, v(-7200.55, 306.05) * mm, v(-7195.91, 299.83) * mm, v(-7191.19, 293.75) * mm, v(-7184.76, 285.8) * mm, v(-7176.53, 276.18) * mm, v(-7162.97, 261.42) * mm, v(-7145.4, 244.1) * mm, v(-7123.51, 224.9) * mm, v(-7101.03, 207.05) * mm, v(-7078.08, 190.36) * mm, v(-7054.77, 174.65) * mm, v(-7031.19, 159.74) * mm, v(-7007.42, 145.5) * mm, v(-6983.54, 131.78) * mm, v(-6959.64, 118.5) * mm, v(-6939.78, 107.7) * mm, v(-6923.96, 99.17) * mm, v(-6914.12, 93.89) * mm, v(-6906.28, 89.68) * mm, v(-6898.44, 85.48) * mm, v(-6888.68, 80.24) * mm, v(-6877.01, 73.96) * mm, v(-6861.55, 65.62) * mm, v(-6842.42, 55.2) * mm, v(-6819.9, 42.74) * mm, v(-6797.96, 30.28) * mm, v(-6776.7, 17.85) * mm, v(-6756.26, 5.43) * mm, v(-6736.77, -6.95) * mm, v(-6718.37, -19.26) * mm, v(-6701.19, -31.47) * mm, v(-6688, -41.5) * mm, v(-6678.19, -49.4) * mm, v(-6671.21, -55.26) * mm, v(-6664.64, -61.04) * mm, v(-6658.49, -66.7) * mm, v(-6653.7, -71.34) * mm, v(-6650.1, -74.97) * mm, v(-6647.5, -77.66) * mm, v(-6645.02, -80.32) * mm, v(-6643.24, -82.28) * mm, v(-6642.09, -83.57) * mm, v(-6641.33, -84.43) * mm, v(-6640, -85.94) * mm, v(-6638.12, -88.15) * mm, v(-6635.86, -90.88) * mm, v(-6633.6, -93.7) * mm, v(-6631.32, -96.6) * mm, v(-6626.75, -102.56) * mm, v(-6619.8, -112.19) * mm, v(-6610.08, -126.58) * mm, v(-6599.67, -142.54) * mm, v(-6588.26, -160.03) * mm, v(-6575.46, -178.95) * mm, v(-6563.23, -195.71) * mm, v(-6552.25, -209.56) * mm, v(-6543.35, -220.1) * mm, v(-6533.72, -230.7) * mm, v(-6523.32, -241.31) * mm, v(-6513.96, -250.06) * mm, v(-6506.05, -256.95) * mm, v(-6499.9, -262.06) * mm, v(-6493.55, -267.08) * mm, v(-6488.07, -271.18) * mm, v(-6483.58, -274.4) * mm, v(-6480.17, -276.8) * mm, v(-6476.7, -279.16) * mm, v(-6473.77, -281.1) * mm, v(-6471.4, -282.64) * mm, v(-6469.02, -284.15) * mm, v(-6466.06, -286) * mm, v(-6462.5, -288.16) * mm, v(-6457.76, -290.96) * mm, v(-6451.83, -294.32) * mm, v(-6444.73, -298.14) * mm, v(-6437.64, -301.76) * mm, v(-6428.22, -306.34) * mm, v(-6416.5, -311.64) * mm, v(-6402.53, -317.42) * mm, v(-6388.66, -322.73) * mm, v(-6374.9, -327.62) * mm, v(-6356.7, -333.7) * mm, v(-6334.18, -340.63) * mm, v(-6307.58, -348.26) * mm, v(-6281.43, -355.53) * mm, v(-6255.8, -362.72) * mm, v(-6230.82, -370.03) * mm, v(-6206.6, -377.67) * mm, v(-6183.27, -385.78) * mm, v(-6160.99, -394.48) * mm, v(-6143.38, -402.3) * mm, v(-6129.92, -408.97) * mm, v(-6121.78, -413.3) * mm, v(-6115.42, -416.88) * mm, v(-6110.73, -419.62) * mm, v(-6106.12, -422.41) * mm, v(-6101.6, -425.27) * mm, v(-6097.88, -427.7) * mm, v(-6094.96, -429.67) * mm, v(-6092.02, -431.7) * mm, v(-6088.32, -434.32) * mm, v(-6082.35, -438.7) * mm, v(-6074.79, -444.55) * mm, v(-6065.57, -452.13) * mm, v(-6056.22, -460.27) * mm, v(-6046.75, -468.94) * mm, v(-6037.16, -478.13) * mm, v(-6024.25, -491.02) * mm, v(-6007.87, -508.29) * mm, v(-5987.86, -530.6) * mm, v(-5967.52, -554.26) * mm, v(-5946.79, -579) * mm, v(-5925.62, -604.54) * mm, v(-5903.91, -630.66) * mm, v(-5881.56, -657.1) * mm, v(-5858.4, -683.62) * mm, v(-5834.24, -709.96) * mm, v(-5808.87, -735.87) * mm, v(-5786.49, -756.88) * mm, v(-5767.69, -773.19) * mm, v(-5753.1, -785.11) * mm, v(-5737.98, -796.68) * mm, v(-5724.9, -805.98) * mm, v(-5714.13, -813.19) * mm, v(-5705.9, -818.46) * mm, v(-5697.5, -823.6) * mm, v(-5690.36, -827.76) * mm, v(-5684.57, -831) * mm, v(-5680.18, -833.4) * mm, v(-5675.75, -835.75) * mm, v(-5672.02, -837.67) * mm, v(-5669.02, -839.19) * mm, v(-5666.02, -840.68) * mm, v(-5662.27, -842.5) * mm, v(-5657.77, -844.63) * mm, v(-5651.77, -847.38) * mm, v(-5644.27, -850.66) * mm, v(-5635.29, -854.36) * mm, v(-5626.34, -857.83) * mm, v(-5614.44, -862.17) * mm, v(-5599.68, -867.07) * mm, v(-5576.34, -873.92) * mm, v(-5547.78, -880.84) * mm, v(-5514.7, -887.17) * mm, v(-5482.9, -892.12) * mm, v(-5452.43, -896.22) * mm, v(-5423.36, -899.91) * mm, v(-5395.73, -903.58) * mm, v(-5369.6, -907.54) * mm, v(-5345.03, -912.05) * mm, v(-5322.05, -917.3) * mm, v(-5300.64, -923.47) * mm, v(-5280.66, -930.7) * mm, v(-5265.03, -937.75) * mm, v(-5252.96, -944.15) * mm, v(-5245.56, -948.5) * mm, v(-5239.7, -952.24) * mm, v(-5235.33, -955.16) * mm, v(-5230.97, -958.22) * mm, v(-5227.36, -960.9) * mm, v(-5224.46, -963.12) * mm, v(-5222.3, -964.82) * mm, v(-5220.5, -966.27) * mm, v(-5219.04, -967.46) * mm, v(-5217.58, -968.67) * mm, v(-5215.74, -970.23) * mm, v(-5212.74, -972.82) * mm, v(-5208.91, -976.23) * mm, v(-5204.22, -980.6) * mm, v(-5197.85, -986.74) * mm, v(-5189.71, -995.04) * mm, v(-5179.77, -1005.83) * mm, v(-5169.76, -1017.36) * mm, v(-5159.74, -1029.5) * mm, v(-5146.5, -1046.35) * mm, v(-5133.5, -1063.96) * mm, v(-5121, -1081.88) * mm, v(-5111.89, -1095.37) * mm, v(-5103.1, -1108.78) * mm, v(-5094.66, -1122.03) * mm, v(-5086.62, -1135) * mm, v(-5079, -1147.58) * mm, v(-5071.83, -1159.69) * mm, v(-5065.13, -1171.2) * mm, v(-5059.98, -1180.25) * mm, v(-5056.1, -1187.1) * mm, v(-5053.34, -1192.04) * mm, v(-5050.71, -1196.77) * mm, v(-5048.21, -1201.28) * mm, v(-5045.85, -1205.56) * mm, v(-5043.62, -1209.62) * mm, v(-5041.53, -1213.45) * mm, v(-5039.56, -1217.05) * mm, v(-5038.01, -1219.87) * mm, v(-5036.82, -1222.03) * mm, v(-5035.95, -1223.6) * mm, v(-5035.1, -1225.15) * mm, v(-5034.26, -1226.67) * mm, v(-5033.42, -1228.17) * mm, v(-5032.57, -1229.68) * mm, v(-5031.69, -1231.22) * mm, v(-5030.76, -1232.84) * mm, v(-5029.9, -1234.29) * mm, v(-5029.15, -1235.56) * mm, v(-5028.53, -1236.58) * mm, v(-5027.84, -1237.7) * mm, v(-5027.06, -1238.95) * mm, v(-5026.16, -1240.37) * mm, v(-5025.09, -1242) * mm, v(-5023.78, -1243.93) * mm, v(-5022.13, -1246.28) * mm, v(-5020.32, -1248.73) * mm, v(-5018.45, -1251.14) * mm, v(-5016.77, -1253.22) * mm, v(-5014.72, -1255.64) * mm, v(-5012.17, -1258.5) * mm, v(-5009.47, -1261.34) * mm, v(-5006.8, -1263.97) * mm, v(-5004.49, -1266.15) * mm, v(-5001.8, -1268.55) * mm, v(-4998.63, -1271.2) * mm, v(-4994.88, -1274.14) * mm, v(-4990.38, -1277.39) * mm, v(-4984.92, -1280.94) * mm, v(-4978.24, -1284.78) * mm, v(-4970, -1288.83) * mm, v(-4961.47, -1292.23) * mm, v(-4953.4, -1294.76) * mm, v(-4946.69, -1296.49) * mm, v(-4939.25, -1297.96) * mm, v(-4931.06, -1299.05) * mm, v(-4922.12, -1299.64) * mm, v(-4912.48, -1299.56) * mm, v(-4902.24, -1298.67) * mm, v(-4891.55, -1296.84) * mm, v(-4880.63, -1293.97) * mm, v(-4869.76, -1290.03) * mm, v(-4859.21, -1285.08) * mm, v(-4849.26, -1279.23) * mm, v(-4840.1, -1272.68) * mm, v(-4831.89, -1265.65) * mm, v(-4824.69, -1258.36) * mm, v(-4818.5, -1251.03) * mm, v(-4813.26, -1243.83) * mm, v(-4808.89, -1236.87) * mm, v(-4805.27, -1230.25) * mm, v(-4802.32, -1224.02) * mm, v(-4799.92, -1218.2) * mm, v(-4797.34, -1210.99) * mm, v(-4795.06, -1202.97) * mm, v(-4793.36, -1194.8) * mm, v(-4792.34, -1187.83) * mm, v(-4791.77, -1181.9) * mm, v(-4791.5, -1176.79) * mm, v(-4791.43, -1172.37) * mm, v(-4791.5, -1168.53) * mm, v(-4791.65, -1165.17) * mm, v(-4791.92, -1161.22) * mm, v(-4792.35, -1157.1) * mm, v(-4792.9, -1153.13) * mm, v(-4793.44, -1149.86) * mm, v(-4793.96, -1147.12) * mm, v(-4794.45, -1144.8) * mm, v(-4795.06, -1142.13) * mm, v(-4795.73, -1139.43) * mm, v(-4796.44, -1136.86) * mm, v(-4797.05, -1134.75) * mm, v(-4797.6, -1132.97) * mm, v(-4798.1, -1131.42) * mm, v(-4798.54, -1130.04) * mm, v(-4798.96, -1128.8) * mm, v(-4799.36, -1127.64) * mm, v(-4799.74, -1126.56) * mm, v(-4800.23, -1125.2) * mm, v(-4800.58, -1124.22) * mm, v(-4800.8, -1123.59) * mm]});
            skLineSegment(sketch, "E401", {"start": v(-4920.05, -1167.3) * mm, "end": v(-4916.04, -1299.55) * mm});
            skLineSegment(sketch, "E402", {"start": v(-7459.34, 662.97) * mm, "end": v(-7454.14, 535.05) * mm});
            skSolve(sketch);
        }
        {
            var Q0;
            Q0 = qSketchRegion(id + "F252", true);
            extrude(context, id + "F253", {"entities" : qUnion([Q0]), "operationType" : NewBodyOperationType.ADD, "oppositeDirection" : true, "depth" : 25.4 * mm, "hasSecondDirection" : true, "secondDirectionOppositeDirection" : false, "secondDirectionDepth" : 12.7 * mm});
        }
    });
